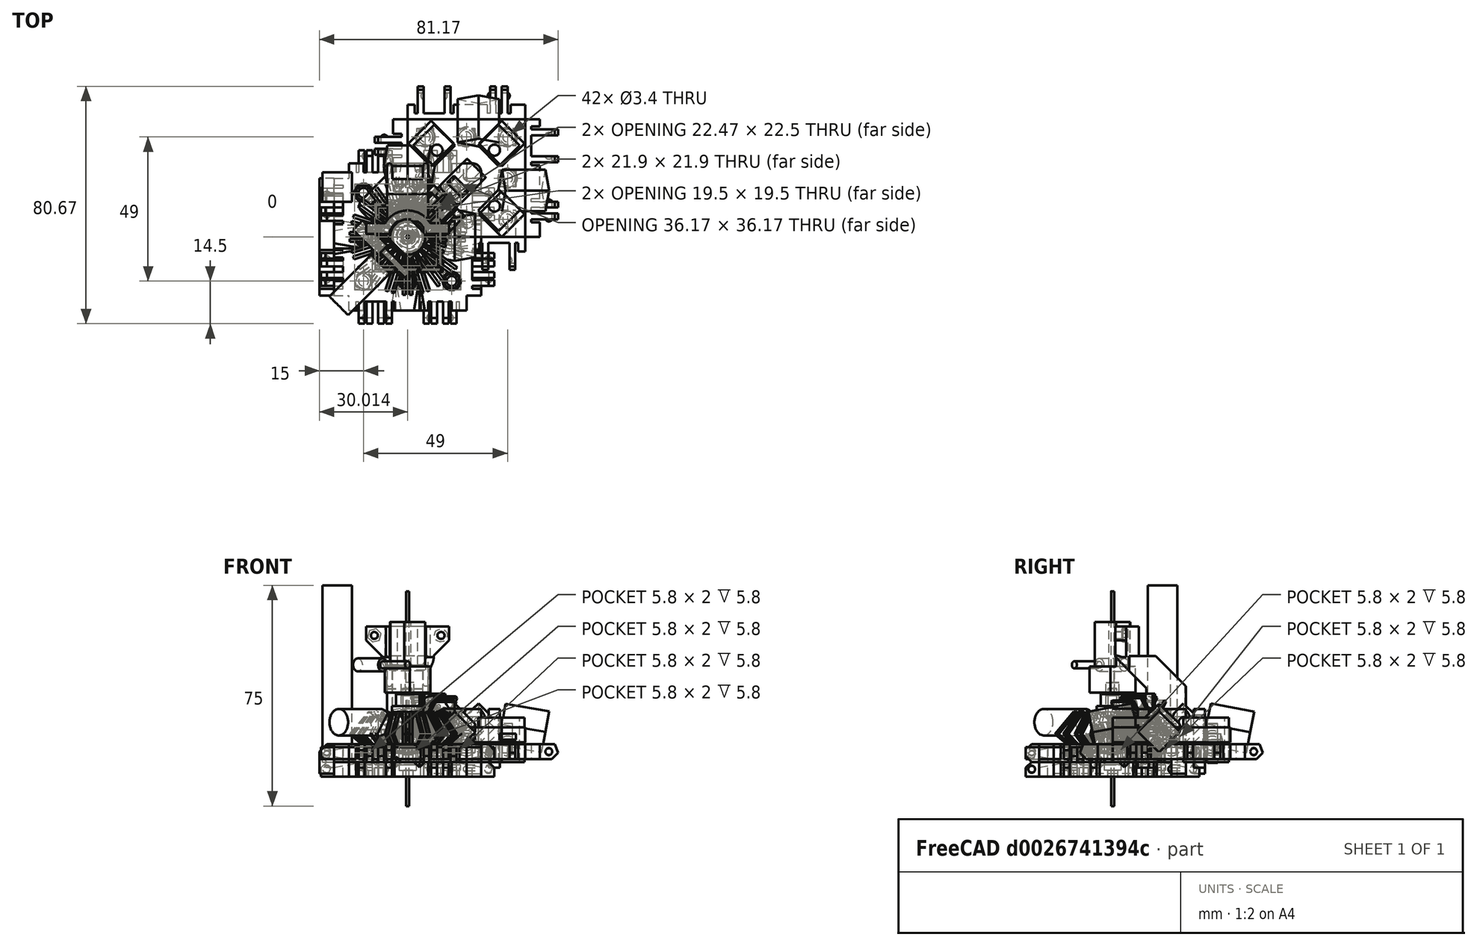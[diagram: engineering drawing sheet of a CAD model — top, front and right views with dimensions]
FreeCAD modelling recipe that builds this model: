
FCSTD DOCUMENT  (FreeCAD 0.18R16146 (Git))
Label: Robot 0.5
License: All rights reserved
LicenseURL: http://en.wikipedia.org/wiki/All_rights_reserved
objects: Part::Box×364, Part::Cut×149, Part::Sphere×107, Part::MultiFuse×99, Part::Cylinder×85, Part::Fuse×47, Part::Feature×40, Part::Chamfer×28, Drawing::FeatureViewAnnotation×17, App::DocumentObjectGroup×6, Part::Cone×5, Part::MultiCommon×5, Part::Fillet×5, Part::FeaturePython×3, Part::Mirroring×2, Drawing::FeaturePage×2
note: 939 computed .brp shape members not serialized (recipe doc carries the construction recipe); baked Part::Feature solids carry a one-line shape summary decoded from their .brp

FEATURE [Part::Box] Box  label="Cube"
  AttacherType = Attacher::AttachEngine3D
  Height = 5
  Length = 40
  Placement = pos=(-20,-20,-2) rot=(0,0,1;0rad)
  Width = 40
FEATURE [Part::Sphere] Sphere003  label="Mag Hole 3"
  Angle1 = -90
  Angle2 = 90
  Angle3 = 360
  AttacherType = Attacher::AttachEngine3D
  Placement = pos=(-15,15,1.7) rot=(0,0,1;0rad)
  Radius = 2.83
FEATURE [Part::Sphere] Sphere005  label="Mag Hole 2"
  Angle1 = -90
  Angle2 = 90
  Angle3 = 360
  AttacherType = Attacher::AttachEngine3D
  Placement = pos=(15,0,1.7) rot=(0,0,1;0rad)
  Radius = 2.825
FEATURE [Part::Sphere] Sphere  label="Mag Hole"
  Angle1 = -90
  Angle2 = 90
  Angle3 = 360
  AttacherType = Attacher::AttachEngine3D
  Placement = pos=(-15,-15,1.7) rot=(0,0,1;0rad)
  Radius = 2.83
FEATURE [Part::MultiFuse] Fusion004  label="Ball Holes"
  Shapes = -> [Sphere,Sphere005,Sphere003]
FEATURE [Part::Cut] Cut003
  Base = -> Box
  Tool = -> Fusion004
FEATURE [Part::Box] Box001  label="Cube001"
  AttacherType = Attacher::AttachEngine3D
  Height = 7
  Length = 5
  Placement = pos=(-5,0,-2) rot=(0,0,1;0rad)
  Width = 40
FEATURE [Part::Box] Box002  label="Cube002"
  AttacherType = Attacher::AttachEngine3D
  Height = 7
  Length = 10
  Placement = pos=(-15,6,-2) rot=(0,0,1;0rad)
  Width = 2
FEATURE [Part::Box] Box003  label="Cube003"
  AttacherType = Attacher::AttachEngine3D
  Height = 7
  Length = 10
  Placement = pos=(-15,10,-2) rot=(0,0,1;0rad)
  Width = 2
FEATURE [Part::Box] Box004  label="Cube004"
  AttacherType = Attacher::AttachEngine3D
  Height = 7
  Length = 10
  Placement = pos=(-15,25.4,-2) rot=(0,0,1;0rad)
  Width = 2
FEATURE [Part::Box] Box005  label="Cube005"
  AttacherType = Attacher::AttachEngine3D
  Height = 7
  Length = 10
  Placement = pos=(-15,34.6,-2) rot=(0,0,1;0rad)
  Width = 2
FEATURE [Part::Sphere] Sphere008
  Angle1 = -90
  Angle2 = 90
  Angle3 = 360
  AttacherType = Attacher::AttachEngine3D
  Placement = pos=(-7.5,6.5,0.5) rot=(0,0,1;0rad)
  Radius = 1.25
FEATURE [Part::Box] Box006  label="Chamfer Cube"
  AttacherType = Attacher::AttachEngine3D
  Height = 10
  Length = 13
  Placement = pos=(-11.69,0,-1.19) rot=(0,-1,0;0.785398rad)
  Width = 40
FEATURE [Part::Sphere] Sphere009
  Angle1 = -90
  Angle2 = 90
  Angle3 = 360
  AttacherType = Attacher::AttachEngine3D
  Placement = pos=(-7.5,11.5,0.5) rot=(0,0,1;0rad)
  Radius = 1.25
FEATURE [Part::Sphere] Sphere010
  Angle1 = -90
  Angle2 = 90
  Angle3 = 360
  AttacherType = Attacher::AttachEngine3D
  Placement = pos=(-7.5,28,0.5) rot=(0,0,1;0rad)
  Radius = 1.5
FEATURE [Part::Sphere] Sphere011
  Angle1 = -90
  Angle2 = 90
  Angle3 = 360
  AttacherType = Attacher::AttachEngine3D
  Placement = pos=(-7.5,34,0.5) rot=(0,0,1;0rad)
  Radius = 1.5
FEATURE [Part::Box] Box007  label="Cube007"
  AttacherType = Attacher::AttachEngine3D
  Height = 7
  Length = 4
  Placement = pos=(-6,5,-2) rot=(0,0,1;0rad)
  Width = 1
FEATURE [Part::Box] Box008  label="Cube008"
  AttacherType = Attacher::AttachEngine3D
  Height = 7
  Length = 4
  Placement = pos=(-6,8,-2) rot=(0,0,1;0rad)
  Width = 2
FEATURE [Part::Box] Box009  label="Cube009"
  AttacherType = Attacher::AttachEngine3D
  Height = 7
  Length = 4
  Placement = pos=(-6,12,-2) rot=(0,0,1;0rad)
  Width = 1
FEATURE [Part::Box] Box010  label="Cube010"
  AttacherType = Attacher::AttachEngine3D
  Height = 7
  Length = 4
  Placement = pos=(-6,24.4,-2) rot=(0,0,1;0rad)
  Width = 1
FEATURE [Part::Box] Box011  label="Cube011"
  AttacherType = Attacher::AttachEngine3D
  Height = 7
  Length = 4
  Placement = pos=(-6,36.6,-2) rot=(0,0,1;0rad)
  Width = 1
FEATURE [Part::Box] Box012  label="Cube012"
  AttacherType = Attacher::AttachEngine3D
  Height = 7
  Length = 4
  Placement = pos=(-6,27.4,-2) rot=(0,0,1;0rad)
  Width = 7.2
FEATURE [Part::MultiFuse] Fusion003  label="Extra Holes for Clips"
  Shapes = -> [Box012,Box009,Box011,Box008,Box010,Box007]
FEATURE [Part::Box] Box013  label="Re-level Edge Clip Block"
  AttacherType = Attacher::AttachEngine3D
  Height = 10
  Length = 20
  Placement = pos=(-19,-2,3) rot=(0,0,1;0rad)
  Width = 44
FEATURE [Part::Box] Box014  label="Cube014"
  AttacherType = Attacher::AttachEngine3D
  Height = 7
  Length = 10
  Placement = pos=(-10,34.6,0) rot=(0,0,1;0rad)
  Width = 2
FEATURE [Part::Box] Box015  label="Cube015"
  AttacherType = Attacher::AttachEngine3D
  Height = 7
  Length = 5
  Width = 40
FEATURE [Part::Box] Box016  label="Cube016"
  AttacherType = Attacher::AttachEngine3D
  Height = 7
  Length = 10
  Placement = pos=(-10,25.4,0) rot=(0,0,1;0rad)
  Width = 2
FEATURE [Part::Box] Box017  label="Cube017"
  AttacherType = Attacher::AttachEngine3D
  Height = 7
  Length = 10
  Placement = pos=(-10,10,0) rot=(0,0,1;0rad)
  Width = 2
FEATURE [Part::Box] Box018  label="Cube018"
  AttacherType = Attacher::AttachEngine3D
  Height = 7
  Length = 10
  Placement = pos=(-10,6,0) rot=(0,0,1;0rad)
  Width = 2
FEATURE [Part::Sphere] Sphere012
  Angle1 = -90
  Angle2 = 90
  Angle3 = 360
  AttacherType = Attacher::AttachEngine3D
  Placement = pos=(-3,6.5,2.5) rot=(0,0,1;0rad)
  Radius = 1.25
FEATURE [Part::Box] Box019  label="Cube019"
  AttacherType = Attacher::AttachEngine3D
  Height = 10
  Length = 13
  Placement = pos=(-10.19,0,-1.19) rot=(0,-1,0;0.785398rad)
  Width = 40
FEATURE [Part::Sphere] Sphere013
  Angle1 = -90
  Angle2 = 90
  Angle3 = 360
  AttacherType = Attacher::AttachEngine3D
  Placement = pos=(-3,11.5,2.5) rot=(0,0,1;0rad)
  Radius = 1.25
FEATURE [Part::Sphere] Sphere014
  Angle1 = -90
  Angle2 = 90
  Angle3 = 360
  AttacherType = Attacher::AttachEngine3D
  Placement = pos=(-3,28,2.5) rot=(0,0,1;0rad)
  Radius = 1.5
FEATURE [Part::Sphere] Sphere015
  Angle1 = -90
  Angle2 = 90
  Angle3 = 360
  AttacherType = Attacher::AttachEngine3D
  Placement = pos=(-3,34,2.5) rot=(0,0,1;0rad)
  Radius = 1.5
FEATURE [Part::MultiFuse] Fusion005
  Shapes = -> [Box015,Box018,Box017,Box016,Box014]
FEATURE [Part::Cut] Cut005
  Base = -> Fusion005
  Tool = -> Box019
FEATURE [Part::MultiFuse] Fusion006
  Shapes = -> [Sphere012,Sphere013,Cut005]
FEATURE [Part::MultiFuse] Fusion007
  Shapes = -> [Sphere015,Sphere014]
FEATURE [Part::Cut] Cut006
  Base = -> Fusion006
  Tool = -> Fusion007
FEATURE [Part::Chamfer] Chamfer002
  Base = -> Cut006
  Edges = 4 edges r=4: [Edge31,Edge37,Edge43,Edge46]
FEATURE [Part::Box] Box020  label="Cube020"
  AttacherType = Attacher::AttachEngine3D
  Height = 7
  Length = 4
  Placement = pos=(-1,5,0) rot=(0,0,1;0rad)
  Width = 1
FEATURE [Part::Box] Box021  label="Cube021"
  AttacherType = Attacher::AttachEngine3D
  Height = 7
  Length = 4
  Placement = pos=(-1,8,0) rot=(0,0,1;0rad)
  Width = 2
FEATURE [Part::Box] Box022  label="Cube022"
  AttacherType = Attacher::AttachEngine3D
  Height = 7
  Length = 4
  Placement = pos=(-1,12,0) rot=(0,0,1;0rad)
  Width = 1
FEATURE [Part::Box] Box023  label="Cube023"
  AttacherType = Attacher::AttachEngine3D
  Height = 7
  Length = 4
  Placement = pos=(-1,24.4,0) rot=(0,0,1;0rad)
  Width = 1
FEATURE [Part::Box] Box024  label="Cube024"
  AttacherType = Attacher::AttachEngine3D
  Height = 7
  Length = 4
  Placement = pos=(-1,36.6,0) rot=(0,0,1;0rad)
  Width = 1
FEATURE [Part::Box] Box025  label="Cube025"
  AttacherType = Attacher::AttachEngine3D
  Height = 7
  Length = 4
  Placement = pos=(-1,27.4,0) rot=(0,0,1;0rad)
  Width = 7.2
FEATURE [Part::MultiFuse] Fusion008
  Shapes = -> [Box025,Box022,Box024,Box021,Box023,Box020]
FEATURE [Part::Cut] Cut007
  Base = -> Chamfer002
  Placement = pos=(-5,40,3) rot=(1,0,0;3.14159rad)
  Tool = -> Fusion008
FEATURE [Part::Box] Box026  label="Cube026"
  AttacherType = Attacher::AttachEngine3D
  Height = 10
  Length = 12
  Placement = pos=(-11,-2,-12) rot=(0,0,1;0rad)
  Width = 44
FEATURE [Part::Cut] Cut008
  Base = -> Cut007
  Placement = pos=(40,0,0) rot=(0,0,1;1.5708rad)
  Tool = -> Box026
FEATURE [Part::Box] Box027  label="Cube027"
  AttacherType = Attacher::AttachEngine3D
  Height = 7
  Length = 4
  Placement = pos=(-1,12,0) rot=(0,0,1;0rad)
  Width = 1
FEATURE [Part::Box] Box028  label="Cube028"
  AttacherType = Attacher::AttachEngine3D
  Height = 10
  Length = 13
  Placement = pos=(-10.19,0,-1.19) rot=(0,-1,0;0.785398rad)
  Width = 40
FEATURE [Part::Box] Box029  label="Cube029"
  AttacherType = Attacher::AttachEngine3D
  Height = 7
  Length = 4
  Placement = pos=(-1,27.4,0) rot=(0,0,1;0rad)
  Width = 7.2
FEATURE [Part::Box] Box030  label="Cube030"
  AttacherType = Attacher::AttachEngine3D
  Height = 7
  Length = 4
  Placement = pos=(-1,5,0) rot=(0,0,1;0rad)
  Width = 1
FEATURE [Part::Box] Box031  label="Cube031"
  AttacherType = Attacher::AttachEngine3D
  Height = 7
  Length = 10
  Placement = pos=(-10,6,0) rot=(0,0,1;0rad)
  Width = 2
FEATURE [Part::Box] Box032  label="Cube032"
  AttacherType = Attacher::AttachEngine3D
  Height = 10
  Length = 12
  Placement = pos=(-11,-2,-12) rot=(0,0,1;0rad)
  Width = 44
FEATURE [Part::Sphere] Sphere016
  Angle1 = -90
  Angle2 = 90
  Angle3 = 360
  AttacherType = Attacher::AttachEngine3D
  Placement = pos=(-3,6.5,2.5) rot=(0,0,1;0rad)
  Radius = 1.25
FEATURE [Part::Box] Box033  label="Cube033"
  AttacherType = Attacher::AttachEngine3D
  Height = 7
  Length = 10
  Placement = pos=(-10,25.4,0) rot=(0,0,1;0rad)
  Width = 2
FEATURE [Part::Box] Box034  label="Cube034"
  AttacherType = Attacher::AttachEngine3D
  Height = 7
  Length = 10
  Placement = pos=(-10,10,0) rot=(0,0,1;0rad)
  Width = 2
FEATURE [Part::Sphere] Sphere017
  Angle1 = -90
  Angle2 = 90
  Angle3 = 360
  AttacherType = Attacher::AttachEngine3D
  Placement = pos=(-3,28,2.5) rot=(0,0,1;0rad)
  Radius = 1.5
FEATURE [Part::Sphere] Sphere018
  Angle1 = -90
  Angle2 = 90
  Angle3 = 360
  AttacherType = Attacher::AttachEngine3D
  Placement = pos=(-3,11.5,2.5) rot=(0,0,1;0rad)
  Radius = 1.25
FEATURE [Part::Box] Box035  label="Cube035"
  AttacherType = Attacher::AttachEngine3D
  Height = 7
  Length = 4
  Placement = pos=(-1,36.6,0) rot=(0,0,1;0rad)
  Width = 1
FEATURE [Part::Sphere] Sphere019
  Angle1 = -90
  Angle2 = 90
  Angle3 = 360
  AttacherType = Attacher::AttachEngine3D
  Placement = pos=(-3,34,2.5) rot=(0,0,1;0rad)
  Radius = 1.5
FEATURE [Part::MultiFuse] Fusion011
  Shapes = -> [Sphere019,Sphere017]
FEATURE [Part::Box] Box036  label="Cube036"
  AttacherType = Attacher::AttachEngine3D
  Height = 7
  Length = 4
  Placement = pos=(-1,8,0) rot=(0,0,1;0rad)
  Width = 2
FEATURE [Part::Box] Box037  label="Cube037"
  AttacherType = Attacher::AttachEngine3D
  Height = 7
  Length = 10
  Placement = pos=(-10,34.6,0) rot=(0,0,1;0rad)
  Width = 2
FEATURE [Part::Box] Box038  label="Cube038"
  AttacherType = Attacher::AttachEngine3D
  Height = 7
  Length = 4
  Placement = pos=(-1,24.4,0) rot=(0,0,1;0rad)
  Width = 1
FEATURE [Part::MultiFuse] Fusion009
  Shapes = -> [Box029,Box027,Box035,Box036,Box038,Box030]
FEATURE [Part::Box] Box039  label="Cube039"
  AttacherType = Attacher::AttachEngine3D
  Height = 7
  Length = 5
  Width = 40
FEATURE [Part::MultiFuse] Fusion012
  Shapes = -> [Box039,Box031,Box034,Box033,Box037]
FEATURE [Part::Cut] Cut011
  Base = -> Fusion012
  Tool = -> Box028
FEATURE [Part::MultiFuse] Fusion010
  Shapes = -> [Sphere016,Sphere018,Cut011]
FEATURE [Part::Cut] Cut012
  Base = -> Fusion010
  Tool = -> Fusion011
FEATURE [Part::Chamfer] Chamfer003
  Base = -> Cut012
  Edges = 4 edges r=4: [Edge31,Edge37,Edge43,Edge46]
FEATURE [Part::Cut] Cut010
  Base = -> Chamfer003
  Placement = pos=(-5,40,3) rot=(1,0,0;3.14159rad)
  Tool = -> Fusion009
FEATURE [Part::Cut] Cut009
  Base = -> Cut010
  Placement = pos=(40,40,0) rot=(0,0,1;3.14159rad)
  Tool = -> Box032
FEATURE [Part::Sphere] Sphere020
  Angle1 = -90
  Angle2 = 90
  Angle3 = 360
  AttacherType = Attacher::AttachEngine3D
  Placement = pos=(-3,11.5,2.5) rot=(0,0,1;0rad)
  Radius = 1.25
FEATURE [Part::Box] Box040  label="Cube040"
  AttacherType = Attacher::AttachEngine3D
  Height = 7
  Length = 10
  Placement = pos=(-10,6,0) rot=(0,0,1;0rad)
  Width = 2
FEATURE [Part::Box] Box041  label="Cube041"
  AttacherType = Attacher::AttachEngine3D
  Height = 7
  Length = 4
  Placement = pos=(-1,8,0) rot=(0,0,1;0rad)
  Width = 2
FEATURE [Part::Box] Box042  label="Cube042"
  AttacherType = Attacher::AttachEngine3D
  Height = 7
  Length = 10
  Placement = pos=(-10,10,0) rot=(0,0,1;0rad)
  Width = 2
FEATURE [Part::Box] Box043  label="Cube043"
  AttacherType = Attacher::AttachEngine3D
  Height = 10
  Length = 12
  Placement = pos=(-11,-2,-12) rot=(0,0,1;0rad)
  Width = 44
FEATURE [Part::Box] Box044  label="Cube044"
  AttacherType = Attacher::AttachEngine3D
  Height = 7
  Length = 4
  Placement = pos=(-1,5,0) rot=(0,0,1;0rad)
  Width = 1
FEATURE [Part::Sphere] Sphere021
  Angle1 = -90
  Angle2 = 90
  Angle3 = 360
  AttacherType = Attacher::AttachEngine3D
  Placement = pos=(-3,28,2.5) rot=(0,0,1;0rad)
  Radius = 1.5
FEATURE [Part::Sphere] Sphere022
  Angle1 = -90
  Angle2 = 90
  Angle3 = 360
  AttacherType = Attacher::AttachEngine3D
  Placement = pos=(-3,6.5,2.5) rot=(0,0,1;0rad)
  Radius = 1.25
FEATURE [Part::Sphere] Sphere023
  Angle1 = -90
  Angle2 = 90
  Angle3 = 360
  AttacherType = Attacher::AttachEngine3D
  Placement = pos=(-3,34,2.5) rot=(0,0,1;0rad)
  Radius = 1.5
FEATURE [Part::Box] Box045  label="Cube045"
  AttacherType = Attacher::AttachEngine3D
  Height = 7
  Length = 4
  Placement = pos=(-1,12,0) rot=(0,0,1;0rad)
  Width = 1
FEATURE [Part::Box] Box046  label="Cube046"
  AttacherType = Attacher::AttachEngine3D
  Height = 7
  Length = 5
  Width = 40
FEATURE [Part::Box] Box047  label="Cube047"
  AttacherType = Attacher::AttachEngine3D
  Height = 7
  Length = 4
  Placement = pos=(-1,36.6,0) rot=(0,0,1;0rad)
  Width = 1
FEATURE [Part::Box] Box048  label="Cube048"
  AttacherType = Attacher::AttachEngine3D
  Height = 7
  Length = 4
  Placement = pos=(-1,24.4,0) rot=(0,0,1;0rad)
  Width = 1
FEATURE [Part::Box] Box049  label="Cube049"
  AttacherType = Attacher::AttachEngine3D
  Height = 7
  Length = 10
  Placement = pos=(-10,25.4,0) rot=(0,0,1;0rad)
  Width = 2
FEATURE [Part::Box] Box050  label="Cube050"
  AttacherType = Attacher::AttachEngine3D
  Height = 10
  Length = 13
  Placement = pos=(-10.19,0,-1.19) rot=(0,-1,0;0.785398rad)
  Width = 40
FEATURE [Part::Box] Box051  label="Cube051"
  AttacherType = Attacher::AttachEngine3D
  Height = 7
  Length = 10
  Placement = pos=(-10,34.6,0) rot=(0,0,1;0rad)
  Width = 2
FEATURE [Part::MultiFuse] Fusion015
  Shapes = -> [Box046,Box040,Box042,Box049,Box051]
FEATURE [Part::Cut] Cut013
  Base = -> Fusion015
  Tool = -> Box050
FEATURE [Part::MultiFuse] Fusion013
  Shapes = -> [Sphere022,Sphere020,Cut013]
FEATURE [Part::MultiFuse] Fusion016
  Shapes = -> [Sphere023,Sphere021]
FEATURE [Part::Cut] Cut014
  Base = -> Fusion013
  Tool = -> Fusion016
FEATURE [Part::Chamfer] Chamfer004
  Base = -> Cut014
  Edges = 4 edges r=4: [Edge31,Edge37,Edge43,Edge46]
FEATURE [Part::Box] Box052  label="Cube052"
  AttacherType = Attacher::AttachEngine3D
  Height = 7
  Length = 4
  Placement = pos=(-1,27.4,0) rot=(0,0,1;0rad)
  Width = 7.2
FEATURE [Part::MultiFuse] Fusion014
  Shapes = -> [Box052,Box045,Box047,Box041,Box048,Box044]
FEATURE [Part::Cut] Cut016
  Base = -> Chamfer004
  Placement = pos=(-5,40,3) rot=(1,0,0;3.14159rad)
  Tool = -> Fusion014
FEATURE [Part::Cut] Cut015
  Base = -> Cut016
  Placement = pos=(0,40,0) rot=(0,0,-1;1.5708rad)
  Tool = -> Box043
FEATURE [Part::Box] Box054  label="Cube054"
  AttacherType = Attacher::AttachEngine3D
  Height = 15
  Length = 10
  Placement = pos=(9,2,-3) rot=(0,0,1;0.785398rad)
  Width = 10
FEATURE [Part::Box] Box055  label="Cube055"
  AttacherType = Attacher::AttachEngine3D
  Height = 15
  Length = 10
  Placement = pos=(31,24,-3) rot=(0,0,1;0.785398rad)
  Width = 10
FEATURE [Part::Box] Box056  label="Cube056"
  AttacherType = Attacher::AttachEngine3D
  Height = 15
  Length = 10
  Placement = pos=(31,2,-3) rot=(0,0,1;0.785398rad)
  Width = 10
FEATURE [Part::Box] Box057  label="Cube057"
  AttacherType = Attacher::AttachEngine3D
  Height = 15
  Length = 10
  Placement = pos=(9,24,-3) rot=(0,0,1;0.785398rad)
  Width = 10
FEATURE [Part::MultiFuse] Fusion017
  Shapes = -> [Box054,Box057,Box056,Box055]
FEATURE [Part::Box] Box058  label="Cube058"
  AttacherType = Attacher::AttachEngine3D
  Height = 5
  Length = 40
  Placement = pos=(0,0,3.7) rot=(0,0,1;0rad)
  Width = 40
FEATURE [Part::Box] Box059  label="Square Nut Hole 008"
  AttacherType = Attacher::AttachEngine3D
  Height = 2
  Length = 5.6
  Placement = pos=(17.2,31.2,4.6) rot=(0,0,1;0rad)
  Width = 5.6
FEATURE [Part::Box] Box060  label="Square Nut Hole 009"
  AttacherType = Attacher::AttachEngine3D
  Height = 2
  Length = 5.6
  Placement = pos=(17.2,-0.85,4.6) rot=(0,0,1;0rad)
  Width = 10
FEATURE [Part::Box] Box061  label="Square Nut Hole 010"
  AttacherType = Attacher::AttachEngine3D
  Height = 2
  Length = 5.6
  Placement = pos=(31.2,-0.85,4.6) rot=(0,0,1;0rad)
  Width = 10
FEATURE [Part::Box] Box062  label="Square Nut Hole 011"
  AttacherType = Attacher::AttachEngine3D
  Height = 2
  Length = 5.4
  Placement = pos=(31.3,17.3,4.6) rot=(0,0,1;0rad)
  Width = 5.4
FEATURE [Part::Box] Box063  label="Square Nut Hole 012"
  AttacherType = Attacher::AttachEngine3D
  Height = 2
  Length = 5.7
  Placement = pos=(3.15,31.15,4.6) rot=(0,0,1;0rad)
  Width = 5.7
FEATURE [Part::Box] Box064  label="Square Nut Hole 013"
  AttacherType = Attacher::AttachEngine3D
  Height = 2
  Length = 5.5
  Placement = pos=(31.25,31.25,4.6) rot=(0,0,1;0rad)
  Width = 5.5
FEATURE [Part::Box] Box065  label="Square Nut Hole 014"
  AttacherType = Attacher::AttachEngine3D
  Height = 2
  Length = 5.8
  Placement = pos=(3.1,17.1,4.6) rot=(0,0,1;0rad)
  Width = 5.8
FEATURE [Part::Box] Box066  label="Square Nut Hole 015"
  AttacherType = Attacher::AttachEngine3D
  Height = 2
  Length = 5.6
  Placement = pos=(3.2,-0.85,4.6) rot=(0,0,1;0rad)
  Width = 10
FEATURE [Part::Sphere] Sphere006  label="Nut Clearence1"
  Angle1 = -90
  Angle2 = 90
  Angle3 = 360
  AttacherType = Attacher::AttachEngine3D
  Placement = pos=(6,6,2.4) rot=(0,0,1;0rad)
  Radius = 3.35
FEATURE [Part::Sphere] Sphere024
  Angle1 = -90
  Angle2 = 90
  Angle3 = 360
  AttacherType = Attacher::AttachEngine3D
  Placement = pos=(6,34,2.4) rot=(0,0,1;0rad)
  Radius = 3.35
FEATURE [Part::Sphere] Sphere007
  Angle1 = -90
  Angle2 = 90
  Angle3 = 360
  AttacherType = Attacher::AttachEngine3D
  Placement = pos=(34,20,2.4) rot=(0,0,1;0rad)
  Radius = 3.35
FEATURE [Part::Sphere] Sphere001
  Angle1 = -90
  Angle2 = 90
  Angle3 = 360
  AttacherType = Attacher::AttachEngine3D
  Placement = pos=(34,6,2.4) rot=(0,0,1;0rad)
  Radius = 3.35
FEATURE [Part::Sphere] Sphere025
  Angle1 = -90
  Angle2 = 90
  Angle3 = 360
  AttacherType = Attacher::AttachEngine3D
  Placement = pos=(20,6,2.4) rot=(0,0,1;0rad)
  Radius = 3.35
FEATURE [Part::Sphere] Sphere026
  Angle1 = -90
  Angle2 = 90
  Angle3 = 360
  AttacherType = Attacher::AttachEngine3D
  Placement = pos=(20,34,2.4) rot=(0,0,1;0rad)
  Radius = 3.35
FEATURE [Part::Sphere] Sphere004
  Angle1 = -90
  Angle2 = 90
  Angle3 = 360
  AttacherType = Attacher::AttachEngine3D
  Placement = pos=(6,20,2.4) rot=(0,0,1;0rad)
  Radius = 3.35
FEATURE [Part::Sphere] Sphere002
  Angle1 = -90
  Angle2 = 90
  Angle3 = 360
  AttacherType = Attacher::AttachEngine3D
  Placement = pos=(34,34,2.4) rot=(0,0,1;0rad)
  Radius = 3.35
FEATURE [Part::Cylinder] Cylinder
  Angle = 360
  AttacherType = Attacher::AttachEngine3D
  Height = 10
  Placement = pos=(6,6,0) rot=(0,0,1;0rad)
  Radius = 1.7
FEATURE [Part::Cylinder] Cylinder002
  Angle = 360
  AttacherType = Attacher::AttachEngine3D
  Height = 10
  Placement = pos=(34,6,0) rot=(0,0,1;0rad)
  Radius = 1.7
FEATURE [Part::Cylinder] Cylinder001
  Angle = 360
  AttacherType = Attacher::AttachEngine3D
  Height = 10
  Placement = pos=(20,6,0) rot=(0,0,1;0rad)
  Radius = 1.7
FEATURE [Part::Cylinder] Cylinder003
  Angle = 360
  AttacherType = Attacher::AttachEngine3D
  Height = 10
  Placement = pos=(34,34,0) rot=(0,0,1;0rad)
  Radius = 1.7
FEATURE [Part::Cylinder] Cylinder004
  Angle = 360
  AttacherType = Attacher::AttachEngine3D
  Height = 10
  Placement = pos=(20,34,0) rot=(0,0,1;0rad)
  Radius = 1.7
FEATURE [Part::Cylinder] Cylinder005
  Angle = 360
  AttacherType = Attacher::AttachEngine3D
  Height = 10
  Placement = pos=(6,34,0) rot=(0,0,1;0rad)
  Radius = 1.7
FEATURE [Part::Cylinder] Cylinder006
  Angle = 360
  AttacherType = Attacher::AttachEngine3D
  Height = 10
  Placement = pos=(6,20,0) rot=(0,0,1;0rad)
  Radius = 1.7
FEATURE [Part::Cylinder] Cylinder007
  Angle = 360
  AttacherType = Attacher::AttachEngine3D
  Height = 10
  Placement = pos=(34,20,0) rot=(0,0,1;0rad)
  Radius = 1.7
FEATURE [Part::MultiFuse] Fusion018
  Shapes = -> [Cylinder,Cylinder004,Cylinder007,Cylinder005,Cylinder006,Cylinder001,Cylinder002,Cylinder003]
FEATURE [Part::MultiFuse] Fusion019
  Shapes = -> [Sphere007,Sphere024,Sphere006,Sphere025,Sphere001,Sphere026,Sphere004,Sphere002]
FEATURE [Part::MultiFuse] Fusion020
  Shapes = -> [Box061,Box065,Box062,Box063,Box064,Box066,Box059,Box060]
FEATURE [Part::Cut] Cut017
  Base = -> Box058
  Tool = -> Fusion020
FEATURE [Part::Cut] Cut019
  Base = -> Cut017
  Tool = -> Fusion019
FEATURE [Part::Cut] Cut018
  Base = -> Cut019
  Tool = -> Fusion018
FEATURE [Part::Cylinder] Cylinder008
  Angle = 360
  AttacherType = Attacher::AttachEngine3D
  Height = 20
  Placement = pos=(10,10.5,-5) rot=(0,0,1;0rad)
  Radius = 1.9
FEATURE [Part::Cylinder] Cylinder009
  Angle = 360
  AttacherType = Attacher::AttachEngine3D
  Height = 20
  Placement = pos=(29.5,10.5,-5) rot=(0,0,1;0rad)
  Radius = 1.9
FEATURE [Part::Cylinder] Cylinder010
  Angle = 360
  AttacherType = Attacher::AttachEngine3D
  Height = 20
  Placement = pos=(29.5,29.5,-5) rot=(0,0,1;0rad)
  Radius = 1.9
FEATURE [Part::Cylinder] Cylinder011
  Angle = 360
  AttacherType = Attacher::AttachEngine3D
  Height = 20
  Placement = pos=(10,29.5,-7) rot=(0,0,1;0rad)
  Radius = 1.9
FEATURE [Part::MultiFuse] Fusion021  label="M2 Screw holes"
  Shapes = -> [Cylinder008,Cylinder009,Cylinder011,Cylinder010]
FEATURE [Part::Box] Box067  label="Square Nut Hole 016"
  AttacherType = Attacher::AttachEngine3D
  Height = 2
  Length = 5.8
  Placement = pos=(31.1,17.1,4.6) rot=(0,0,1;0rad)
  Width = 5.8
FEATURE [Part::Box] Box068  label="Square Nut Hole 017"
  AttacherType = Attacher::AttachEngine3D
  Height = 2
  Length = 5.8
  Placement = pos=(17.1,36.9,2.1) rot=(1,0,0;3.14159rad)
  Width = 5.8
FEATURE [Part::Box] Box069  label="Square Nut Hole 018"
  AttacherType = Attacher::AttachEngine3D
  Height = 2
  Length = 5.8
  Placement = pos=(-2.9,2.9,2.1) rot=(1,0,0;3.14159rad)
  Width = 5.8
FEATURE [Part::Box] Box070  label="Square Nut Hole 019"
  AttacherType = Attacher::AttachEngine3D
  Height = 2
  Length = 5.8
  Placement = pos=(3.1,3.1,4.6) rot=(0,0,1;0rad)
  Width = 5.8
FEATURE [Part::Box] Box071  label="Square Nut Hole 020"
  AttacherType = Attacher::AttachEngine3D
  Height = 2
  Length = 5.8
  Placement = pos=(3.1,31.1,4.6) rot=(0,0,1;0rad)
  Width = 5.8
FEATURE [Part::Box] Box072  label="Square Nut Hole 021"
  AttacherType = Attacher::AttachEngine3D
  Height = 2
  Length = 5.8
  Placement = pos=(17.1,31.1,4.6) rot=(0,0,1;0rad)
  Width = 5.8
FEATURE [Part::Box] Box073  label="Square Nut Hole 022"
  AttacherType = Attacher::AttachEngine3D
  Height = 2
  Length = 5.8
  Placement = pos=(31.1,31.1,4.6) rot=(0,0,1;0rad)
  Width = 5.8
FEATURE [Part::Box] Box074  label="Square Nut Hole 023"
  AttacherType = Attacher::AttachEngine3D
  Height = 2
  Length = 5.8
  Placement = pos=(3.1,17.1,4.6) rot=(0,0,1;0rad)
  Width = 5.8
FEATURE [Part::Cylinder] Cylinder012
  Angle = 360
  AttacherType = Attacher::AttachEngine3D
  Height = 10
  Placement = pos=(6,6,0) rot=(0,0,1;0rad)
  Radius = 1.7
FEATURE [Part::Cylinder] Cylinder013
  Angle = 360
  AttacherType = Attacher::AttachEngine3D
  Height = 10
  Placement = pos=(34,34,0) rot=(0,0,1;0rad)
  Radius = 1.7
FEATURE [Part::Cylinder] Cylinder014
  Angle = 360
  AttacherType = Attacher::AttachEngine3D
  Height = 10
  Placement = pos=(20,34,0) rot=(0,0,1;0rad)
  Radius = 1.7
FEATURE [Part::Cylinder] Cylinder015
  Angle = 360
  AttacherType = Attacher::AttachEngine3D
  Height = 10
  Placement = pos=(6,34,0) rot=(0,0,1;0rad)
  Radius = 1.7
FEATURE [Part::Cylinder] Cylinder016
  Angle = 360
  AttacherType = Attacher::AttachEngine3D
  Height = 10
  Placement = pos=(6,20,0) rot=(0,0,1;0rad)
  Radius = 1.7
FEATURE [Part::Cylinder] Cylinder017
  Angle = 360
  AttacherType = Attacher::AttachEngine3D
  Height = 10
  Placement = pos=(34,20,0) rot=(0,0,1;0rad)
  Radius = 1.7
FEATURE [Part::Cylinder] Cylinder018
  Angle = 360
  AttacherType = Attacher::AttachEngine3D
  Height = 10
  Placement = pos=(0,0,6.7) rot=(1,0,0;3.14159rad)
  Radius = 1.7
FEATURE [Part::Cylinder] Cylinder019
  Angle = 360
  AttacherType = Attacher::AttachEngine3D
  Height = 10
  Placement = pos=(20,34,6.7) rot=(1,0,0;3.14159rad)
  Radius = 1.7
FEATURE [Part::Box] Box075  label="Cube059"
  AttacherType = Attacher::AttachEngine3D
  Height = 5
  Length = 40
  Placement = pos=(-20,-20,-2) rot=(0,0,1;0rad)
  Width = 40
FEATURE [Part::Sphere] Sphere027
  Angle1 = -90
  Angle2 = 90
  Angle3 = 360
  AttacherType = Attacher::AttachEngine3D
  Placement = pos=(34,20,2.4) rot=(0,0,1;0rad)
  Radius = 3.35
FEATURE [Part::Sphere] Sphere028  label="Nut Clearence002"
  Angle1 = -90
  Angle2 = 90
  Angle3 = 360
  AttacherType = Attacher::AttachEngine3D
  Placement = pos=(6,6,2.4) rot=(0,0,1;0rad)
  Radius = 3.35
FEATURE [Part::Sphere] Sphere029
  Angle1 = -90
  Angle2 = 90
  Angle3 = 360
  AttacherType = Attacher::AttachEngine3D
  Placement = pos=(34,34,2.4) rot=(0,0,1;0rad)
  Radius = 3.35
FEATURE [Part::Sphere] Sphere030
  Angle1 = -90
  Angle2 = 90
  Angle3 = 360
  AttacherType = Attacher::AttachEngine3D
  Placement = pos=(0,0,4.3) rot=(1,0,0;3.14159rad)
  Radius = 3.35
FEATURE [Part::Sphere] Sphere031
  Angle1 = -90
  Angle2 = 90
  Angle3 = 360
  AttacherType = Attacher::AttachEngine3D
  Placement = pos=(20,34,4.3) rot=(1,0,0;3.14159rad)
  Radius = 3.35
FEATURE [Part::Sphere] Sphere032
  Angle1 = -90
  Angle2 = 90
  Angle3 = 360
  AttacherType = Attacher::AttachEngine3D
  Placement = pos=(6,34,2.4) rot=(0,0,1;0rad)
  Radius = 3.35
FEATURE [Part::Sphere] Sphere033
  Angle1 = -90
  Angle2 = 90
  Angle3 = 360
  AttacherType = Attacher::AttachEngine3D
  Placement = pos=(6,20,2.4) rot=(0,0,1;0rad)
  Radius = 3.35
FEATURE [Part::Sphere] Sphere034
  Angle1 = -90
  Angle2 = 90
  Angle3 = 360
  AttacherType = Attacher::AttachEngine3D
  Placement = pos=(20,34,2.4) rot=(0,0,1;0rad)
  Radius = 3.35
FEATURE [Part::Box] Box076  label="Cube060"
  AttacherType = Attacher::AttachEngine3D
  Height = 15
  Length = 19.5
  Placement = pos=(-9.75,-9.75,-3) rot=(0,0,1;0rad)
  Width = 19.5
FEATURE [Part::Box] Box077  label="Cube061"
  AttacherType = Attacher::AttachEngine3D
  Height = 15
  Length = 11
  Placement = pos=(8,24,-3) rot=(0,0,1;0.785398rad)
  Width = 11
FEATURE [Part::Box] Box078  label="Cube062"
  AttacherType = Attacher::AttachEngine3D
  Height = 15
  Length = 11
  Placement = pos=(8,0,-3) rot=(0,0,1;0.785398rad)
  Width = 11
FEATURE [Part::Box] Box079  label="Cube063"
  AttacherType = Attacher::AttachEngine3D
  Height = 15
  Length = 11
  Placement = pos=(32,0,-3) rot=(0,0,1;0.785398rad)
  Width = 11
FEATURE [Part::Box] Box080  label="Cube064"
  AttacherType = Attacher::AttachEngine3D
  Height = 15
  Length = 11
  Placement = pos=(32,24,-3) rot=(0,0,1;0.785398rad)
  Width = 11
FEATURE [Part::MultiFuse] Fusion022
  Shapes = -> [Box078,Box077,Box079,Box080]
FEATURE [Part::Cylinder] Cylinder020
  Angle = 360
  AttacherType = Attacher::AttachEngine3D
  Height = 20
  Placement = pos=(29.5,10.5,-5) rot=(0,0,1;0rad)
  Radius = 1.9
FEATURE [Part::Cylinder] Cylinder021
  Angle = 360
  AttacherType = Attacher::AttachEngine3D
  Height = 20
  Placement = pos=(10,29.5,-7) rot=(0,0,1;0rad)
  Radius = 1.9
FEATURE [Part::Cylinder] Cylinder022
  Angle = 360
  AttacherType = Attacher::AttachEngine3D
  Height = 20
  Placement = pos=(10,10.5,-5) rot=(0,0,1;0rad)
  Radius = 1.9
FEATURE [Part::Cylinder] Cylinder023
  Angle = 360
  AttacherType = Attacher::AttachEngine3D
  Height = 20
  Placement = pos=(29.5,29.5,-5) rot=(0,0,1;0rad)
  Radius = 1.9
FEATURE [Part::MultiFuse] Fusion023  label="M2 Screw holes001"
  Shapes = -> [Cylinder022,Cylinder020,Cylinder021,Cylinder023]
FEATURE [App::DocumentObjectGroup] Group  label="Cubes"
  Group = -> [Fusion017,Fusion022]
FEATURE [Part::Box] Box083  label="Cube067"
  AttacherType = Attacher::AttachEngine3D
  Height = 10
  Length = 24
  Placement = pos=(-12,-12,2.1) rot=(0,0,1;0rad)
  Width = 24
FEATURE [Part::Box] Box084  label="Cube068"
  AttacherType = Attacher::AttachEngine3D
  Height = 14
  Length = 20
  Placement = pos=(-10,-10,0) rot=(0,0,1;0rad)
  Width = 20
FEATURE [Part::Cut] Cut020
  Base = -> Box083
  Tool = -> Box084
FEATURE [Part::Chamfer] Chamfer007  label="Glue Channel Ball"
  Base = -> Cut020
  Edges = 8 edges r=0.95: [Edge4,Edge5,Edge14,Edge16,Edge17,Edge18,Edge19,Edge20]
FEATURE [Part::Chamfer] Chamfer008  label="Octogon Ball"
  Base = -> Box076
  Edges = 4 edges r=4: [Edge1,Edge3,Edge5,Edge7]
FEATURE [Part::Box] Box085  label="Cube069"
  AttacherType = Attacher::AttachEngine3D
  Height = 15
  Length = 19.5
  Placement = pos=(-9.75,-9.75,-14) rot=(0,0,1;0rad)
  Width = 19.5
FEATURE [Part::Box] Box086  label="Cube070"
  AttacherType = Attacher::AttachEngine3D
  Height = 10
  Length = 10
  Placement = pos=(4,-26,1) rot=(0.205904,-0.974848,-0.085288;0.803573rad)
  Width = 15
FEATURE [Part::Box] Box089  label="Cube073"
  AttacherType = Attacher::AttachEngine3D
  Height = 10
  Length = 10
  Placement = pos=(17,32.0919,9.95) rot=(-0.225436,0.969773,-0.093378;0.807337rad)
  Width = 15
FEATURE [Part::Box] Box090  label="Cube074"
  AttacherType = Attacher::AttachEngine3D
  Height = 10
  Length = 15
  Placement = pos=(30.8481,15.8,2.86019) rot=(0.974848,0.205904,-0.085288;0.803573rad)
  Width = 10
FEATURE [Part::Box] Box091  label="Cube075"
  AttacherType = Attacher::AttachEngine3D
  Height = 10
  Length = 10
  Placement = pos=(7.9081,17,9.95) rot=(-0.450607,0.280623,0.847469;1.65638rad)
  Width = 15
FEATURE [Part::Box] Box092  label="Cube076"
  AttacherType = Attacher::AttachEngine3D
  Height = 10
  Length = 10
  Placement = pos=(23,7.9081,9.95) rot=(-0.381178,-0.08861,0.920245;3.06822rad)
  Width = 15
FEATURE [Part::Box] Box093  label="Cube077"
  AttacherType = Attacher::AttachEngine3D
  Height = 7
  Length = 5
  Width = 40
FEATURE [Part::Box] Box094  label="Cube078"
  AttacherType = Attacher::AttachEngine3D
  Height = 7
  Length = 10
  Placement = pos=(-10,6,0) rot=(0,0,1;0rad)
  Width = 2
FEATURE [Part::Box] Box095  label="Cube079"
  AttacherType = Attacher::AttachEngine3D
  Height = 7
  Length = 10
  Placement = pos=(-10,10,0) rot=(0,0,1;0rad)
  Width = 2
FEATURE [Part::Box] Box096  label="Cube080"
  AttacherType = Attacher::AttachEngine3D
  Height = 7
  Length = 10
  Placement = pos=(-10,25.4,0) rot=(0,0,1;0rad)
  Width = 2
FEATURE [Part::Box] Box097  label="Cube081"
  AttacherType = Attacher::AttachEngine3D
  Height = 7
  Length = 10
  Placement = pos=(-10,34.6,0) rot=(0,0,1;0rad)
  Width = 2
FEATURE [Part::Sphere] Sphere035
  Angle1 = -90
  Angle2 = 90
  Angle3 = 360
  AttacherType = Attacher::AttachEngine3D
  Placement = pos=(-3,6.5,2.5) rot=(0,0,1;0rad)
  Radius = 1.25
FEATURE [Part::Box] Box098  label="Cube082"
  AttacherType = Attacher::AttachEngine3D
  Height = 10
  Length = 13
  Placement = pos=(-10.19,0,-1.19) rot=(0,-1,0;0.785398rad)
  Width = 40
FEATURE [Part::Sphere] Sphere036
  Angle1 = -90
  Angle2 = 90
  Angle3 = 360
  AttacherType = Attacher::AttachEngine3D
  Placement = pos=(-3,11.5,2.5) rot=(0,0,1;0rad)
  Radius = 1.25
FEATURE [Part::Sphere] Sphere037
  Angle1 = -90
  Angle2 = 90
  Angle3 = 360
  AttacherType = Attacher::AttachEngine3D
  Placement = pos=(-3,28,2.5) rot=(0,0,1;0rad)
  Radius = 1.5
FEATURE [Part::Sphere] Sphere038
  Angle1 = -90
  Angle2 = 90
  Angle3 = 360
  AttacherType = Attacher::AttachEngine3D
  Placement = pos=(-3,34,2.5) rot=(0,0,1;0rad)
  Radius = 1.5
FEATURE [Part::MultiFuse] Fusion030
  Shapes = -> [Box093,Box094,Box095,Box096,Box097]
FEATURE [Part::Cut] Cut025
  Base = -> Fusion030
  Tool = -> Box098
FEATURE [Part::MultiFuse] Fusion031
  Shapes = -> [Sphere035,Sphere036,Cut025]
FEATURE [Part::MultiFuse] Fusion032
  Shapes = -> [Sphere038,Sphere037]
FEATURE [Part::Cut] Cut026
  Base = -> Fusion031
  Tool = -> Fusion032
FEATURE [Part::Chamfer] Chamfer009
  Base = -> Cut026
  Edges = 4 edges r=4: [Edge31,Edge37,Edge43,Edge46]
FEATURE [Part::Box] Box099  label="Cube083"
  AttacherType = Attacher::AttachEngine3D
  Height = 7
  Length = 4
  Placement = pos=(-1,5,0) rot=(0,0,1;0rad)
  Width = 1
FEATURE [Part::Box] Box100  label="Cube084"
  AttacherType = Attacher::AttachEngine3D
  Height = 7
  Length = 4
  Placement = pos=(-1,8,0) rot=(0,0,1;0rad)
  Width = 2
FEATURE [Part::Box] Box101  label="Cube085"
  AttacherType = Attacher::AttachEngine3D
  Height = 7
  Length = 4
  Placement = pos=(-1,12,0) rot=(0,0,1;0rad)
  Width = 1
FEATURE [Part::Box] Box102  label="Cube086"
  AttacherType = Attacher::AttachEngine3D
  Height = 7
  Length = 4
  Placement = pos=(-1,24.4,0) rot=(0,0,1;0rad)
  Width = 1
FEATURE [Part::Box] Box103  label="Cube087"
  AttacherType = Attacher::AttachEngine3D
  Height = 7
  Length = 4
  Placement = pos=(-1,36.6,0) rot=(0,0,1;0rad)
  Width = 1
FEATURE [Part::Box] Box104  label="Cube088"
  AttacherType = Attacher::AttachEngine3D
  Height = 7
  Length = 4
  Placement = pos=(-1,27.4,0) rot=(0,0,1;0rad)
  Width = 7.2
FEATURE [Part::MultiFuse] Fusion033
  Shapes = -> [Box104,Box101,Box103,Box100,Box102,Box099]
FEATURE [Part::Cut] Cut027
  Base = -> Chamfer009
  Placement = pos=(-5,40,3) rot=(1,0,0;3.14159rad)
  Tool = -> Fusion033
FEATURE [Part::Box] Box105  label="Cube089"
  AttacherType = Attacher::AttachEngine3D
  Height = 10
  Length = 12
  Placement = pos=(-11,-2,-12) rot=(0,0,1;0rad)
  Width = 44
FEATURE [Part::Cut] Cut028
  Base = -> Cut027
  Tool = -> Box105
FEATURE [Part::Box] Box106  label="Cube090"
  AttacherType = Attacher::AttachEngine3D
  Height = 7
  Length = 10
  Placement = pos=(-10,34.6,0) rot=(0,0,1;0rad)
  Width = 2
FEATURE [Part::Box] Box107  label="Cube091"
  AttacherType = Attacher::AttachEngine3D
  Height = 7
  Length = 5
  Width = 40
FEATURE [Part::Box] Box108  label="Cube092"
  AttacherType = Attacher::AttachEngine3D
  Height = 7
  Length = 10
  Placement = pos=(-10,25.4,0) rot=(0,0,1;0rad)
  Width = 2
FEATURE [Part::Box] Box109  label="Cube093"
  AttacherType = Attacher::AttachEngine3D
  Height = 7
  Length = 10
  Placement = pos=(-10,10,0) rot=(0,0,1;0rad)
  Width = 2
FEATURE [Part::Box] Box110  label="Cube094"
  AttacherType = Attacher::AttachEngine3D
  Height = 7
  Length = 10
  Placement = pos=(-10,6,0) rot=(0,0,1;0rad)
  Width = 2
FEATURE [Part::Sphere] Sphere039
  Angle1 = -90
  Angle2 = 90
  Angle3 = 360
  AttacherType = Attacher::AttachEngine3D
  Placement = pos=(-3,6.5,2.5) rot=(0,0,1;0rad)
  Radius = 1.25
FEATURE [Part::Box] Box111  label="Cube095"
  AttacherType = Attacher::AttachEngine3D
  Height = 10
  Length = 13
  Placement = pos=(-10.19,0,-1.19) rot=(0,-1,0;0.785398rad)
  Width = 40
FEATURE [Part::Sphere] Sphere040
  Angle1 = -90
  Angle2 = 90
  Angle3 = 360
  AttacherType = Attacher::AttachEngine3D
  Placement = pos=(-3,11.5,2.5) rot=(0,0,1;0rad)
  Radius = 1.25
FEATURE [Part::Sphere] Sphere041
  Angle1 = -90
  Angle2 = 90
  Angle3 = 360
  AttacherType = Attacher::AttachEngine3D
  Placement = pos=(-3,28,2.5) rot=(0,0,1;0rad)
  Radius = 1.5
FEATURE [Part::Sphere] Sphere042
  Angle1 = -90
  Angle2 = 90
  Angle3 = 360
  AttacherType = Attacher::AttachEngine3D
  Placement = pos=(-3,34,2.5) rot=(0,0,1;0rad)
  Radius = 1.5
FEATURE [Part::MultiFuse] Fusion034
  Shapes = -> [Box107,Box110,Box109,Box108,Box106]
FEATURE [Part::Cut] Cut029
  Base = -> Fusion034
  Tool = -> Box111
FEATURE [Part::MultiFuse] Fusion035
  Shapes = -> [Sphere039,Sphere040,Cut029]
FEATURE [Part::MultiFuse] Fusion036
  Shapes = -> [Sphere042,Sphere041]
FEATURE [Part::Cut] Cut030
  Base = -> Fusion035
  Tool = -> Fusion036
FEATURE [Part::Chamfer] Chamfer010
  Base = -> Cut030
  Edges = 4 edges r=4: [Edge31,Edge37,Edge43,Edge46]
FEATURE [Part::Box] Box112  label="Cube096"
  AttacherType = Attacher::AttachEngine3D
  Height = 7
  Length = 4
  Placement = pos=(-1,5,0) rot=(0,0,1;0rad)
  Width = 1
FEATURE [Part::Box] Box113  label="Cube097"
  AttacherType = Attacher::AttachEngine3D
  Height = 7
  Length = 4
  Placement = pos=(-1,8,0) rot=(0,0,1;0rad)
  Width = 2
FEATURE [Part::Box] Box114  label="Cube098"
  AttacherType = Attacher::AttachEngine3D
  Height = 7
  Length = 4
  Placement = pos=(-1,12,0) rot=(0,0,1;0rad)
  Width = 1
FEATURE [Part::Box] Box115  label="Cube099"
  AttacherType = Attacher::AttachEngine3D
  Height = 7
  Length = 4
  Placement = pos=(-1,24.4,0) rot=(0,0,1;0rad)
  Width = 1
FEATURE [Part::Box] Box116  label="Cube100"
  AttacherType = Attacher::AttachEngine3D
  Height = 7
  Length = 4
  Placement = pos=(-1,36.6,0) rot=(0,0,1;0rad)
  Width = 1
FEATURE [Part::Box] Box117  label="Cube101"
  AttacherType = Attacher::AttachEngine3D
  Height = 7
  Length = 4
  Placement = pos=(-1,27.4,0) rot=(0,0,1;0rad)
  Width = 7.2
FEATURE [Part::MultiFuse] Fusion037
  Shapes = -> [Box117,Box114,Box116,Box113,Box115,Box112]
FEATURE [Part::Cut] Cut031
  Base = -> Chamfer010
  Placement = pos=(-5,40,3) rot=(1,0,0;3.14159rad)
  Tool = -> Fusion037
FEATURE [Part::Box] Box118  label="Cube102"
  AttacherType = Attacher::AttachEngine3D
  Height = 10
  Length = 12
  Placement = pos=(-11,-2,-12) rot=(0,0,1;0rad)
  Width = 44
FEATURE [Part::Cut] Cut032
  Base = -> Cut031
  Placement = pos=(40,0,0) rot=(0,0,1;1.5708rad)
  Tool = -> Box118
FEATURE [Part::Box] Box119  label="Cube103"
  AttacherType = Attacher::AttachEngine3D
  Height = 7
  Length = 4
  Placement = pos=(-1,12,0) rot=(0,0,1;0rad)
  Width = 1
FEATURE [Part::Box] Box120  label="Cube104"
  AttacherType = Attacher::AttachEngine3D
  Height = 10
  Length = 13
  Placement = pos=(-10.19,0,-1.19) rot=(0,-1,0;0.785398rad)
  Width = 40
FEATURE [Part::Box] Box121  label="Cube105"
  AttacherType = Attacher::AttachEngine3D
  Height = 7
  Length = 4
  Placement = pos=(-1,27.4,0) rot=(0,0,1;0rad)
  Width = 7.2
FEATURE [Part::Box] Box122  label="Cube106"
  AttacherType = Attacher::AttachEngine3D
  Height = 7
  Length = 4
  Placement = pos=(-1,5,0) rot=(0,0,1;0rad)
  Width = 1
FEATURE [Part::Box] Box123  label="Cube107"
  AttacherType = Attacher::AttachEngine3D
  Height = 7
  Length = 10
  Placement = pos=(-10,6,0) rot=(0,0,1;0rad)
  Width = 2
FEATURE [Part::Box] Box124  label="Cube108"
  AttacherType = Attacher::AttachEngine3D
  Height = 10
  Length = 12
  Placement = pos=(-11,-2,-12) rot=(0,0,1;0rad)
  Width = 44
FEATURE [Part::Sphere] Sphere043
  Angle1 = -90
  Angle2 = 90
  Angle3 = 360
  AttacherType = Attacher::AttachEngine3D
  Placement = pos=(-3,6.5,2.5) rot=(0,0,1;0rad)
  Radius = 1.25
FEATURE [Part::Box] Box125  label="Cube109"
  AttacherType = Attacher::AttachEngine3D
  Height = 7
  Length = 10
  Placement = pos=(-10,25.4,0) rot=(0,0,1;0rad)
  Width = 2
FEATURE [Part::Box] Box126  label="Cube110"
  AttacherType = Attacher::AttachEngine3D
  Height = 7
  Length = 10
  Placement = pos=(-10,10,0) rot=(0,0,1;0rad)
  Width = 2
FEATURE [Part::Sphere] Sphere044
  Angle1 = -90
  Angle2 = 90
  Angle3 = 360
  AttacherType = Attacher::AttachEngine3D
  Placement = pos=(-3,28,2.5) rot=(0,0,1;0rad)
  Radius = 1.5
FEATURE [Part::Sphere] Sphere045
  Angle1 = -90
  Angle2 = 90
  Angle3 = 360
  AttacherType = Attacher::AttachEngine3D
  Placement = pos=(-3,11.5,2.5) rot=(0,0,1;0rad)
  Radius = 1.25
FEATURE [Part::Box] Box127  label="Cube111"
  AttacherType = Attacher::AttachEngine3D
  Height = 7
  Length = 4
  Placement = pos=(-1,36.6,0) rot=(0,0,1;0rad)
  Width = 1
FEATURE [Part::Sphere] Sphere046
  Angle1 = -90
  Angle2 = 90
  Angle3 = 360
  AttacherType = Attacher::AttachEngine3D
  Placement = pos=(-3,34,2.5) rot=(0,0,1;0rad)
  Radius = 1.5
FEATURE [Part::MultiFuse] Fusion040
  Shapes = -> [Sphere046,Sphere044]
FEATURE [Part::Box] Box128  label="Cube112"
  AttacherType = Attacher::AttachEngine3D
  Height = 7
  Length = 4
  Placement = pos=(-1,8,0) rot=(0,0,1;0rad)
  Width = 2
FEATURE [Part::Box] Box129  label="Cube113"
  AttacherType = Attacher::AttachEngine3D
  Height = 7
  Length = 10
  Placement = pos=(-10,34.6,0) rot=(0,0,1;0rad)
  Width = 2
FEATURE [Part::Box] Box130  label="Cube114"
  AttacherType = Attacher::AttachEngine3D
  Height = 7
  Length = 4
  Placement = pos=(-1,24.4,0) rot=(0,0,1;0rad)
  Width = 1
FEATURE [Part::MultiFuse] Fusion038
  Shapes = -> [Box121,Box119,Box127,Box128,Box130,Box122]
FEATURE [Part::Box] Box131  label="Cube115"
  AttacherType = Attacher::AttachEngine3D
  Height = 7
  Length = 5
  Width = 40
FEATURE [Part::MultiFuse] Fusion041
  Shapes = -> [Box131,Box123,Box126,Box125,Box129]
FEATURE [Part::Cut] Cut035
  Base = -> Fusion041
  Tool = -> Box120
FEATURE [Part::MultiFuse] Fusion039
  Shapes = -> [Sphere043,Sphere045,Cut035]
FEATURE [Part::Cut] Cut036
  Base = -> Fusion039
  Tool = -> Fusion040
FEATURE [Part::Chamfer] Chamfer011
  Base = -> Cut036
  Edges = 4 edges r=4: [Edge31,Edge37,Edge43,Edge46]
FEATURE [Part::Cut] Cut034
  Base = -> Chamfer011
  Placement = pos=(-5,40,3) rot=(1,0,0;3.14159rad)
  Tool = -> Fusion038
FEATURE [Part::Cut] Cut033
  Base = -> Cut034
  Placement = pos=(40,40,0) rot=(0,0,1;3.14159rad)
  Tool = -> Box124
FEATURE [Part::Sphere] Sphere047
  Angle1 = -90
  Angle2 = 90
  Angle3 = 360
  AttacherType = Attacher::AttachEngine3D
  Placement = pos=(-3,11.5,2.5) rot=(0,0,1;0rad)
  Radius = 1.25
FEATURE [Part::Box] Box132  label="Cube116"
  AttacherType = Attacher::AttachEngine3D
  Height = 7
  Length = 10
  Placement = pos=(-10,6,0) rot=(0,0,1;0rad)
  Width = 2
FEATURE [Part::Box] Box133  label="Cube117"
  AttacherType = Attacher::AttachEngine3D
  Height = 7
  Length = 4
  Placement = pos=(-1,8,0) rot=(0,0,1;0rad)
  Width = 2
FEATURE [Part::Box] Box134  label="Cube118"
  AttacherType = Attacher::AttachEngine3D
  Height = 7
  Length = 10
  Placement = pos=(-10,10,0) rot=(0,0,1;0rad)
  Width = 2
FEATURE [Part::Box] Box135  label="Cube119"
  AttacherType = Attacher::AttachEngine3D
  Height = 10
  Length = 12
  Placement = pos=(-11,-2,-12) rot=(0,0,1;0rad)
  Width = 44
FEATURE [Part::Box] Box136  label="Cube120"
  AttacherType = Attacher::AttachEngine3D
  Height = 7
  Length = 4
  Placement = pos=(-1,5,0) rot=(0,0,1;0rad)
  Width = 1
FEATURE [Part::Sphere] Sphere048
  Angle1 = -90
  Angle2 = 90
  Angle3 = 360
  AttacherType = Attacher::AttachEngine3D
  Placement = pos=(-3,28,2.5) rot=(0,0,1;0rad)
  Radius = 1.5
FEATURE [Part::Sphere] Sphere049
  Angle1 = -90
  Angle2 = 90
  Angle3 = 360
  AttacherType = Attacher::AttachEngine3D
  Placement = pos=(-3,6.5,2.5) rot=(0,0,1;0rad)
  Radius = 1.25
FEATURE [Part::Sphere] Sphere050
  Angle1 = -90
  Angle2 = 90
  Angle3 = 360
  AttacherType = Attacher::AttachEngine3D
  Placement = pos=(-3,34,2.5) rot=(0,0,1;0rad)
  Radius = 1.5
FEATURE [Part::Box] Box137  label="Cube121"
  AttacherType = Attacher::AttachEngine3D
  Height = 7
  Length = 4
  Placement = pos=(-1,12,0) rot=(0,0,1;0rad)
  Width = 1
FEATURE [Part::Box] Box138  label="Cube122"
  AttacherType = Attacher::AttachEngine3D
  Height = 7
  Length = 5
  Width = 40
FEATURE [Part::Box] Box139  label="Cube123"
  AttacherType = Attacher::AttachEngine3D
  Height = 7
  Length = 4
  Placement = pos=(-1,36.6,0) rot=(0,0,1;0rad)
  Width = 1
FEATURE [Part::Box] Box140  label="Cube124"
  AttacherType = Attacher::AttachEngine3D
  Height = 7
  Length = 4
  Placement = pos=(-1,24.4,0) rot=(0,0,1;0rad)
  Width = 1
FEATURE [Part::Box] Box141  label="Cube125"
  AttacherType = Attacher::AttachEngine3D
  Height = 7
  Length = 10
  Placement = pos=(-10,25.4,0) rot=(0,0,1;0rad)
  Width = 2
FEATURE [Part::Box] Box142  label="Cube126"
  AttacherType = Attacher::AttachEngine3D
  Height = 10
  Length = 13
  Placement = pos=(-10.19,0,-1.19) rot=(0,-1,0;0.785398rad)
  Width = 40
FEATURE [Part::Box] Box143  label="Cube127"
  AttacherType = Attacher::AttachEngine3D
  Height = 7
  Length = 10
  Placement = pos=(-10,34.6,0) rot=(0,0,1;0rad)
  Width = 2
FEATURE [Part::MultiFuse] Fusion044
  Shapes = -> [Box138,Box132,Box134,Box141,Box143]
FEATURE [Part::Cut] Cut037
  Base = -> Fusion044
  Tool = -> Box142
FEATURE [Part::MultiFuse] Fusion042
  Shapes = -> [Sphere049,Sphere047,Cut037]
FEATURE [Part::MultiFuse] Fusion045
  Shapes = -> [Sphere050,Sphere048]
FEATURE [Part::Cut] Cut038
  Base = -> Fusion042
  Tool = -> Fusion045
FEATURE [Part::Chamfer] Chamfer012
  Base = -> Cut038
  Edges = 4 edges r=4: [Edge31,Edge37,Edge43,Edge46]
FEATURE [Part::Box] Box144  label="Cube128"
  AttacherType = Attacher::AttachEngine3D
  Height = 7
  Length = 4
  Placement = pos=(-1,27.4,0) rot=(0,0,1;0rad)
  Width = 7.2
FEATURE [Part::MultiFuse] Fusion043
  Shapes = -> [Box144,Box137,Box139,Box133,Box140,Box136]
FEATURE [Part::Cut] Cut040
  Base = -> Chamfer012
  Placement = pos=(-5,40,3) rot=(1,0,0;3.14159rad)
  Tool = -> Fusion043
FEATURE [Part::Cut] Cut039
  Base = -> Cut040
  Placement = pos=(0,40,0) rot=(0,0,-1;1.5708rad)
  Tool = -> Box135
FEATURE [Part::MultiFuse] Fusion048
  Shapes = -> [Box089,Box091,Box090,Box092]
FEATURE [Part::Box] Box145  label="Cube129"
  AttacherType = Attacher::AttachEngine3D
  Height = 15
  Length = 19.5
  Placement = pos=(-9.75,-9.75,-14) rot=(0,0,1;0rad)
  Width = 19.5
FEATURE [Part::Box] Box146  label="Cube130"
  AttacherType = Attacher::AttachEngine3D
  Height = 15
  Length = 19.5
  Placement = pos=(-9.75,-9.75,-3) rot=(0,0,1;0rad)
  Width = 19.5
FEATURE [Part::Chamfer] Chamfer013  label="Octagon"
  Base = -> Box146
  Edges = 4 edges r=4: [Edge1,Edge3,Edge5,Edge7]
FEATURE [Part::Box] Box147  label="Cube131"
  AttacherType = Attacher::AttachEngine3D
  Height = 10
  Length = 24
  Placement = pos=(-12,-12,2.1) rot=(0,0,1;0rad)
  Width = 24
FEATURE [Part::Box] Box148  label="Cube132"
  AttacherType = Attacher::AttachEngine3D
  Height = 14
  Length = 20
  Placement = pos=(-10,-10,0) rot=(0,0,1;0rad)
  Width = 20
FEATURE [Part::Cut] Cut043
  Base = -> Box147
  Tool = -> Box148
FEATURE [Part::Chamfer] Chamfer014  label="Glue Channel"
  Base = -> Cut043
  Edges = 8 edges r=0.95: [Edge4,Edge5,Edge14,Edge16,Edge17,Edge18,Edge19,Edge20]
FEATURE [Part::Cut] Cut047
  Base = -> Cut003
  Tool = -> Chamfer007
FEATURE [Part::Cylinder] Cylinder024
  Angle = 360
  AttacherType = Attacher::AttachEngine3D
  Height = 10
  Placement = pos=(-15,-15,-5) rot=(0,0,1;0rad)
  Radius = 1.7
FEATURE [Part::Cylinder] Cylinder025
  Angle = 360
  AttacherType = Attacher::AttachEngine3D
  Height = 10
  Placement = pos=(15,0,-5) rot=(0,0,1;0rad)
  Radius = 1.7
FEATURE [Part::Cylinder] Cylinder026
  Angle = 360
  AttacherType = Attacher::AttachEngine3D
  Height = 10
  Placement = pos=(-15,15,-5) rot=(0,0,1;0rad)
  Radius = 1.7
FEATURE [Part::MultiFuse] Fusion052  label="Screw Holes to remove ball mags"
  Shapes = -> [Cylinder024,Cylinder025,Cylinder026]
FEATURE [Drawing::FeatureViewAnnotation] Annotation
  Font = Sans
  Rotation = 0
  Scale = 7
  Text = 0.4Added in Holes to Mag plate for removal of magnet
  ViewResult = <g transform="translate(14,23) rotate(0)">\n<text id="Annotation"\n font-family="Sans"\n font-size="7"\n fill="#000000">\n<tspan x="0" dy="1em">0.4Added in Holes to Mag plate for removal of magnet</tspan>\n</text>\n</g>
  Visible = false
  X = 14
  Y = 23
FEATURE [Part::Box] Box149  label="Re-level Edge Clip Block001"
  AttacherType = Attacher::AttachEngine3D
  Height = 10
  Length = 12
  Placement = pos=(-21.5,-2,-7) rot=(0,0,1;0rad)
  Width = 44
FEATURE [Part::Fuse] Fusion  label="Bumps"
  Base = -> Sphere008
  Tool = -> Sphere009
FEATURE [Part::Fuse] Fusion053  label="Holes"
  Base = -> Sphere010
  Tool = -> Sphere011
FEATURE [Part::MultiFuse] Fusion054
  Shapes = -> [Box001,Box002,Box003,Box004,Box005]
FEATURE [Part::Fuse] Fusion055
  Base = -> Fusion
  Tool = -> Fusion054
FEATURE [Part::Cut] Cut
  Base = -> Fusion055
  Tool = -> Fusion053
FEATURE [Part::Cut] Cut056
  Base = -> Cut
  Tool = -> Fusion003
FEATURE [Part::Cut] Cut057
  Base = -> Cut056
  Tool = -> Box013
FEATURE [Part::Cut] Cut058
  Base = -> Cut057
  Tool = -> Box149
FEATURE [Part::Cut] Cut059  label="Edge Clips Master"
  Base = -> Cut058
  Placement = pos=(-20,-20,0) rot=(0,0,1;0rad)
  Tool = -> Box006
FEATURE [Part::Box] Box150  label="Cube133"
  AttacherType = Attacher::AttachEngine3D
  Height = 7
  Length = 5
  Placement = pos=(-5,0,-2) rot=(0,0,1;0rad)
  Width = 40
FEATURE [Part::Box] Box151  label="Cube134"
  AttacherType = Attacher::AttachEngine3D
  Height = 7
  Length = 10
  Placement = pos=(-15,6,-2) rot=(0,0,1;0rad)
  Width = 2
FEATURE [Part::Box] Box152  label="Cube135"
  AttacherType = Attacher::AttachEngine3D
  Height = 7
  Length = 10
  Placement = pos=(-15,10,-2) rot=(0,0,1;0rad)
  Width = 2
FEATURE [Part::Box] Box153  label="Cube136"
  AttacherType = Attacher::AttachEngine3D
  Height = 7
  Length = 10
  Placement = pos=(-15,25.4,-2) rot=(0,0,1;0rad)
  Width = 2
FEATURE [Part::Box] Box154  label="Cube137"
  AttacherType = Attacher::AttachEngine3D
  Height = 7
  Length = 10
  Placement = pos=(-15,34.6,-2) rot=(0,0,1;0rad)
  Width = 2
FEATURE [Part::Sphere] Sphere051
  Angle1 = -90
  Angle2 = 90
  Angle3 = 360
  AttacherType = Attacher::AttachEngine3D
  Placement = pos=(-7.5,6.5,0.5) rot=(0,0,1;0rad)
  Radius = 1.25
FEATURE [Part::Box] Box155  label="Chamfer Cube001"
  AttacherType = Attacher::AttachEngine3D
  Height = 10
  Length = 13
  Placement = pos=(-11.69,0,-1.19) rot=(0,-1,0;0.785398rad)
  Width = 40
FEATURE [Part::Sphere] Sphere052
  Angle1 = -90
  Angle2 = 90
  Angle3 = 360
  AttacherType = Attacher::AttachEngine3D
  Placement = pos=(-7.5,11.5,0.5) rot=(0,0,1;0rad)
  Radius = 1.25
FEATURE [Part::Sphere] Sphere053
  Angle1 = -90
  Angle2 = 90
  Angle3 = 360
  AttacherType = Attacher::AttachEngine3D
  Placement = pos=(-7.5,28,0.5) rot=(0,0,1;0rad)
  Radius = 1.5
FEATURE [Part::Sphere] Sphere054
  Angle1 = -90
  Angle2 = 90
  Angle3 = 360
  AttacherType = Attacher::AttachEngine3D
  Placement = pos=(-7.5,34,0.5) rot=(0,0,1;0rad)
  Radius = 1.5
FEATURE [Part::Box] Box156  label="Cube138"
  AttacherType = Attacher::AttachEngine3D
  Height = 7
  Length = 4
  Placement = pos=(-6,5,-2) rot=(0,0,1;0rad)
  Width = 1
FEATURE [Part::Box] Box157  label="Cube139"
  AttacherType = Attacher::AttachEngine3D
  Height = 7
  Length = 4
  Placement = pos=(-6,8,-2) rot=(0,0,1;0rad)
  Width = 2
FEATURE [Part::Box] Box158  label="Cube140"
  AttacherType = Attacher::AttachEngine3D
  Height = 7
  Length = 4
  Placement = pos=(-6,12,-2) rot=(0,0,1;0rad)
  Width = 1
FEATURE [Part::Box] Box159  label="Cube141"
  AttacherType = Attacher::AttachEngine3D
  Height = 7
  Length = 4
  Placement = pos=(-6,24.4,-2) rot=(0,0,1;0rad)
  Width = 1
FEATURE [Part::Box] Box160  label="Cube142"
  AttacherType = Attacher::AttachEngine3D
  Height = 7
  Length = 4
  Placement = pos=(-6,36.6,-2) rot=(0,0,1;0rad)
  Width = 1
FEATURE [Part::Box] Box161  label="Cube143"
  AttacherType = Attacher::AttachEngine3D
  Height = 7
  Length = 4
  Placement = pos=(-6,27.4,-2) rot=(0,0,1;0rad)
  Width = 7.2
FEATURE [Part::MultiFuse] Fusion056  label="Extra Holes for Clips001"
  Shapes = -> [Box161,Box158,Box160,Box157,Box159,Box156]
FEATURE [Part::Box] Box162  label="Re-level Edge Clip Block002"
  AttacherType = Attacher::AttachEngine3D
  Height = 10
  Length = 20
  Placement = pos=(-19,-2,3) rot=(0,0,1;0rad)
  Width = 44
FEATURE [Part::Box] Box163  label="Re-level Edge Clip Block003"
  AttacherType = Attacher::AttachEngine3D
  Height = 10
  Length = 12
  Placement = pos=(-21.5,-2,-7) rot=(0,0,1;0rad)
  Width = 44
FEATURE [Part::Fuse] Fusion057  label="Bumps001"
  Base = -> Sphere051
  Tool = -> Sphere052
FEATURE [Part::Fuse] Fusion058  label="Holes001"
  Base = -> Sphere053
  Tool = -> Sphere054
FEATURE [Part::MultiFuse] Fusion059
  Shapes = -> [Box150,Box151,Box152,Box153,Box154]
FEATURE [Part::Fuse] Fusion060
  Base = -> Fusion057
  Tool = -> Fusion059
FEATURE [Part::Cut] Cut060
  Base = -> Fusion060
  Tool = -> Fusion058
FEATURE [Part::Cut] Cut061
  Base = -> Cut060
  Tool = -> Fusion056
FEATURE [Part::Cut] Cut062
  Base = -> Cut061
  Tool = -> Box162
FEATURE [Part::Cut] Cut063
  Base = -> Cut062
  Tool = -> Box163
FEATURE [Part::Cut] Cut064  label="Copy Edge Clip"
  Base = -> Cut063
  Placement = pos=(-27,20,-7) rot=(0.707107,0,-0.707107;3.14159rad)
  Tool = -> Box155
FEATURE [Part::Box] Box164  label="Cube144"
  AttacherType = Attacher::AttachEngine3D
  Height = 7
  Length = 5
  Placement = pos=(-5,0,-2) rot=(0,0,1;0rad)
  Width = 40
FEATURE [Part::Box] Box165  label="Cube145"
  AttacherType = Attacher::AttachEngine3D
  Height = 7
  Length = 10
  Placement = pos=(-15,6,-2) rot=(0,0,1;0rad)
  Width = 2
FEATURE [Part::Box] Box166  label="Cube146"
  AttacherType = Attacher::AttachEngine3D
  Height = 7
  Length = 10
  Placement = pos=(-15,10,-2) rot=(0,0,1;0rad)
  Width = 2
FEATURE [Part::Box] Box167  label="Cube147"
  AttacherType = Attacher::AttachEngine3D
  Height = 7
  Length = 10
  Placement = pos=(-15,25.4,-2) rot=(0,0,1;0rad)
  Width = 2
FEATURE [Part::Box] Box168  label="Cube148"
  AttacherType = Attacher::AttachEngine3D
  Height = 7
  Length = 10
  Placement = pos=(-15,34.6,-2) rot=(0,0,1;0rad)
  Width = 2
FEATURE [Part::Sphere] Sphere055
  Angle1 = -90
  Angle2 = 90
  Angle3 = 360
  AttacherType = Attacher::AttachEngine3D
  Placement = pos=(-7.5,6.5,0.5) rot=(0,0,1;0rad)
  Radius = 1.25
FEATURE [Part::Box] Box169  label="Chamfer Cube002"
  AttacherType = Attacher::AttachEngine3D
  Height = 10
  Length = 13
  Placement = pos=(-11.69,0,-1.19) rot=(0,-1,0;0.785398rad)
  Width = 40
FEATURE [Part::Sphere] Sphere056
  Angle1 = -90
  Angle2 = 90
  Angle3 = 360
  AttacherType = Attacher::AttachEngine3D
  Placement = pos=(-7.5,11.5,0.5) rot=(0,0,1;0rad)
  Radius = 1.25
FEATURE [Part::Sphere] Sphere057
  Angle1 = -90
  Angle2 = 90
  Angle3 = 360
  AttacherType = Attacher::AttachEngine3D
  Placement = pos=(-7.5,28,0.5) rot=(0,0,1;0rad)
  Radius = 1.5
FEATURE [Part::Sphere] Sphere058
  Angle1 = -90
  Angle2 = 90
  Angle3 = 360
  AttacherType = Attacher::AttachEngine3D
  Placement = pos=(-7.5,34,0.5) rot=(0,0,1;0rad)
  Radius = 1.5
FEATURE [Part::Box] Box170  label="Cube149"
  AttacherType = Attacher::AttachEngine3D
  Height = 7
  Length = 4
  Placement = pos=(-6,5,-2) rot=(0,0,1;0rad)
  Width = 1
FEATURE [Part::Box] Box171  label="Cube150"
  AttacherType = Attacher::AttachEngine3D
  Height = 7
  Length = 4
  Placement = pos=(-6,8,-2) rot=(0,0,1;0rad)
  Width = 2
FEATURE [Part::Box] Box172  label="Cube151"
  AttacherType = Attacher::AttachEngine3D
  Height = 7
  Length = 4
  Placement = pos=(-6,12,-2) rot=(0,0,1;0rad)
  Width = 1
FEATURE [Part::Box] Box173  label="Cube152"
  AttacherType = Attacher::AttachEngine3D
  Height = 7
  Length = 4
  Placement = pos=(-6,24.4,-2) rot=(0,0,1;0rad)
  Width = 1
FEATURE [Part::Box] Box174  label="Cube153"
  AttacherType = Attacher::AttachEngine3D
  Height = 7
  Length = 4
  Placement = pos=(-6,36.6,-2) rot=(0,0,1;0rad)
  Width = 1
FEATURE [Part::Box] Box175  label="Cube154"
  AttacherType = Attacher::AttachEngine3D
  Height = 7
  Length = 4
  Placement = pos=(-6,27.4,-2) rot=(0,0,1;0rad)
  Width = 7.2
FEATURE [Part::MultiFuse] Fusion061  label="Extra Holes for Clips002"
  Shapes = -> [Box175,Box172,Box174,Box171,Box173,Box170]
FEATURE [Part::Box] Box176  label="Re-level Edge Clip Block004"
  AttacherType = Attacher::AttachEngine3D
  Height = 10
  Length = 20
  Placement = pos=(-19,-2,3) rot=(0,0,1;0rad)
  Width = 44
FEATURE [Part::Box] Box177  label="Re-level Edge Clip Block005"
  AttacherType = Attacher::AttachEngine3D
  Height = 10
  Length = 12
  Placement = pos=(-21.5,-2,-7) rot=(0,0,1;0rad)
  Width = 44
FEATURE [Part::Fuse] Fusion062  label="Bumps002"
  Base = -> Sphere055
  Tool = -> Sphere056
FEATURE [Part::Fuse] Fusion063  label="Holes002"
  Base = -> Sphere057
  Tool = -> Sphere058
FEATURE [Part::MultiFuse] Fusion064
  Shapes = -> [Box164,Box165,Box166,Box167,Box168]
FEATURE [Part::Fuse] Fusion065
  Base = -> Fusion062
  Tool = -> Fusion064
FEATURE [Part::Cut] Cut065
  Base = -> Fusion065
  Tool = -> Fusion063
FEATURE [Part::Cut] Cut066
  Base = -> Cut065
  Tool = -> Fusion061
FEATURE [Part::Cut] Cut067
  Base = -> Cut066
  Tool = -> Box176
FEATURE [Part::Cut] Cut068
  Base = -> Cut067
  Tool = -> Box177
FEATURE [Part::Cut] Cut069  label="Edge Clips001"
  Base = -> Cut068
  Placement = pos=(20,-20,0) rot=(0,0,1;1.5708rad)
  Tool = -> Box169
FEATURE [Part::Box] Box178  label="Cube155"
  AttacherType = Attacher::AttachEngine3D
  Height = 7
  Length = 5
  Placement = pos=(-5,0,-2) rot=(0,0,1;0rad)
  Width = 40
FEATURE [Part::Box] Box179  label="Cube156"
  AttacherType = Attacher::AttachEngine3D
  Height = 7
  Length = 10
  Placement = pos=(-15,10,-2) rot=(0,0,1;0rad)
  Width = 2
FEATURE [Part::Box] Box180  label="Re-level Edge Clip Block006"
  AttacherType = Attacher::AttachEngine3D
  Height = 10
  Length = 20
  Placement = pos=(-19,-2,3) rot=(0,0,1;0rad)
  Width = 44
FEATURE [Part::Box] Box181  label="Cube157"
  AttacherType = Attacher::AttachEngine3D
  Height = 7
  Length = 4
  Placement = pos=(-6,27.4,-2) rot=(0,0,1;0rad)
  Width = 7.2
FEATURE [Part::Box] Box182  label="Cube158"
  AttacherType = Attacher::AttachEngine3D
  Height = 7
  Length = 4
  Placement = pos=(-6,12,-2) rot=(0,0,1;0rad)
  Width = 1
FEATURE [Part::Sphere] Sphere059
  Angle1 = -90
  Angle2 = 90
  Angle3 = 360
  AttacherType = Attacher::AttachEngine3D
  Placement = pos=(-7.5,6.5,0.5) rot=(0,0,1;0rad)
  Radius = 1.25
FEATURE [Part::Box] Box183  label="Cube159"
  AttacherType = Attacher::AttachEngine3D
  Height = 7
  Length = 10
  Placement = pos=(-15,25.4,-2) rot=(0,0,1;0rad)
  Width = 2
FEATURE [Part::Box] Box184  label="Cube160"
  AttacherType = Attacher::AttachEngine3D
  Height = 7
  Length = 4
  Placement = pos=(-6,36.6,-2) rot=(0,0,1;0rad)
  Width = 1
FEATURE [Part::Sphere] Sphere060
  Angle1 = -90
  Angle2 = 90
  Angle3 = 360
  AttacherType = Attacher::AttachEngine3D
  Placement = pos=(-7.5,34,0.5) rot=(0,0,1;0rad)
  Radius = 1.5
FEATURE [Part::Box] Box185  label="Cube161"
  AttacherType = Attacher::AttachEngine3D
  Height = 7
  Length = 4
  Placement = pos=(-6,24.4,-2) rot=(0,0,1;0rad)
  Width = 1
FEATURE [Part::Box] Box186  label="Cube162"
  AttacherType = Attacher::AttachEngine3D
  Height = 7
  Length = 4
  Placement = pos=(-6,8,-2) rot=(0,0,1;0rad)
  Width = 2
FEATURE [Part::Box] Box187  label="Re-level Edge Clip Block007"
  AttacherType = Attacher::AttachEngine3D
  Height = 10
  Length = 12
  Placement = pos=(-21.5,-2,-7) rot=(0,0,1;0rad)
  Width = 44
FEATURE [Part::Sphere] Sphere061
  Angle1 = -90
  Angle2 = 90
  Angle3 = 360
  AttacherType = Attacher::AttachEngine3D
  Placement = pos=(-7.5,11.5,0.5) rot=(0,0,1;0rad)
  Radius = 1.25
FEATURE [Part::Sphere] Sphere062
  Angle1 = -90
  Angle2 = 90
  Angle3 = 360
  AttacherType = Attacher::AttachEngine3D
  Placement = pos=(-7.5,28,0.5) rot=(0,0,1;0rad)
  Radius = 1.5
FEATURE [Part::Fuse] Fusion066  label="Holes003"
  Base = -> Sphere062
  Tool = -> Sphere060
FEATURE [Part::Box] Box188  label="Cube163"
  AttacherType = Attacher::AttachEngine3D
  Height = 7
  Length = 10
  Placement = pos=(-15,34.6,-2) rot=(0,0,1;0rad)
  Width = 2
FEATURE [Part::Box] Box189  label="Cube164"
  AttacherType = Attacher::AttachEngine3D
  Height = 7
  Length = 4
  Placement = pos=(-6,5,-2) rot=(0,0,1;0rad)
  Width = 1
FEATURE [Part::MultiFuse] Fusion067  label="Extra Holes for Clips003"
  Shapes = -> [Box181,Box182,Box184,Box186,Box185,Box189]
FEATURE [Part::Box] Box190  label="Cube165"
  AttacherType = Attacher::AttachEngine3D
  Height = 7
  Length = 10
  Placement = pos=(-15,6,-2) rot=(0,0,1;0rad)
  Width = 2
FEATURE [Part::MultiFuse] Fusion069
  Shapes = -> [Box178,Box190,Box179,Box183,Box188]
FEATURE [Part::Fuse] Fusion070  label="Bumps003"
  Base = -> Sphere059
  Tool = -> Sphere061
FEATURE [Part::Fuse] Fusion068
  Base = -> Fusion070
  Tool = -> Fusion069
FEATURE [Part::Cut] Cut073
  Base = -> Fusion068
  Tool = -> Fusion066
FEATURE [Part::Cut] Cut070
  Base = -> Cut073
  Tool = -> Fusion067
FEATURE [Part::Cut] Cut071
  Base = -> Cut070
  Tool = -> Box180
FEATURE [Part::Cut] Cut072
  Base = -> Cut071
  Tool = -> Box187
FEATURE [Part::Box] Box191  label="Chamfer Cube003"
  AttacherType = Attacher::AttachEngine3D
  Height = 10
  Length = 13
  Placement = pos=(-11.69,0,-1.19) rot=(0,-1,0;0.785398rad)
  Width = 40
FEATURE [Part::Cut] Cut074  label="Edge Clips002"
  Base = -> Cut072
  Placement = pos=(20,20,0) rot=(0,0,1;3.14159rad)
  Tool = -> Box191
FEATURE [Part::Box] Box192  label="Cube166"
  AttacherType = Attacher::AttachEngine3D
  Height = 7
  Length = 10
  Placement = pos=(-15,6,-2) rot=(0,0,1;0rad)
  Width = 2
FEATURE [Part::Box] Box193  label="Chamfer Cube004"
  AttacherType = Attacher::AttachEngine3D
  Height = 10
  Length = 13
  Placement = pos=(-11.69,0,-1.19) rot=(0,-1,0;0.785398rad)
  Width = 40
FEATURE [Part::Box] Box194  label="Re-level Edge Clip Block008"
  AttacherType = Attacher::AttachEngine3D
  Height = 10
  Length = 20
  Placement = pos=(-19,-2,3) rot=(0,0,1;0rad)
  Width = 44
FEATURE [Part::Box] Box195  label="Cube167"
  AttacherType = Attacher::AttachEngine3D
  Height = 7
  Length = 10
  Placement = pos=(-15,10,-2) rot=(0,0,1;0rad)
  Width = 2
FEATURE [Part::Box] Box196  label="Cube168"
  AttacherType = Attacher::AttachEngine3D
  Height = 7
  Length = 5
  Placement = pos=(-5,0,-2) rot=(0,0,1;0rad)
  Width = 40
FEATURE [Part::Box] Box197  label="Cube169"
  AttacherType = Attacher::AttachEngine3D
  Height = 7
  Length = 4
  Placement = pos=(-6,5,-2) rot=(0,0,1;0rad)
  Width = 1
FEATURE [Part::Box] Box198  label="Cube170"
  AttacherType = Attacher::AttachEngine3D
  Height = 7
  Length = 4
  Placement = pos=(-6,12,-2) rot=(0,0,1;0rad)
  Width = 1
FEATURE [Part::Box] Box199  label="Cube171"
  AttacherType = Attacher::AttachEngine3D
  Height = 7
  Length = 4
  Placement = pos=(-6,27.4,-2) rot=(0,0,1;0rad)
  Width = 7.2
FEATURE [Part::Box] Box200  label="Cube172"
  AttacherType = Attacher::AttachEngine3D
  Height = 7
  Length = 4
  Placement = pos=(-6,24.4,-2) rot=(0,0,1;0rad)
  Width = 1
FEATURE [Part::Sphere] Sphere063
  Angle1 = -90
  Angle2 = 90
  Angle3 = 360
  AttacherType = Attacher::AttachEngine3D
  Placement = pos=(-7.5,28,0.5) rot=(0,0,1;0rad)
  Radius = 1.5
FEATURE [Part::Sphere] Sphere064
  Angle1 = -90
  Angle2 = 90
  Angle3 = 360
  AttacherType = Attacher::AttachEngine3D
  Placement = pos=(-7.5,11.5,0.5) rot=(0,0,1;0rad)
  Radius = 1.25
FEATURE [Part::Box] Box201  label="Cube173"
  AttacherType = Attacher::AttachEngine3D
  Height = 7
  Length = 4
  Placement = pos=(-6,8,-2) rot=(0,0,1;0rad)
  Width = 2
FEATURE [Part::Box] Box202  label="Cube174"
  AttacherType = Attacher::AttachEngine3D
  Height = 7
  Length = 10
  Placement = pos=(-15,25.4,-2) rot=(0,0,1;0rad)
  Width = 2
FEATURE [Part::Sphere] Sphere065
  Angle1 = -90
  Angle2 = 90
  Angle3 = 360
  AttacherType = Attacher::AttachEngine3D
  Placement = pos=(-7.5,6.5,0.5) rot=(0,0,1;0rad)
  Radius = 1.25
FEATURE [Part::Fuse] Fusion073  label="Bumps004"
  Base = -> Sphere065
  Tool = -> Sphere064
FEATURE [Part::Sphere] Sphere066
  Angle1 = -90
  Angle2 = 90
  Angle3 = 360
  AttacherType = Attacher::AttachEngine3D
  Placement = pos=(-7.5,34,0.5) rot=(0,0,1;0rad)
  Radius = 1.5
FEATURE [Part::Fuse] Fusion071  label="Holes004"
  Base = -> Sphere063
  Tool = -> Sphere066
FEATURE [Part::Box] Box203  label="Re-level Edge Clip Block009"
  AttacherType = Attacher::AttachEngine3D
  Height = 10
  Length = 12
  Placement = pos=(-21.5,-2,-7) rot=(0,0,1;0rad)
  Width = 44
FEATURE [Part::Box] Box204  label="Cube175"
  AttacherType = Attacher::AttachEngine3D
  Height = 7
  Length = 4
  Placement = pos=(-6,36.6,-2) rot=(0,0,1;0rad)
  Width = 1
FEATURE [Part::MultiFuse] Fusion074  label="Extra Holes for Clips004"
  Shapes = -> [Box199,Box198,Box204,Box201,Box200,Box197]
FEATURE [Part::Box] Box205  label="Cube176"
  AttacherType = Attacher::AttachEngine3D
  Height = 7
  Length = 10
  Placement = pos=(-15,34.6,-2) rot=(0,0,1;0rad)
  Width = 2
FEATURE [Part::MultiFuse] Fusion072
  Shapes = -> [Box196,Box192,Box195,Box202,Box205]
FEATURE [Part::Fuse] Fusion075
  Base = -> Fusion073
  Tool = -> Fusion072
FEATURE [Part::Cut] Cut075
  Base = -> Fusion075
  Tool = -> Fusion071
FEATURE [Part::Cut] Cut076
  Base = -> Cut075
  Tool = -> Fusion074
FEATURE [Part::Cut] Cut078
  Base = -> Cut076
  Tool = -> Box194
FEATURE [Part::Cut] Cut077
  Base = -> Cut078
  Tool = -> Box203
FEATURE [Part::Cut] Cut079  label="Edge Clips003"
  Base = -> Cut077
  Placement = pos=(-20,20,0) rot=(0,0,-1;1.5708rad)
  Tool = -> Box193
FEATURE [Part::MultiFuse] Fusion076  label="Edge Clips Fusion"
  Shapes = -> [Cut059,Cut069,Cut074,Cut079]
FEATURE [Part::Box] Box206  label="Cube177"
  AttacherType = Attacher::AttachEngine3D
  Height = 10
  Length = 10
  Placement = pos=(26,4,1) rot=(0.442189,-0.287968,0.849437;1.66134rad)
  Width = 15
FEATURE [Part::Box] Box207  label="Cube178"
  AttacherType = Attacher::AttachEngine3D
  Height = 10
  Length = 10
  Placement = pos=(-4,26,1) rot=(0.381439,0.080566,0.920876;3.07487rad)
  Width = 15
FEATURE [Part::Box] Box208  label="Cube179"
  AttacherType = Attacher::AttachEngine3D
  Height = 10
  Length = 10
  Placement = pos=(-26,-4,1) rot=(-0.273007,-0.419215,-0.865867;1.78566rad)
  Width = 15
FEATURE [Part::MultiFuse] Fusion078  label="Glue Dents"
  Shapes = -> [Box086,Box208,Box207,Box206]
FEATURE [Part::Box] Box209  label="Cube180"
  AttacherType = Attacher::AttachEngine3D
  Height = 7
  Length = 5
  Placement = pos=(-5,0,-2) rot=(0,0,1;0rad)
  Width = 40
FEATURE [Part::Box] Box210  label="Cube181"
  AttacherType = Attacher::AttachEngine3D
  Height = 7
  Length = 10
  Placement = pos=(-15,6,-2) rot=(0,0,1;0rad)
  Width = 2
FEATURE [Part::Box] Box211  label="Cube182"
  AttacherType = Attacher::AttachEngine3D
  Height = 7
  Length = 10
  Placement = pos=(-15,10,-2) rot=(0,0,1;0rad)
  Width = 2
FEATURE [Part::Box] Box212  label="Cube183"
  AttacherType = Attacher::AttachEngine3D
  Height = 7
  Length = 10
  Placement = pos=(-15,25.4,-2) rot=(0,0,1;0rad)
  Width = 2
FEATURE [Part::Box] Box213  label="Cube184"
  AttacherType = Attacher::AttachEngine3D
  Height = 7
  Length = 10
  Placement = pos=(-15,34.6,-2) rot=(0,0,1;0rad)
  Width = 2
FEATURE [Part::Sphere] Sphere067
  Angle1 = -90
  Angle2 = 90
  Angle3 = 360
  AttacherType = Attacher::AttachEngine3D
  Placement = pos=(-7.5,6.5,0.5) rot=(0,0,1;0rad)
  Radius = 1.25
FEATURE [Part::Box] Box214  label="Chamfer Cube005"
  AttacherType = Attacher::AttachEngine3D
  Height = 10
  Length = 13
  Placement = pos=(-11.69,0,-1.19) rot=(0,-1,0;0.785398rad)
  Width = 40
FEATURE [Part::Sphere] Sphere068
  Angle1 = -90
  Angle2 = 90
  Angle3 = 360
  AttacherType = Attacher::AttachEngine3D
  Placement = pos=(-7.5,11.5,0.5) rot=(0,0,1;0rad)
  Radius = 1.25
FEATURE [Part::Sphere] Sphere069
  Angle1 = -90
  Angle2 = 90
  Angle3 = 360
  AttacherType = Attacher::AttachEngine3D
  Placement = pos=(-7.5,28,0.5) rot=(0,0,1;0rad)
  Radius = 1.5
FEATURE [Part::Sphere] Sphere070
  Angle1 = -90
  Angle2 = 90
  Angle3 = 360
  AttacherType = Attacher::AttachEngine3D
  Placement = pos=(-7.5,34,0.5) rot=(0,0,1;0rad)
  Radius = 1.5
FEATURE [Part::Box] Box215  label="Cube185"
  AttacherType = Attacher::AttachEngine3D
  Height = 7
  Length = 4
  Placement = pos=(-6,5,-2) rot=(0,0,1;0rad)
  Width = 1
FEATURE [Part::Box] Box216  label="Cube186"
  AttacherType = Attacher::AttachEngine3D
  Height = 7
  Length = 4
  Placement = pos=(-6,8,-2) rot=(0,0,1;0rad)
  Width = 2
FEATURE [Part::Box] Box217  label="Cube187"
  AttacherType = Attacher::AttachEngine3D
  Height = 7
  Length = 4
  Placement = pos=(-6,12,-2) rot=(0,0,1;0rad)
  Width = 1
FEATURE [Part::Box] Box218  label="Cube188"
  AttacherType = Attacher::AttachEngine3D
  Height = 7
  Length = 4
  Placement = pos=(-6,24.4,-2) rot=(0,0,1;0rad)
  Width = 1
FEATURE [Part::Box] Box219  label="Cube189"
  AttacherType = Attacher::AttachEngine3D
  Height = 7
  Length = 4
  Placement = pos=(-6,36.6,-2) rot=(0,0,1;0rad)
  Width = 1
FEATURE [Part::Box] Box220  label="Cube190"
  AttacherType = Attacher::AttachEngine3D
  Height = 7
  Length = 4
  Placement = pos=(-6,27.4,-2) rot=(0,0,1;0rad)
  Width = 7.2
FEATURE [Part::MultiFuse] Fusion079  label="Extra Holes for Clips005"
  Shapes = -> [Box220,Box217,Box219,Box216,Box218,Box215]
FEATURE [Part::Box] Box221  label="Re-level Edge Clip Block010"
  AttacherType = Attacher::AttachEngine3D
  Height = 10
  Length = 20
  Placement = pos=(-19,-2,3) rot=(0,0,1;0rad)
  Width = 44
FEATURE [Part::Box] Box222  label="Re-level Edge Clip Block011"
  AttacherType = Attacher::AttachEngine3D
  Height = 10
  Length = 12
  Placement = pos=(-21.5,-2,-7) rot=(0,0,1;0rad)
  Width = 44
FEATURE [Part::Fuse] Fusion080  label="Bumps005"
  Base = -> Sphere067
  Tool = -> Sphere068
FEATURE [Part::Fuse] Fusion081  label="Holes005"
  Base = -> Sphere069
  Tool = -> Sphere070
FEATURE [Part::MultiFuse] Fusion082
  Shapes = -> [Box209,Box210,Box211,Box212,Box213]
FEATURE [Part::Fuse] Fusion083
  Base = -> Fusion080
  Tool = -> Fusion082
FEATURE [Part::Cut] Cut082
  Base = -> Fusion083
  Tool = -> Fusion081
FEATURE [Part::Cut] Cut083
  Base = -> Cut082
  Tool = -> Fusion079
FEATURE [Part::Cut] Cut084
  Base = -> Cut083
  Tool = -> Box221
FEATURE [Part::Cut] Cut085
  Base = -> Cut084
  Tool = -> Box222
FEATURE [Part::Cut] Cut086  label="Edge Clips Master001"
  Base = -> Cut085
  Placement = pos=(-20,-20,0) rot=(0,0,1;0rad)
  Tool = -> Box214
FEATURE [Part::Box] Box223  label="Cube191"
  AttacherType = Attacher::AttachEngine3D
  Height = 7
  Length = 5
  Placement = pos=(-5,0,-2) rot=(0,0,1;0rad)
  Width = 40
FEATURE [Part::Box] Box224  label="Cube192"
  AttacherType = Attacher::AttachEngine3D
  Height = 7
  Length = 4
  Placement = pos=(-6,8,-2) rot=(0,0,1;0rad)
  Width = 2
FEATURE [Part::Box] Box225  label="Chamfer Cube006"
  AttacherType = Attacher::AttachEngine3D
  Height = 10
  Length = 13
  Placement = pos=(-11.69,0,-1.19) rot=(0,-1,0;0.785398rad)
  Width = 40
FEATURE [Part::Box] Box226  label="Cube193"
  AttacherType = Attacher::AttachEngine3D
  Height = 7
  Length = 10
  Placement = pos=(-15,6,-2) rot=(0,0,1;0rad)
  Width = 2
FEATURE [Part::Sphere] Sphere071
  Angle1 = -90
  Angle2 = 90
  Angle3 = 360
  AttacherType = Attacher::AttachEngine3D
  Placement = pos=(-7.5,11.5,0.5) rot=(0,0,1;0rad)
  Radius = 1.25
FEATURE [Part::Box] Box227  label="Cube194"
  AttacherType = Attacher::AttachEngine3D
  Height = 7
  Length = 4
  Placement = pos=(-6,27.4,-2) rot=(0,0,1;0rad)
  Width = 7.2
FEATURE [Part::Box] Box228  label="Cube195"
  AttacherType = Attacher::AttachEngine3D
  Height = 7
  Length = 4
  Placement = pos=(-6,12,-2) rot=(0,0,1;0rad)
  Width = 1
FEATURE [Part::Box] Box229  label="Cube196"
  AttacherType = Attacher::AttachEngine3D
  Height = 7
  Length = 4
  Placement = pos=(-6,24.4,-2) rot=(0,0,1;0rad)
  Width = 1
FEATURE [Part::Sphere] Sphere072
  Angle1 = -90
  Angle2 = 90
  Angle3 = 360
  AttacherType = Attacher::AttachEngine3D
  Placement = pos=(-7.5,6.5,0.5) rot=(0,0,1;0rad)
  Radius = 1.25
FEATURE [Part::Box] Box230  label="Cube197"
  AttacherType = Attacher::AttachEngine3D
  Height = 7
  Length = 4
  Placement = pos=(-6,36.6,-2) rot=(0,0,1;0rad)
  Width = 1
FEATURE [Part::Box] Box231  label="Cube198"
  AttacherType = Attacher::AttachEngine3D
  Height = 7
  Length = 10
  Placement = pos=(-15,10,-2) rot=(0,0,1;0rad)
  Width = 2
FEATURE [Part::Sphere] Sphere073
  Angle1 = -90
  Angle2 = 90
  Angle3 = 360
  AttacherType = Attacher::AttachEngine3D
  Placement = pos=(-7.5,34,0.5) rot=(0,0,1;0rad)
  Radius = 1.5
FEATURE [Part::Box] Box232  label="Cube199"
  AttacherType = Attacher::AttachEngine3D
  Height = 7
  Length = 4
  Placement = pos=(-6,5,-2) rot=(0,0,1;0rad)
  Width = 1
FEATURE [Part::MultiFuse] Fusion085  label="Extra Holes for Clips006"
  Shapes = -> [Box227,Box228,Box230,Box224,Box229,Box232]
FEATURE [Part::Box] Box233  label="Re-level Edge Clip Block012"
  AttacherType = Attacher::AttachEngine3D
  Height = 10
  Length = 20
  Placement = pos=(-19,-2,3) rot=(0,0,1;0rad)
  Width = 44
FEATURE [Part::Box] Box234  label="Cube200"
  AttacherType = Attacher::AttachEngine3D
  Height = 7
  Length = 10
  Placement = pos=(-15,34.6,-2) rot=(0,0,1;0rad)
  Width = 2
FEATURE [Part::Box] Box235  label="Cube201"
  AttacherType = Attacher::AttachEngine3D
  Height = 7
  Length = 10
  Placement = pos=(-15,25.4,-2) rot=(0,0,1;0rad)
  Width = 2
FEATURE [Part::MultiFuse] Fusion086
  Shapes = -> [Box223,Box226,Box231,Box235,Box234]
FEATURE [Part::Fuse] Fusion087  label="Bumps006"
  Base = -> Sphere072
  Tool = -> Sphere071
FEATURE [Part::Fuse] Fusion084
  Base = -> Fusion087
  Tool = -> Fusion086
FEATURE [Part::Sphere] Sphere074
  Angle1 = -90
  Angle2 = 90
  Angle3 = 360
  AttacherType = Attacher::AttachEngine3D
  Placement = pos=(-7.5,28,0.5) rot=(0,0,1;0rad)
  Radius = 1.5
FEATURE [Part::Fuse] Fusion088  label="Holes006"
  Base = -> Sphere074
  Tool = -> Sphere073
FEATURE [Part::Box] Box236  label="Re-level Edge Clip Block013"
  AttacherType = Attacher::AttachEngine3D
  Height = 10
  Length = 12
  Placement = pos=(-21.5,-2,-7) rot=(0,0,1;0rad)
  Width = 44
FEATURE [Part::Cut] Cut087
  Base = -> Fusion084
  Tool = -> Fusion088
FEATURE [Part::Cut] Cut088
  Base = -> Cut087
  Tool = -> Fusion085
FEATURE [Part::Cut] Cut089
  Base = -> Cut088
  Tool = -> Box233
FEATURE [Part::Cut] Cut090
  Base = -> Cut089
  Tool = -> Box236
FEATURE [Part::Cut] Cut091  label="Edge Clips004"
  Base = -> Cut090
  Placement = pos=(20,-20,0) rot=(0,0,1;1.5708rad)
  Tool = -> Box225
FEATURE [Part::Box] Box237  label="Re-level Edge Clip Block014"
  AttacherType = Attacher::AttachEngine3D
  Height = 10
  Length = 12
  Placement = pos=(-21.5,-2,-7) rot=(0,0,1;0rad)
  Width = 44
FEATURE [Part::Box] Box238  label="Cube202"
  AttacherType = Attacher::AttachEngine3D
  Height = 7
  Length = 4
  Placement = pos=(-6,36.6,-2) rot=(0,0,1;0rad)
  Width = 1
FEATURE [Part::Box] Box239  label="Cube203"
  AttacherType = Attacher::AttachEngine3D
  Height = 7
  Length = 10
  Placement = pos=(-15,10,-2) rot=(0,0,1;0rad)
  Width = 2
FEATURE [Part::Box] Box240  label="Cube204"
  AttacherType = Attacher::AttachEngine3D
  Height = 7
  Length = 10
  Placement = pos=(-15,25.4,-2) rot=(0,0,1;0rad)
  Width = 2
FEATURE [Part::Box] Box241  label="Re-level Edge Clip Block015"
  AttacherType = Attacher::AttachEngine3D
  Height = 10
  Length = 20
  Placement = pos=(-19,-2,3) rot=(0,0,1;0rad)
  Width = 44
FEATURE [Part::Box] Box242  label="Cube205"
  AttacherType = Attacher::AttachEngine3D
  Height = 7
  Length = 10
  Placement = pos=(-15,34.6,-2) rot=(0,0,1;0rad)
  Width = 2
FEATURE [Part::Sphere] Sphere075
  Angle1 = -90
  Angle2 = 90
  Angle3 = 360
  AttacherType = Attacher::AttachEngine3D
  Placement = pos=(-7.5,34,0.5) rot=(0,0,1;0rad)
  Radius = 1.5
FEATURE [Part::Sphere] Sphere076
  Angle1 = -90
  Angle2 = 90
  Angle3 = 360
  AttacherType = Attacher::AttachEngine3D
  Placement = pos=(-7.5,28,0.5) rot=(0,0,1;0rad)
  Radius = 1.5
FEATURE [Part::Fuse] Fusion089  label="Holes007"
  Base = -> Sphere076
  Tool = -> Sphere075
FEATURE [Part::Box] Box243  label="Cube206"
  AttacherType = Attacher::AttachEngine3D
  Height = 7
  Length = 4
  Placement = pos=(-6,5,-2) rot=(0,0,1;0rad)
  Width = 1
FEATURE [Part::Box] Box244  label="Cube207"
  AttacherType = Attacher::AttachEngine3D
  Height = 7
  Length = 4
  Placement = pos=(-6,24.4,-2) rot=(0,0,1;0rad)
  Width = 1
FEATURE [Part::Sphere] Sphere077
  Angle1 = -90
  Angle2 = 90
  Angle3 = 360
  AttacherType = Attacher::AttachEngine3D
  Placement = pos=(-7.5,11.5,0.5) rot=(0,0,1;0rad)
  Radius = 1.25
FEATURE [Part::Box] Box245  label="Cube208"
  AttacherType = Attacher::AttachEngine3D
  Height = 7
  Length = 4
  Placement = pos=(-6,12,-2) rot=(0,0,1;0rad)
  Width = 1
FEATURE [Part::Box] Box246  label="Chamfer Cube007"
  AttacherType = Attacher::AttachEngine3D
  Height = 10
  Length = 13
  Placement = pos=(-11.69,0,-1.19) rot=(0,-1,0;0.785398rad)
  Width = 40
FEATURE [Part::Sphere] Sphere078
  Angle1 = -90
  Angle2 = 90
  Angle3 = 360
  AttacherType = Attacher::AttachEngine3D
  Placement = pos=(-7.5,6.5,0.5) rot=(0,0,1;0rad)
  Radius = 1.25
FEATURE [Part::Fuse] Fusion090  label="Bumps007"
  Base = -> Sphere078
  Tool = -> Sphere077
FEATURE [Part::Box] Box247  label="Cube209"
  AttacherType = Attacher::AttachEngine3D
  Height = 7
  Length = 5
  Placement = pos=(-5,0,-2) rot=(0,0,1;0rad)
  Width = 40
FEATURE [Part::Box] Box248  label="Cube210"
  AttacherType = Attacher::AttachEngine3D
  Height = 7
  Length = 4
  Placement = pos=(-6,27.4,-2) rot=(0,0,1;0rad)
  Width = 7.2
FEATURE [Part::Box] Box249  label="Cube211"
  AttacherType = Attacher::AttachEngine3D
  Height = 7
  Length = 4
  Placement = pos=(-6,8,-2) rot=(0,0,1;0rad)
  Width = 2
FEATURE [Part::MultiFuse] Fusion091  label="Extra Holes for Clips007"
  Shapes = -> [Box248,Box245,Box238,Box249,Box244,Box243]
FEATURE [Part::Box] Box250  label="Cube212"
  AttacherType = Attacher::AttachEngine3D
  Height = 7
  Length = 10
  Placement = pos=(-15,6,-2) rot=(0,0,1;0rad)
  Width = 2
FEATURE [Part::MultiFuse] Fusion092
  Shapes = -> [Box247,Box250,Box239,Box240,Box242]
FEATURE [Part::Fuse] Fusion093
  Base = -> Fusion090
  Tool = -> Fusion092
FEATURE [Part::Cut] Cut093
  Base = -> Fusion093
  Tool = -> Fusion089
FEATURE [Part::Cut] Cut094
  Base = -> Cut093
  Tool = -> Fusion091
FEATURE [Part::Cut] Cut095
  Base = -> Cut094
  Tool = -> Box241
FEATURE [Part::Cut] Cut096
  Base = -> Cut095
  Tool = -> Box237
FEATURE [Part::Cut] Cut092  label="Edge Clips005"
  Base = -> Cut096
  Placement = pos=(20,20,0) rot=(0,0,1;3.14159rad)
  Tool = -> Box246
FEATURE [Part::Box] Box251  label="Re-level Edge Clip Block016"
  AttacherType = Attacher::AttachEngine3D
  Height = 10
  Length = 12
  Placement = pos=(-21.5,-2,-7) rot=(0,0,1;0rad)
  Width = 44
FEATURE [Part::Box] Box252  label="Cube213"
  AttacherType = Attacher::AttachEngine3D
  Height = 7
  Length = 10
  Placement = pos=(-15,10,-2) rot=(0,0,1;0rad)
  Width = 2
FEATURE [Part::Box] Box253  label="Cube214"
  AttacherType = Attacher::AttachEngine3D
  Height = 7
  Length = 4
  Placement = pos=(-6,12,-2) rot=(0,0,1;0rad)
  Width = 1
FEATURE [Part::Box] Box254  label="Chamfer Cube008"
  AttacherType = Attacher::AttachEngine3D
  Height = 10
  Length = 13
  Placement = pos=(-11.69,0,-1.19) rot=(0,-1,0;0.785398rad)
  Width = 40
FEATURE [Part::Sphere] Sphere079
  Angle1 = -90
  Angle2 = 90
  Angle3 = 360
  AttacherType = Attacher::AttachEngine3D
  Placement = pos=(-7.5,6.5,0.5) rot=(0,0,1;0rad)
  Radius = 1.25
FEATURE [Part::Box] Box255  label="Cube215"
  AttacherType = Attacher::AttachEngine3D
  Height = 7
  Length = 5
  Placement = pos=(-5,0,-2) rot=(0,0,1;0rad)
  Width = 40
FEATURE [Part::Box] Box256  label="Cube216"
  AttacherType = Attacher::AttachEngine3D
  Height = 7
  Length = 4
  Placement = pos=(-6,27.4,-2) rot=(0,0,1;0rad)
  Width = 7.2
FEATURE [Part::Box] Box257  label="Cube217"
  AttacherType = Attacher::AttachEngine3D
  Height = 7
  Length = 4
  Placement = pos=(-6,8,-2) rot=(0,0,1;0rad)
  Width = 2
FEATURE [Part::Box] Box258  label="Cube218"
  AttacherType = Attacher::AttachEngine3D
  Height = 7
  Length = 10
  Placement = pos=(-15,6,-2) rot=(0,0,1;0rad)
  Width = 2
FEATURE [Part::Sphere] Sphere080
  Angle1 = -90
  Angle2 = 90
  Angle3 = 360
  AttacherType = Attacher::AttachEngine3D
  Placement = pos=(-7.5,28,0.5) rot=(0,0,1;0rad)
  Radius = 1.5
FEATURE [Part::Box] Box259  label="Cube219"
  AttacherType = Attacher::AttachEngine3D
  Height = 7
  Length = 4
  Placement = pos=(-6,5,-2) rot=(0,0,1;0rad)
  Width = 1
FEATURE [Part::Box] Box260  label="Cube220"
  AttacherType = Attacher::AttachEngine3D
  Height = 7
  Length = 4
  Placement = pos=(-6,24.4,-2) rot=(0,0,1;0rad)
  Width = 1
FEATURE [Part::Sphere] Sphere081
  Angle1 = -90
  Angle2 = 90
  Angle3 = 360
  AttacherType = Attacher::AttachEngine3D
  Placement = pos=(-7.5,11.5,0.5) rot=(0,0,1;0rad)
  Radius = 1.25
FEATURE [Part::Box] Box261  label="Re-level Edge Clip Block017"
  AttacherType = Attacher::AttachEngine3D
  Height = 10
  Length = 20
  Placement = pos=(-19,-2,3) rot=(0,0,1;0rad)
  Width = 44
FEATURE [Part::Box] Box262  label="Cube221"
  AttacherType = Attacher::AttachEngine3D
  Height = 7
  Length = 10
  Placement = pos=(-15,34.6,-2) rot=(0,0,1;0rad)
  Width = 2
FEATURE [Part::Box] Box263  label="Cube222"
  AttacherType = Attacher::AttachEngine3D
  Height = 7
  Length = 10
  Placement = pos=(-15,25.4,-2) rot=(0,0,1;0rad)
  Width = 2
FEATURE [Part::MultiFuse] Fusion096
  Shapes = -> [Box255,Box258,Box252,Box263,Box262]
FEATURE [Part::Box] Box264  label="Cube223"
  AttacherType = Attacher::AttachEngine3D
  Height = 7
  Length = 4
  Placement = pos=(-6,36.6,-2) rot=(0,0,1;0rad)
  Width = 1
FEATURE [Part::MultiFuse] Fusion095  label="Extra Holes for Clips008"
  Shapes = -> [Box256,Box253,Box264,Box257,Box260,Box259]
FEATURE [Part::Fuse] Fusion098  label="Bumps008"
  Base = -> Sphere079
  Tool = -> Sphere081
FEATURE [Part::Fuse] Fusion094
  Base = -> Fusion098
  Tool = -> Fusion096
FEATURE [Part::Sphere] Sphere082
  Angle1 = -90
  Angle2 = 90
  Angle3 = 360
  AttacherType = Attacher::AttachEngine3D
  Placement = pos=(-7.5,34,0.5) rot=(0,0,1;0rad)
  Radius = 1.5
FEATURE [Part::Fuse] Fusion097  label="Holes008"
  Base = -> Sphere080
  Tool = -> Sphere082
FEATURE [Part::Cut] Cut101
  Base = -> Fusion094
  Tool = -> Fusion097
FEATURE [Part::Cut] Cut097
  Base = -> Cut101
  Tool = -> Fusion095
FEATURE [Part::Cut] Cut098
  Base = -> Cut097
  Tool = -> Box261
FEATURE [Part::Cut] Cut099
  Base = -> Cut098
  Tool = -> Box251
FEATURE [Part::Cut] Cut100  label="Edge Clips006"
  Base = -> Cut099
  Placement = pos=(-20,20,0) rot=(0,0,-1;1.5708rad)
  Tool = -> Box254
FEATURE [Part::Box] Box265  label="Cube224"
  AttacherType = Attacher::AttachEngine3D
  Height = 10
  Length = 10
  Placement = pos=(4,-26,1) rot=(0.205904,-0.974848,-0.085288;0.803573rad)
  Width = 15
FEATURE [Part::Box] Box266  label="Cube225"
  AttacherType = Attacher::AttachEngine3D
  Height = 10
  Length = 10
  Placement = pos=(-26,-4,1) rot=(-0.273007,-0.419215,-0.865867;1.78566rad)
  Width = 15
FEATURE [Part::Box] Box267  label="Cube226"
  AttacherType = Attacher::AttachEngine3D
  Height = 10
  Length = 10
  Placement = pos=(-4,26,1) rot=(0.381439,0.080566,0.920876;3.07487rad)
  Width = 15
FEATURE [Part::Box] Box268  label="Cube227"
  AttacherType = Attacher::AttachEngine3D
  Height = 10
  Length = 10
  Placement = pos=(26,4,1) rot=(0.442189,-0.287968,0.849437;1.66134rad)
  Width = 15
FEATURE [Part::MultiFuse] Fusion099  label="Glue Dents001"
  Shapes = -> [Box265,Box266,Box267,Box268]
FEATURE [Part::MultiFuse] Fusion100  label="Edge Clips Fusion001"
  Shapes = -> [Cut100,Cut086,Cut091,Cut092]
FEATURE [Drawing::FeatureViewAnnotation] Annotation001
  Font = Sans
  Rotation = 0
  Scale = 7
  Text = 0.5 rejigged whole thing, stopped clips overhang and moved bump and holes back 0.5
  ViewResult = <g transform="translate(14,30) rotate(0)">\n<text id="Annotation001"\n font-family="Sans"\n font-size="7"\n fill="#000000">\n<tspan x="0" dy="1em">0.5 rejigged whole thing, stopped clips overhang and moved bump and holes back 0.5</tspan>\n</text>\n</g>
  Visible = false
  X = 14
  Y = 30
FEATURE [Part::Cylinder] Cylinder027  label="z-axis"
  Angle = 360
  AttacherType = Attacher::AttachEngine3D
  Height = 73
  Placement = pos=(0,0,-18) rot=(0,0,1;0rad)
  Radius = 0.5
FEATURE [Part::MultiFuse] Fusion101
  Placement = pos=(-15,-15,0) rot=(0,0,1;0rad)
  Shapes = -> [Box069,Cylinder018,Sphere030]
FEATURE [Part::Box] Box269  label="Square Nut Hole 024"
  AttacherType = Attacher::AttachEngine3D
  Height = 2
  Length = 5.8
  Placement = pos=(-2.9,2.9,2.1) rot=(1,0,0;3.14159rad)
  Width = 5.8
FEATURE [Part::Cylinder] Cylinder028
  Angle = 360
  AttacherType = Attacher::AttachEngine3D
  Height = 10
  Placement = pos=(0,0,6.7) rot=(1,0,0;3.14159rad)
  Radius = 1.7
FEATURE [Part::Sphere] Sphere083
  Angle1 = -90
  Angle2 = 90
  Angle3 = 360
  AttacherType = Attacher::AttachEngine3D
  Placement = pos=(0,0,4.3) rot=(1,0,0;3.14159rad)
  Radius = 3.35
FEATURE [Part::MultiFuse] Fusion102
  Placement = pos=(-15,0,0) rot=(0,0,1;0rad)
  Shapes = -> [Box269,Cylinder028,Sphere083]
FEATURE [Part::Fuse] Fusion103
  Base = -> Fusion101
  Tool = -> Fusion102
FEATURE [Part::Feature] Fusion103001
  Placement = pos=(0,0,0) rot=(0,0,1;1.5708rad)
  shape: bbox 21.7 x 6.7 x 10.95 mm, 18 faces, 2 solids (baked)
FEATURE [Part::Feature] Fusion103002
  Placement = pos=(0,0,0) rot=(0,0,1;3.14159rad)
  shape: bbox 6.7 x 21.7 x 10.95 mm, 18 faces, 2 solids (baked)
FEATURE [Part::Feature] Fusion103003
  Placement = pos=(0,0,0) rot=(0,0,-1;1.5708rad)
  shape: bbox 21.7 x 6.7 x 10.95 mm, 18 faces, 2 solids (baked)
FEATURE [Part::MultiFuse] Fusion103004  label="Nut Holes"
  Shapes = -> [Fusion103,Fusion103001,Fusion103002,Fusion103003]
FEATURE [Part::Fuse] Fusion103005  label="Cube with Edge Clips"
  Base = -> Box075
  Tool = -> Fusion100
FEATURE [Part::Cut] Cut102
  Base = -> Fusion103005
  Tool = -> Fusion099
FEATURE [Part::Cut] Cut103
  Base = -> Cut102
  Tool = -> Fusion103004
FEATURE [Part::Cut] Cut104
  Base = -> Cut103
  Tool = -> Chamfer014
FEATURE [Part::Cut] Cut105
  Base = -> Cut104
  Tool = -> Chamfer013
FEATURE [Part::Cut] Cut106  label="Nut Plate 1.1"
  Base = -> Cut105
  Tool = -> Box145
FEATURE [Part::Fuse] Fusion103006
  Base = -> Cut047
  Tool = -> Fusion076
FEATURE [Part::Cut] Cut107
  Base = -> Fusion103006
  Tool = -> Fusion052
FEATURE [Part::Cut] Cut108
  Base = -> Cut107
  Tool = -> Chamfer008
FEATURE [Part::Cut] Cut109
  Base = -> Cut108
  Tool = -> Box085
FEATURE [Part::Cut] Cut110  label="Ball Plate 1.1"
  Base = -> Cut109
  Tool = -> Fusion078
FEATURE [Drawing::FeatureViewAnnotation] Annotation002
  Font = Sans
  Rotation = 0
  Scale = 7
  ViewResult = <g transform="translate(10,10) rotate(0)">\n<text id="Annotation002"\n font-family="Sans"\n font-size="7"\n fill="#000000">\n<tspan x="0" dy="1em"></tspan>\n</text>\n</g>
  Visible = true
  X = 10
  Y = 10
FEATURE [Drawing::FeatureViewAnnotation] Annotation003
  Font = Sans
  Rotation = 0
  Scale = 7
  Text = Robot 0.X
  ViewResult = <g transform="translate(14,18) rotate(0)">\n<text id="Annotation003"\n font-family="Sans"\n font-size="7"\n fill="#000000">\n<tspan x="0" dy="1em">Robot 0.X</tspan>\n</text>\n</g>
  Visible = true
  X = 14
  Y = 18
FEATURE [Drawing::FeatureViewAnnotation] Annotation004
  Font = Sans
  Rotation = 0
  Scale = 7
  ViewResult = <g transform="translate(10,10) rotate(0)">\n<text id="Annotation004"\n font-family="Sans"\n font-size="7"\n fill="#000000">\n<tspan x="0" dy="1em"></tspan>\n</text>\n</g>
  Visible = true
  X = 10
  Y = 10
FEATURE [Drawing::FeatureViewAnnotation] Annotation005
  Font = Sans
  Rotation = 0
  Scale = 5
  Text = Robot 0.1 - AB added Gripper Mecanism to SB\'s Plates
  ViewResult = <g transform="translate(10,30) rotate(0)">\n<text id="Annotation005"\n font-family="Sans"\n font-size="5"\n fill="#000000">\n<tspan x="0" dy="1em">Robot 0.1 - AB added Gripper Mecanism to SB\'s Plates</tspan>\n</text>\n</g>
  Visible = true
  X = 10
  Y = 30
FEATURE [Drawing::FeatureViewAnnotation] Annotation006
  Font = Sans
  Rotation = 0
  Scale = 5
  Text = Robot 0.2 - Reduced tooth size on small gear
  ViewResult = <g transform="translate(10,40) rotate(0)">\n<text id="Annotation006"\n font-family="Sans"\n font-size="5"\n fill="#000000">\n<tspan x="0" dy="1em">Robot 0.2 - Reduced tooth size on small gear</tspan>\n<tspan x="0" dy="1em"></tspan>\n</text>\n</g>
  Visible = true
  X = 10
  Y = 40
FEATURE [Part::Cylinder] Cylinder029
  Angle = 360
  AttacherType = Attacher::AttachEngine3D
  Height = 10
  Placement = pos=(15,-15,-5) rot=(0,0,1;1.5708rad)
  Radius = 1.7
FEATURE [Part::Sphere] Sphere084  label="Mag Hole001"
  Angle1 = -90
  Angle2 = 90
  Angle3 = 360
  AttacherType = Attacher::AttachEngine3D
  Placement = pos=(15,-15,1.7) rot=(0,0,1;1.5708rad)
  Radius = 2.83
FEATURE [Part::Sphere] Sphere085  label="Mag Hole002"
  Angle1 = -90
  Angle2 = 90
  Angle3 = 360
  AttacherType = Attacher::AttachEngine3D
  Placement = pos=(15,15,1.7) rot=(0,0,1;3.14159rad)
  Radius = 2.83
FEATURE [Part::Sphere] Sphere086  label="Mag Hole 004"
  Angle1 = -90
  Angle2 = 90
  Angle3 = 360
  AttacherType = Attacher::AttachEngine3D
  Placement = pos=(3e-15,15,1.7) rot=(0,0,1;1.5708rad)
  Radius = 2.825
FEATURE [Part::Sphere] Sphere087  label="Mag Hole 005"
  Angle1 = -90
  Angle2 = 90
  Angle3 = 360
  AttacherType = Attacher::AttachEngine3D
  Placement = pos=(-15,2e-15,1.7) rot=(0,0,1;3.14159rad)
  Radius = 2.825
FEATURE [Part::Sphere] Sphere088  label="Mag Hole 006"
  Angle1 = -90
  Angle2 = 90
  Angle3 = 360
  AttacherType = Attacher::AttachEngine3D
  Placement = pos=(-3e-15,-15,1.7) rot=(0,0,-1;1.5708rad)
  Radius = 2.825
FEATURE [Part::Cylinder] Cylinder030
  Angle = 360
  AttacherType = Attacher::AttachEngine3D
  Height = 10
  Placement = pos=(15,15,-5) rot=(0,0,1;3.14159rad)
  Radius = 1.7
FEATURE [Part::Cylinder] Cylinder031
  Angle = 360
  AttacherType = Attacher::AttachEngine3D
  Height = 10
  Placement = pos=(3e-15,15,-5) rot=(0,0,1;1.5708rad)
  Radius = 1.7
FEATURE [Part::Cylinder] Cylinder032
  Angle = 360
  AttacherType = Attacher::AttachEngine3D
  Height = 10
  Placement = pos=(-15,6e-15,-5) rot=(0,0,1;3.14159rad)
  Radius = 1.7
FEATURE [Part::Cylinder] Cylinder033
  Angle = 360
  AttacherType = Attacher::AttachEngine3D
  Height = 10
  Placement = pos=(-9e-15,-15,-5) rot=(0,0,-1;1.5708rad)
  Radius = 1.7
FEATURE [Part::MultiFuse] Fusion103007
  Shapes = -> [Cylinder029,Sphere087,Sphere084,Sphere086,Sphere088,Cylinder032,Cylinder033,Sphere085,Cylinder031,Cylinder030]
FEATURE [Part::Cut] Cut111  label="Ball Plate with Extra Holes"
  Base = -> Cut110
  Tool = -> Fusion103007
FEATURE [Part::Cylinder] Cylinder034
  Angle = 360
  AttacherType = Attacher::AttachEngine3D
  Height = 4
  Placement = pos=(-9.75,-9.75,-3) rot=(0,0,1;0rad)
  Radius = 1.5
FEATURE [Part::Cylinder] Cylinder035
  Angle = 360
  AttacherType = Attacher::AttachEngine3D
  Height = 4
  Placement = pos=(9.75,9.75,-3) rot=(0,0,1;0rad)
  Radius = 1.5
FEATURE [Part::Cylinder] Cylinder036
  Angle = 360
  AttacherType = Attacher::AttachEngine3D
  Height = 4
  Placement = pos=(-9.75,9.75,-3) rot=(0,0,1;0rad)
  Radius = 1.5
FEATURE [Part::Cylinder] Cylinder037
  Angle = 360
  AttacherType = Attacher::AttachEngine3D
  Height = 4
  Placement = pos=(9.75,-9.75,-3) rot=(0,0,1;0rad)
  Radius = 1.5
FEATURE [Part::MultiFuse] Fusion103008
  Shapes = -> [Cylinder034,Cylinder037,Cylinder036,Cylinder035]
FEATURE [Part::Cut] Cut112  label="Ball Plate 1.2"
  Base = -> Cut111
  Tool = -> Fusion103008
FEATURE [Part::Cylinder] Cylinder038
  Angle = 360
  AttacherType = Attacher::AttachEngine3D
  Height = 4
  Placement = pos=(-9.75,-9.75,-3) rot=(0,0,1;0rad)
  Radius = 1.5
FEATURE [Part::Cylinder] Cylinder039
  Angle = 360
  AttacherType = Attacher::AttachEngine3D
  Height = 4
  Placement = pos=(9.75,-9.75,-3) rot=(0,0,1;0rad)
  Radius = 1.5
FEATURE [Part::Cylinder] Cylinder040
  Angle = 360
  AttacherType = Attacher::AttachEngine3D
  Height = 4
  Placement = pos=(-9.75,9.75,-3) rot=(0,0,1;0rad)
  Radius = 1.5
FEATURE [Part::Cylinder] Cylinder041
  Angle = 360
  AttacherType = Attacher::AttachEngine3D
  Height = 4
  Placement = pos=(9.75,9.75,-3) rot=(0,0,1;0rad)
  Radius = 1.5
FEATURE [Part::MultiFuse] Fusion103009
  Shapes = -> [Cylinder038,Cylinder041,Cylinder039,Cylinder040]
FEATURE [Part::Cut] Cut113  label="Nut Plate 1.2"
  Base = -> Cut106
  Tool = -> Fusion103009
FEATURE [Drawing::FeatureViewAnnotation] Annotation007
  Font = Sans
  Rotation = 0
  Scale = 7
  ViewResult = <g transform="translate(10,10) rotate(0)">\n<text id="Annotation007"\n font-family="Sans"\n font-size="7"\n fill="#000000">\n<tspan x="0" dy="1em"></tspan>\n</text>\n</g>
  Visible = true
  X = 10
  Y = 10
FEATURE [Drawing::FeatureViewAnnotation] Annotation008
  Font = Sans
  Rotation = 0
  Scale = 7
  ViewResult = <g transform="translate(10,10) rotate(0)">\n<text id="Annotation008"\n font-family="Sans"\n font-size="7"\n fill="#000000">\n<tspan x="0" dy="1em"></tspan>\n</text>\n</g>
  Visible = true
  X = 10
  Y = 10
FEATURE [Drawing::FeatureViewAnnotation] Annotation009
  Font = Sans
  Rotation = 0
  Scale = 5
  Text = Robot 0.3 Reduced size of tooth on big gear and added boss. Rotated 180
  ViewResult = <g transform="translate(10,50) rotate(0)">\n<text id="Annotation009"\n font-family="Sans"\n font-size="5"\n fill="#000000">\n<tspan x="0" dy="1em">Robot 0.3 Reduced size of tooth on big gear and added boss. Rotated 180</tspan>\n<tspan x="0" dy="1em"></tspan>\n<tspan x="0" dy="1em"></tspan>\n</text>\n</g>
  Visible = true
  X = 10
  Y = 50
FEATURE [Part::Feature] Fusion103010
  Placement = pos=(0,0,0) rot=(0,0,-1;1.5708rad)
  shape: bbox 21.7 x 6.7 x 10.95 mm, 18 faces, 2 solids (baked)
FEATURE [Part::Feature] Fusion103011
  Placement = pos=(0,0,0) rot=(0,0,1;3.14159rad)
  shape: bbox 6.7 x 21.7 x 10.95 mm, 18 faces, 2 solids (baked)
FEATURE [Part::Feature] Fusion103012
  Placement = pos=(0,0,0) rot=(0,0,1;1.5708rad)
  shape: bbox 21.7 x 6.7 x 10.95 mm, 18 faces, 2 solids (baked)
FEATURE [Part::Box] Box270  label="Square Nut Hole 025"
  AttacherType = Attacher::AttachEngine3D
  Height = 2
  Length = 5.8
  Placement = pos=(-2.9,2.9,2.1) rot=(1,0,0;3.14159rad)
  Width = 5.8
FEATURE [Part::Cylinder] Cylinder042
  Angle = 360
  AttacherType = Attacher::AttachEngine3D
  Height = 10
  Placement = pos=(0,0,6.7) rot=(1,0,0;3.14159rad)
  Radius = 1.7
FEATURE [Part::Box] Box271  label="Cube228"
  AttacherType = Attacher::AttachEngine3D
  Height = 5
  Length = 40
  Placement = pos=(-20,-20,-2) rot=(0,0,1;0rad)
  Width = 40
FEATURE [Part::Sphere] Sphere089
  Angle1 = -90
  Angle2 = 90
  Angle3 = 360
  AttacherType = Attacher::AttachEngine3D
  Placement = pos=(0,0,4.3) rot=(1,0,0;3.14159rad)
  Radius = 3.35
FEATURE [Part::Box] Box272  label="Cube229"
  AttacherType = Attacher::AttachEngine3D
  Height = 15
  Length = 19.5
  Placement = pos=(-9.75,-9.75,-14) rot=(0,0,1;0rad)
  Width = 19.5
FEATURE [Part::Box] Box273  label="Cube230"
  AttacherType = Attacher::AttachEngine3D
  Height = 15
  Length = 19.5
  Placement = pos=(-9.75,-9.75,-3) rot=(0,0,1;0rad)
  Width = 19.5
FEATURE [Part::Chamfer] Chamfer015  label="Octagon001"
  Base = -> Box273
  Edges = 4 edges r=4: [Edge1,Edge3,Edge5,Edge7]
FEATURE [Part::Box] Box274  label="Cube231"
  AttacherType = Attacher::AttachEngine3D
  Height = 10
  Length = 24
  Placement = pos=(-12,-12,2.1) rot=(0,0,1;0rad)
  Width = 24
FEATURE [Part::Box] Box275  label="Cube232"
  AttacherType = Attacher::AttachEngine3D
  Height = 14
  Length = 20
  Placement = pos=(-10,-10,0) rot=(0,0,1;0rad)
  Width = 20
FEATURE [Part::Cut] Cut116
  Base = -> Box274
  Tool = -> Box275
FEATURE [Part::Chamfer] Chamfer016  label="Glue Channel001"
  Base = -> Cut116
  Edges = 8 edges r=0.95: [Edge4,Edge5,Edge14,Edge16,Edge17,Edge18,Edge19,Edge20]
FEATURE [Part::Box] Box276  label="Cube233"
  AttacherType = Attacher::AttachEngine3D
  Height = 7
  Length = 5
  Placement = pos=(-5,0,-2) rot=(0,0,1;0rad)
  Width = 40
FEATURE [Part::Box] Box277  label="Cube234"
  AttacherType = Attacher::AttachEngine3D
  Height = 7
  Length = 10
  Placement = pos=(-15,6,-2) rot=(0,0,1;0rad)
  Width = 2
FEATURE [Part::Box] Box278  label="Cube235"
  AttacherType = Attacher::AttachEngine3D
  Height = 7
  Length = 10
  Placement = pos=(-15,10,-2) rot=(0,0,1;0rad)
  Width = 2
FEATURE [Part::Box] Box279  label="Cube236"
  AttacherType = Attacher::AttachEngine3D
  Height = 7
  Length = 10
  Placement = pos=(-15,25.4,-2) rot=(0,0,1;0rad)
  Width = 2
FEATURE [Part::Box] Box280  label="Cube237"
  AttacherType = Attacher::AttachEngine3D
  Height = 7
  Length = 10
  Placement = pos=(-15,34.6,-2) rot=(0,0,1;0rad)
  Width = 2
FEATURE [Part::Sphere] Sphere090
  Angle1 = -90
  Angle2 = 90
  Angle3 = 360
  AttacherType = Attacher::AttachEngine3D
  Placement = pos=(-7.5,6.5,0.5) rot=(0,0,1;0rad)
  Radius = 1.25
FEATURE [Part::Box] Box281  label="Chamfer Cube009"
  AttacherType = Attacher::AttachEngine3D
  Height = 10
  Length = 13
  Placement = pos=(-11.69,0,-1.19) rot=(0,-1,0;0.785398rad)
  Width = 40
FEATURE [Part::Sphere] Sphere091
  Angle1 = -90
  Angle2 = 90
  Angle3 = 360
  AttacherType = Attacher::AttachEngine3D
  Placement = pos=(-7.5,11.5,0.5) rot=(0,0,1;0rad)
  Radius = 1.25
FEATURE [Part::Sphere] Sphere092
  Angle1 = -90
  Angle2 = 90
  Angle3 = 360
  AttacherType = Attacher::AttachEngine3D
  Placement = pos=(-7.5,28,0.5) rot=(0,0,1;0rad)
  Radius = 1.5
FEATURE [Part::Sphere] Sphere093
  Angle1 = -90
  Angle2 = 90
  Angle3 = 360
  AttacherType = Attacher::AttachEngine3D
  Placement = pos=(-7.5,34,0.5) rot=(0,0,1;0rad)
  Radius = 1.5
FEATURE [Part::Box] Box282  label="Cube238"
  AttacherType = Attacher::AttachEngine3D
  Height = 7
  Length = 4
  Placement = pos=(-6,5,-2) rot=(0,0,1;0rad)
  Width = 1
FEATURE [Part::Box] Box283  label="Cube239"
  AttacherType = Attacher::AttachEngine3D
  Height = 7
  Length = 4
  Placement = pos=(-6,8,-2) rot=(0,0,1;0rad)
  Width = 2
FEATURE [Part::Box] Box284  label="Cube240"
  AttacherType = Attacher::AttachEngine3D
  Height = 7
  Length = 4
  Placement = pos=(-6,12,-2) rot=(0,0,1;0rad)
  Width = 1
FEATURE [Part::Box] Box285  label="Cube241"
  AttacherType = Attacher::AttachEngine3D
  Height = 7
  Length = 4
  Placement = pos=(-6,24.4,-2) rot=(0,0,1;0rad)
  Width = 1
FEATURE [Part::Box] Box286  label="Cube242"
  AttacherType = Attacher::AttachEngine3D
  Height = 7
  Length = 4
  Placement = pos=(-6,36.6,-2) rot=(0,0,1;0rad)
  Width = 1
FEATURE [Part::Box] Box287  label="Cube243"
  AttacherType = Attacher::AttachEngine3D
  Height = 7
  Length = 4
  Placement = pos=(-6,27.4,-2) rot=(0,0,1;0rad)
  Width = 7.2
FEATURE [Part::MultiFuse] Fusion103013  label="Extra Holes for Clips009"
  Shapes = -> [Box287,Box284,Box286,Box283,Box285,Box282]
FEATURE [Part::Box] Box288  label="Re-level Edge Clip Block018"
  AttacherType = Attacher::AttachEngine3D
  Height = 10
  Length = 20
  Placement = pos=(-19,-2,3) rot=(0,0,1;0rad)
  Width = 44
FEATURE [Part::Box] Box289  label="Re-level Edge Clip Block019"
  AttacherType = Attacher::AttachEngine3D
  Height = 10
  Length = 12
  Placement = pos=(-21.5,-2,-7) rot=(0,0,1;0rad)
  Width = 44
FEATURE [Part::Fuse] Fusion103014  label="Bumps009"
  Base = -> Sphere090
  Tool = -> Sphere091
FEATURE [Part::Fuse] Fusion103015  label="Holes009"
  Base = -> Sphere092
  Tool = -> Sphere093
FEATURE [Part::MultiFuse] Fusion103016
  Shapes = -> [Box276,Box277,Box278,Box279,Box280]
FEATURE [Part::Fuse] Fusion103017
  Base = -> Fusion103014
  Tool = -> Fusion103016
FEATURE [Part::Cut] Cut117
  Base = -> Fusion103017
  Tool = -> Fusion103015
FEATURE [Part::Cut] Cut118
  Base = -> Cut117
  Tool = -> Fusion103013
FEATURE [Part::Cut] Cut119
  Base = -> Cut118
  Tool = -> Box288
FEATURE [Part::Cut] Cut120
  Base = -> Cut119
  Tool = -> Box289
FEATURE [Part::Cut] Cut121  label="Edge Clips Master002"
  Base = -> Cut120
  Placement = pos=(-20,-20,0) rot=(0,0,1;0rad)
  Tool = -> Box281
FEATURE [Part::Box] Box290  label="Cube244"
  AttacherType = Attacher::AttachEngine3D
  Height = 7
  Length = 5
  Placement = pos=(-5,0,-2) rot=(0,0,1;0rad)
  Width = 40
FEATURE [Part::Box] Box291  label="Cube245"
  AttacherType = Attacher::AttachEngine3D
  Height = 7
  Length = 4
  Placement = pos=(-6,8,-2) rot=(0,0,1;0rad)
  Width = 2
FEATURE [Part::Box] Box292  label="Chamfer Cube010"
  AttacherType = Attacher::AttachEngine3D
  Height = 10
  Length = 13
  Placement = pos=(-11.69,0,-1.19) rot=(0,-1,0;0.785398rad)
  Width = 40
FEATURE [Part::Box] Box293  label="Cube246"
  AttacherType = Attacher::AttachEngine3D
  Height = 7
  Length = 10
  Placement = pos=(-15,6,-2) rot=(0,0,1;0rad)
  Width = 2
FEATURE [Part::Sphere] Sphere094
  Angle1 = -90
  Angle2 = 90
  Angle3 = 360
  AttacherType = Attacher::AttachEngine3D
  Placement = pos=(-7.5,11.5,0.5) rot=(0,0,1;0rad)
  Radius = 1.25
FEATURE [Part::Box] Box294  label="Cube247"
  AttacherType = Attacher::AttachEngine3D
  Height = 7
  Length = 4
  Placement = pos=(-6,27.4,-2) rot=(0,0,1;0rad)
  Width = 7.2
FEATURE [Part::Box] Box295  label="Cube248"
  AttacherType = Attacher::AttachEngine3D
  Height = 7
  Length = 4
  Placement = pos=(-6,12,-2) rot=(0,0,1;0rad)
  Width = 1
FEATURE [Part::Box] Box296  label="Cube249"
  AttacherType = Attacher::AttachEngine3D
  Height = 7
  Length = 4
  Placement = pos=(-6,24.4,-2) rot=(0,0,1;0rad)
  Width = 1
FEATURE [Part::Sphere] Sphere095
  Angle1 = -90
  Angle2 = 90
  Angle3 = 360
  AttacherType = Attacher::AttachEngine3D
  Placement = pos=(-7.5,6.5,0.5) rot=(0,0,1;0rad)
  Radius = 1.25
FEATURE [Part::Box] Box297  label="Cube250"
  AttacherType = Attacher::AttachEngine3D
  Height = 7
  Length = 4
  Placement = pos=(-6,36.6,-2) rot=(0,0,1;0rad)
  Width = 1
FEATURE [Part::Box] Box298  label="Cube251"
  AttacherType = Attacher::AttachEngine3D
  Height = 7
  Length = 10
  Placement = pos=(-15,10,-2) rot=(0,0,1;0rad)
  Width = 2
FEATURE [Part::Sphere] Sphere096
  Angle1 = -90
  Angle2 = 90
  Angle3 = 360
  AttacherType = Attacher::AttachEngine3D
  Placement = pos=(-7.5,34,0.5) rot=(0,0,1;0rad)
  Radius = 1.5
FEATURE [Part::Box] Box299  label="Cube252"
  AttacherType = Attacher::AttachEngine3D
  Height = 7
  Length = 4
  Placement = pos=(-6,5,-2) rot=(0,0,1;0rad)
  Width = 1
FEATURE [Part::MultiFuse] Fusion103019  label="Extra Holes for Clips010"
  Shapes = -> [Box294,Box295,Box297,Box291,Box296,Box299]
FEATURE [Part::Box] Box300  label="Re-level Edge Clip Block020"
  AttacherType = Attacher::AttachEngine3D
  Height = 10
  Length = 20
  Placement = pos=(-19,-2,3) rot=(0,0,1;0rad)
  Width = 44
FEATURE [Part::Box] Box301  label="Cube253"
  AttacherType = Attacher::AttachEngine3D
  Height = 7
  Length = 10
  Placement = pos=(-15,34.6,-2) rot=(0,0,1;0rad)
  Width = 2
FEATURE [Part::Box] Box302  label="Cube254"
  AttacherType = Attacher::AttachEngine3D
  Height = 7
  Length = 10
  Placement = pos=(-15,25.4,-2) rot=(0,0,1;0rad)
  Width = 2
FEATURE [Part::MultiFuse] Fusion103020
  Shapes = -> [Box290,Box293,Box298,Box302,Box301]
FEATURE [Part::Fuse] Fusion103021  label="Bumps010"
  Base = -> Sphere095
  Tool = -> Sphere094
FEATURE [Part::Fuse] Fusion103018
  Base = -> Fusion103021
  Tool = -> Fusion103020
FEATURE [Part::Sphere] Sphere097
  Angle1 = -90
  Angle2 = 90
  Angle3 = 360
  AttacherType = Attacher::AttachEngine3D
  Placement = pos=(-7.5,28,0.5) rot=(0,0,1;0rad)
  Radius = 1.5
FEATURE [Part::Fuse] Fusion103022  label="Holes010"
  Base = -> Sphere097
  Tool = -> Sphere096
FEATURE [Part::Box] Box303  label="Re-level Edge Clip Block021"
  AttacherType = Attacher::AttachEngine3D
  Height = 10
  Length = 12
  Placement = pos=(-21.5,-2,-7) rot=(0,0,1;0rad)
  Width = 44
FEATURE [Part::Cut] Cut122
  Base = -> Fusion103018
  Tool = -> Fusion103022
FEATURE [Part::Cut] Cut123
  Base = -> Cut122
  Tool = -> Fusion103019
FEATURE [Part::Cut] Cut124
  Base = -> Cut123
  Tool = -> Box300
FEATURE [Part::Cut] Cut125
  Base = -> Cut124
  Tool = -> Box303
FEATURE [Part::Cut] Cut126  label="Edge Clips007"
  Base = -> Cut125
  Placement = pos=(20,-20,0) rot=(0,0,1;1.5708rad)
  Tool = -> Box292
FEATURE [Part::Box] Box304  label="Re-level Edge Clip Block022"
  AttacherType = Attacher::AttachEngine3D
  Height = 10
  Length = 12
  Placement = pos=(-21.5,-2,-7) rot=(0,0,1;0rad)
  Width = 44
FEATURE [Part::Box] Box305  label="Cube255"
  AttacherType = Attacher::AttachEngine3D
  Height = 7
  Length = 4
  Placement = pos=(-6,36.6,-2) rot=(0,0,1;0rad)
  Width = 1
FEATURE [Part::Box] Box306  label="Cube256"
  AttacherType = Attacher::AttachEngine3D
  Height = 7
  Length = 10
  Placement = pos=(-15,10,-2) rot=(0,0,1;0rad)
  Width = 2
FEATURE [Part::Box] Box307  label="Cube257"
  AttacherType = Attacher::AttachEngine3D
  Height = 7
  Length = 10
  Placement = pos=(-15,25.4,-2) rot=(0,0,1;0rad)
  Width = 2
FEATURE [Part::Box] Box308  label="Re-level Edge Clip Block023"
  AttacherType = Attacher::AttachEngine3D
  Height = 10
  Length = 20
  Placement = pos=(-19,-2,3) rot=(0,0,1;0rad)
  Width = 44
FEATURE [Part::Box] Box309  label="Cube258"
  AttacherType = Attacher::AttachEngine3D
  Height = 7
  Length = 10
  Placement = pos=(-15,34.6,-2) rot=(0,0,1;0rad)
  Width = 2
FEATURE [Part::Sphere] Sphere098
  Angle1 = -90
  Angle2 = 90
  Angle3 = 360
  AttacherType = Attacher::AttachEngine3D
  Placement = pos=(-7.5,34,0.5) rot=(0,0,1;0rad)
  Radius = 1.5
FEATURE [Part::Sphere] Sphere099
  Angle1 = -90
  Angle2 = 90
  Angle3 = 360
  AttacherType = Attacher::AttachEngine3D
  Placement = pos=(-7.5,28,0.5) rot=(0,0,1;0rad)
  Radius = 1.5
FEATURE [Part::Fuse] Fusion103023  label="Holes011"
  Base = -> Sphere099
  Tool = -> Sphere098
FEATURE [Part::Box] Box310  label="Cube259"
  AttacherType = Attacher::AttachEngine3D
  Height = 7
  Length = 4
  Placement = pos=(-6,5,-2) rot=(0,0,1;0rad)
  Width = 1
FEATURE [Part::Box] Box311  label="Cube260"
  AttacherType = Attacher::AttachEngine3D
  Height = 7
  Length = 4
  Placement = pos=(-6,24.4,-2) rot=(0,0,1;0rad)
  Width = 1
FEATURE [Part::Sphere] Sphere100
  Angle1 = -90
  Angle2 = 90
  Angle3 = 360
  AttacherType = Attacher::AttachEngine3D
  Placement = pos=(-7.5,11.5,0.5) rot=(0,0,1;0rad)
  Radius = 1.25
FEATURE [Part::Box] Box312  label="Cube261"
  AttacherType = Attacher::AttachEngine3D
  Height = 7
  Length = 4
  Placement = pos=(-6,12,-2) rot=(0,0,1;0rad)
  Width = 1
FEATURE [Part::Box] Box313  label="Chamfer Cube011"
  AttacherType = Attacher::AttachEngine3D
  Height = 10
  Length = 13
  Placement = pos=(-11.69,0,-1.19) rot=(0,-1,0;0.785398rad)
  Width = 40
FEATURE [Part::Sphere] Sphere101
  Angle1 = -90
  Angle2 = 90
  Angle3 = 360
  AttacherType = Attacher::AttachEngine3D
  Placement = pos=(-7.5,6.5,0.5) rot=(0,0,1;0rad)
  Radius = 1.25
FEATURE [Part::Fuse] Fusion103024  label="Bumps011"
  Base = -> Sphere101
  Tool = -> Sphere100
FEATURE [Part::Box] Box314  label="Cube262"
  AttacherType = Attacher::AttachEngine3D
  Height = 7
  Length = 5
  Placement = pos=(-5,0,-2) rot=(0,0,1;0rad)
  Width = 40
FEATURE [Part::Box] Box315  label="Cube263"
  AttacherType = Attacher::AttachEngine3D
  Height = 7
  Length = 4
  Placement = pos=(-6,27.4,-2) rot=(0,0,1;0rad)
  Width = 7.2
FEATURE [Part::Box] Box316  label="Cube264"
  AttacherType = Attacher::AttachEngine3D
  Height = 7
  Length = 4
  Placement = pos=(-6,8,-2) rot=(0,0,1;0rad)
  Width = 2
FEATURE [Part::MultiFuse] Fusion103025  label="Extra Holes for Clips011"
  Shapes = -> [Box315,Box312,Box305,Box316,Box311,Box310]
FEATURE [Part::Box] Box317  label="Cube265"
  AttacherType = Attacher::AttachEngine3D
  Height = 7
  Length = 10
  Placement = pos=(-15,6,-2) rot=(0,0,1;0rad)
  Width = 2
FEATURE [Part::MultiFuse] Fusion103026
  Shapes = -> [Box314,Box317,Box306,Box307,Box309]
FEATURE [Part::Fuse] Fusion103027
  Base = -> Fusion103024
  Tool = -> Fusion103026
FEATURE [Part::Cut] Cut128
  Base = -> Fusion103027
  Tool = -> Fusion103023
FEATURE [Part::Cut] Cut114
  Base = -> Cut128
  Tool = -> Fusion103025
FEATURE [Part::Cut] Cut129
  Base = -> Cut114
  Tool = -> Box308
FEATURE [Part::Cut] Cut115
  Base = -> Cut129
  Tool = -> Box304
FEATURE [Part::Cut] Cut127  label="Edge Clips008"
  Base = -> Cut115
  Placement = pos=(20,20,0) rot=(0,0,1;3.14159rad)
  Tool = -> Box313
FEATURE [Part::Box] Box318  label="Re-level Edge Clip Block024"
  AttacherType = Attacher::AttachEngine3D
  Height = 10
  Length = 12
  Placement = pos=(-21.5,-2,-7) rot=(0,0,1;0rad)
  Width = 44
FEATURE [Part::Box] Box319  label="Cube266"
  AttacherType = Attacher::AttachEngine3D
  Height = 7
  Length = 10
  Placement = pos=(-15,10,-2) rot=(0,0,1;0rad)
  Width = 2
FEATURE [Part::Box] Box320  label="Cube267"
  AttacherType = Attacher::AttachEngine3D
  Height = 7
  Length = 4
  Placement = pos=(-6,12,-2) rot=(0,0,1;0rad)
  Width = 1
FEATURE [Part::Box] Box321  label="Chamfer Cube012"
  AttacherType = Attacher::AttachEngine3D
  Height = 10
  Length = 13
  Placement = pos=(-11.69,0,-1.19) rot=(0,-1,0;0.785398rad)
  Width = 40
FEATURE [Part::Sphere] Sphere102
  Angle1 = -90
  Angle2 = 90
  Angle3 = 360
  AttacherType = Attacher::AttachEngine3D
  Placement = pos=(-7.5,6.5,0.5) rot=(0,0,1;0rad)
  Radius = 1.25
FEATURE [Part::Box] Box322  label="Cube268"
  AttacherType = Attacher::AttachEngine3D
  Height = 7
  Length = 5
  Placement = pos=(-5,0,-2) rot=(0,0,1;0rad)
  Width = 40
FEATURE [Part::Box] Box323  label="Cube269"
  AttacherType = Attacher::AttachEngine3D
  Height = 7
  Length = 4
  Placement = pos=(-6,27.4,-2) rot=(0,0,1;0rad)
  Width = 7.2
FEATURE [Part::Box] Box324  label="Cube270"
  AttacherType = Attacher::AttachEngine3D
  Height = 7
  Length = 4
  Placement = pos=(-6,8,-2) rot=(0,0,1;0rad)
  Width = 2
FEATURE [Part::Box] Box325  label="Cube271"
  AttacherType = Attacher::AttachEngine3D
  Height = 7
  Length = 10
  Placement = pos=(-15,6,-2) rot=(0,0,1;0rad)
  Width = 2
FEATURE [Part::Sphere] Sphere103
  Angle1 = -90
  Angle2 = 90
  Angle3 = 360
  AttacherType = Attacher::AttachEngine3D
  Placement = pos=(-7.5,28,0.5) rot=(0,0,1;0rad)
  Radius = 1.5
FEATURE [Part::Box] Box326  label="Cube272"
  AttacherType = Attacher::AttachEngine3D
  Height = 7
  Length = 4
  Placement = pos=(-6,5,-2) rot=(0,0,1;0rad)
  Width = 1
FEATURE [Part::Box] Box327  label="Cube273"
  AttacherType = Attacher::AttachEngine3D
  Height = 7
  Length = 4
  Placement = pos=(-6,24.4,-2) rot=(0,0,1;0rad)
  Width = 1
FEATURE [Part::Sphere] Sphere104
  Angle1 = -90
  Angle2 = 90
  Angle3 = 360
  AttacherType = Attacher::AttachEngine3D
  Placement = pos=(-7.5,11.5,0.5) rot=(0,0,1;0rad)
  Radius = 1.25
FEATURE [Part::Box] Box328  label="Re-level Edge Clip Block025"
  AttacherType = Attacher::AttachEngine3D
  Height = 10
  Length = 20
  Placement = pos=(-19,-2,3) rot=(0,0,1;0rad)
  Width = 44
FEATURE [Part::Box] Box329  label="Cube274"
  AttacherType = Attacher::AttachEngine3D
  Height = 7
  Length = 10
  Placement = pos=(-15,34.6,-2) rot=(0,0,1;0rad)
  Width = 2
FEATURE [Part::Box] Box330  label="Cube275"
  AttacherType = Attacher::AttachEngine3D
  Height = 7
  Length = 10
  Placement = pos=(-15,25.4,-2) rot=(0,0,1;0rad)
  Width = 2
FEATURE [Part::MultiFuse] Fusion103030
  Shapes = -> [Box322,Box325,Box319,Box330,Box329]
FEATURE [Part::Box] Box331  label="Cube276"
  AttacherType = Attacher::AttachEngine3D
  Height = 7
  Length = 4
  Placement = pos=(-6,36.6,-2) rot=(0,0,1;0rad)
  Width = 1
FEATURE [Part::MultiFuse] Fusion103029  label="Extra Holes for Clips012"
  Shapes = -> [Box323,Box320,Box331,Box324,Box327,Box326]
FEATURE [Part::Fuse] Fusion103032  label="Bumps012"
  Base = -> Sphere102
  Tool = -> Sphere104
FEATURE [Part::Fuse] Fusion103028
  Base = -> Fusion103032
  Tool = -> Fusion103030
FEATURE [Part::Sphere] Sphere105
  Angle1 = -90
  Angle2 = 90
  Angle3 = 360
  AttacherType = Attacher::AttachEngine3D
  Placement = pos=(-7.5,34,0.5) rot=(0,0,1;0rad)
  Radius = 1.5
FEATURE [Part::Fuse] Fusion103031  label="Holes012"
  Base = -> Sphere103
  Tool = -> Sphere105
FEATURE [Part::Cut] Cut134
  Base = -> Fusion103028
  Tool = -> Fusion103031
FEATURE [Part::Cut] Cut130
  Base = -> Cut134
  Tool = -> Fusion103029
FEATURE [Part::Cut] Cut131
  Base = -> Cut130
  Tool = -> Box328
FEATURE [Part::Cut] Cut132
  Base = -> Cut131
  Tool = -> Box318
FEATURE [Part::Cut] Cut133  label="Edge Clips009"
  Base = -> Cut132
  Placement = pos=(-20,20,0) rot=(0,0,-1;1.5708rad)
  Tool = -> Box321
FEATURE [Part::Box] Box332  label="Cube277"
  AttacherType = Attacher::AttachEngine3D
  Height = 10
  Length = 10
  Placement = pos=(4,-26,1) rot=(0.205904,-0.974848,-0.085288;0.803573rad)
  Width = 15
FEATURE [Part::Box] Box333  label="Cube278"
  AttacherType = Attacher::AttachEngine3D
  Height = 10
  Length = 10
  Placement = pos=(-26,-4,1) rot=(-0.273007,-0.419215,-0.865867;1.78566rad)
  Width = 15
FEATURE [Part::Box] Box334  label="Cube279"
  AttacherType = Attacher::AttachEngine3D
  Height = 10
  Length = 10
  Placement = pos=(-4,26,1) rot=(0.381439,0.080566,0.920876;3.07487rad)
  Width = 15
FEATURE [Part::Box] Box335  label="Cube280"
  AttacherType = Attacher::AttachEngine3D
  Height = 10
  Length = 10
  Placement = pos=(26,4,1) rot=(0.442189,-0.287968,0.849437;1.66134rad)
  Width = 15
FEATURE [Part::MultiFuse] Fusion103033  label="Glue Dents002"
  Shapes = -> [Box332,Box333,Box334,Box335]
FEATURE [Part::MultiFuse] Fusion103034  label="Edge Clips Fusion002"
  Shapes = -> [Cut133,Cut121,Cut126,Cut127]
FEATURE [Part::MultiFuse] Fusion103035
  Placement = pos=(-15,-15,0) rot=(0,0,1;0rad)
  Shapes = -> [Box270,Cylinder042,Sphere089]
FEATURE [Part::Box] Box336  label="Square Nut Hole 026"
  AttacherType = Attacher::AttachEngine3D
  Height = 2
  Length = 5.8
  Placement = pos=(-2.9,2.9,2.1) rot=(1,0,0;3.14159rad)
  Width = 5.8
FEATURE [Part::Cylinder] Cylinder043
  Angle = 360
  AttacherType = Attacher::AttachEngine3D
  Height = 10
  Placement = pos=(0,0,6.7) rot=(1,0,0;3.14159rad)
  Radius = 1.7
FEATURE [Part::Sphere] Sphere106
  Angle1 = -90
  Angle2 = 90
  Angle3 = 360
  AttacherType = Attacher::AttachEngine3D
  Placement = pos=(0,0,4.3) rot=(1,0,0;3.14159rad)
  Radius = 3.35
FEATURE [Part::MultiFuse] Fusion103036
  Placement = pos=(-15,0,0) rot=(0,0,1;0rad)
  Shapes = -> [Box336,Cylinder043,Sphere106]
FEATURE [Part::Fuse] Fusion103037
  Base = -> Fusion103035
  Tool = -> Fusion103036
FEATURE [Part::MultiFuse] Fusion103038  label="Nut Holes001"
  Shapes = -> [Fusion103037,Fusion103012,Fusion103011,Fusion103010]
FEATURE [Part::Fuse] Fusion103039  label="Cube with Edge Clips001"
  Base = -> Box271
  Tool = -> Fusion103034
FEATURE [Part::Cut] Cut135
  Base = -> Fusion103039
  Tool = -> Fusion103033
FEATURE [Part::Cut] Cut136
  Base = -> Cut135
  Tool = -> Fusion103038
FEATURE [Part::Cut] Cut137
  Base = -> Cut136
  Tool = -> Chamfer016
FEATURE [Part::Cut] Cut138
  Base = -> Cut137
  Tool = -> Chamfer015
FEATURE [Part::Cut] Cut139  label="Nut Plate 1.003"
  Base = -> Cut138
  Tool = -> Box272
FEATURE [Part::Cylinder] Cylinder044
  Angle = 360
  AttacherType = Attacher::AttachEngine3D
  Height = 4
  Placement = pos=(-9.75,-9.75,-3) rot=(0,0,1;0rad)
  Radius = 1.5
FEATURE [Part::Cylinder] Cylinder045
  Angle = 360
  AttacherType = Attacher::AttachEngine3D
  Height = 4
  Placement = pos=(9.75,-9.75,-3) rot=(0,0,1;0rad)
  Radius = 1.5
FEATURE [Part::Cylinder] Cylinder046
  Angle = 360
  AttacherType = Attacher::AttachEngine3D
  Height = 4
  Placement = pos=(-9.75,9.75,-3) rot=(0,0,1;0rad)
  Radius = 1.5
FEATURE [Part::Cylinder] Cylinder047
  Angle = 360
  AttacherType = Attacher::AttachEngine3D
  Height = 4
  Placement = pos=(9.75,9.75,-3) rot=(0,0,1;0rad)
  Radius = 1.5
FEATURE [Part::MultiFuse] Fusion103040
  Shapes = -> [Cylinder044,Cylinder047,Cylinder045,Cylinder046]
FEATURE [Part::Cut] Cut140  label="Nut Plate 1.004"
  Base = -> Cut139
  Placement = pos=(0,0,-6) rot=(0,0,1;0rad)
  Tool = -> Fusion103040
FEATURE [App::DocumentObjectGroup] Group003  label="Cube-components"
  Group = -> [Cut112,Cut113]
FEATURE [Part::Box] Box404  label="Cube334"
  AttacherType = Attacher::AttachEngine3D
  Height = 14
  Length = 5
  Placement = pos=(20,20,-7) rot=(0,0,1;0rad)
  Width = 5
FEATURE [Part::Box] Box405  label="Cube335"
  AttacherType = Attacher::AttachEngine3D
  Height = 13
  Length = 15
  Placement = pos=(10,10,2) rot=(0,0,1;0rad)
  Width = 15
FEATURE [Part::FeaturePython] BevelGear001  # WARN: FeaturePython — macro-defined, semantics opaque (R4)
  Placement = pos=(7.81,7.81,10.5) rot=(0.862856,-0.357407,-0.357407;1.71775rad)
  backlash = 0
  beta = 0
  clearance = 0.1
  height = 3
  m = 1
  numpoints = 6
  pitch_angle = 30
  pressure_angle = 20
  reset_origin = true
  teeth = 10
FEATURE [Part::Cylinder] Cylinder054
  Angle = 360
  AttacherType = Attacher::AttachEngine3D
  Height = 22
  Radius = 11
FEATURE [Part::Cone] Cone
  Angle = 360
  AttacherType = Attacher::AttachEngine3D
  Height = 9
  Placement = pos=(8.52,8.52,10.5) rot=(0.862856,-0.357407,-0.357407;1.71777rad)
  Radius1 = 8
  Radius2 = 1.5
FEATURE [Part::Box] Box406004  label="Square Nut Hole 029"
  AttacherType = Attacher::AttachEngine3D
  Height = 2
  Length = 5.8
  Placement = pos=(15.7,19.8,7.6) rot=(0.862856,-0.357407,-0.357407;1.71777rad)
  Width = 14.8
FEATURE [Part::Box] Box406005  label="60mm-high"
  AttacherType = Attacher::AttachEngine3D
  Height = 60
  Length = 10
  Placement = pos=(-29,12,-3) rot=(0,0,1;0rad)
  Width = 10
FEATURE [Part::Cylinder] Cylinder057  label="small-gear-hub"
  Angle = 360
  AttacherType = Attacher::AttachEngine3D
  Height = 3
  Placement = pos=(7.5,7.5,10.5) rot=(0.862856,-0.357407,-0.357407;1.71777rad)
  Radius = 3.9
FEATURE [Part::Feature] Shape001  label="M3-hex-cavity"
  Placement = pos=(-0.5,-0.5,10.5) rot=(0.281085,0.678598,0.678598;2.59356rad)
  shape: bbox 11.56 x 11.56 x 5.5 mm, 8 faces (baked)
FEATURE [Part::Cylinder] Cylinder058  label="M3-screw-drive001"
  Angle = 360
  AttacherType = Attacher::AttachEngine3D
  Height = 33
  Placement = pos=(23.37,23.37,10.5) rot=(0.862856,-0.357407,-0.357407;1.71777rad)
  Radius = 1.75
FEATURE [Part::Box] Box406007  label="Cube338"
  AttacherType = Attacher::AttachEngine3D
  Height = 14
  Length = 14
  Placement = pos=(1.78,11.68,2) rot=(0,0,-1;0.785398rad)
  Width = 10
FEATURE [Part::Box] Box406008  label="slot-1"
  AttacherType = Attacher::AttachEngine3D
  Height = 36
  Length = 10.5
  Placement = pos=(10.22,17.65,0) rot=(0,0,-1;0.785398rad)
  Width = 28
FEATURE [Part::Cylinder] Cylinder059  label="M3-screw-drive002"
  Angle = 360
  AttacherType = Attacher::AttachEngine3D
  Height = 80
  Placement = pos=(26.8701,26.8701,8) rot=(0.862856,-0.357407,-0.357407;1.71777rad)
  Radius = 2.15
FEATURE [Part::Cylinder] Cylinder066  label="M3-screw-drive003"
  Angle = 360
  AttacherType = Attacher::AttachEngine3D
  Height = 33
  Placement = pos=(26.8701,26.8701,10.5) rot=(0.862856,-0.357407,-0.357407;1.71777rad)
  Radius = 1.75
FEATURE [Part::MultiFuse] Fusion103077010  label="finger-cavity"
  Shapes = -> [Cylinder066,Box406004]
FEATURE [Part::Box] Box406015  label="motor-clamp-0"
  AttacherType = Attacher::AttachEngine3D
  Height = 31
  Length = 53.28
  Placement = pos=(-13.8876,-23.7871,2) rot=(0,0,1;0.785398rad)
  Width = 14
FEATURE [Part::Box] Box406016  label="clamp-slot"
  AttacherType = Attacher::AttachEngine3D
  Height = 32
  Length = 49
  Placement = pos=(17.31,-15.9,17) rot=(0,0,1;2.35619rad)
  Width = 2
FEATURE [Part::Cylinder] Cylinder067
  Angle = 360
  AttacherType = Attacher::AttachEngine3D
  Height = 26
  Placement = pos=(0,0,20) rot=(0,0,1;0rad)
  Radius = 6.25
FEATURE [Part::Box] Box406017  label="gearbox001"
  AttacherType = Attacher::AttachEngine3D
  Height = 28
  Length = 16
  Placement = pos=(-8,-5.25,18) rot=(0,0,1;0rad)
  Width = 10.5
FEATURE [Part::MultiCommon] Common004  label="motor-hole"
  Placement = pos=(0,0,0) rot=(0,0,-1;0.785398rad)
  Shapes = -> [Cylinder067,Box406017]
FEATURE [Part::Cylinder] Cylinder068
  Angle = 360
  AttacherType = Attacher::AttachEngine3D
  Height = 12
  Placement = pos=(0,0,40) rot=(0.281085,0.678598,0.678598;2.59356rad)
  Radius = 1.2
FEATURE [Part::Cylinder] Cylinder069
  Angle = 360
  AttacherType = Attacher::AttachEngine3D
  Height = 12
  Placement = pos=(8.48528,8.48528,40) rot=(0.281085,0.678598,0.678598;2.59356rad)
  Radius = 2.2
FEATURE [Part::MultiFuse] Fusion103077013  label="M2-screw001"
  Placement = pos=(2,-14,0) rot=(0,0,1;0rad)
  Shapes = -> [Cylinder068,Cylinder069]
FEATURE [Part::Feature] Fusion103077013001
  Placement = pos=(-2e-15,-13,30) rot=(-0.281085,0.678598,0.678598;3.68962rad)
  shape: bbox 19.37 x 19.37 x 4.4 mm, 5 faces (baked)
FEATURE [Part::Cylinder] Cylinder070
  Angle = 360
  AttacherType = Attacher::AttachEngine3D
  Height = 12
  Placement = pos=(0,0,12) rot=(0,0,1;0rad)
  Radius = 2.2
FEATURE [Part::Cylinder] Cylinder071
  Angle = 360
  AttacherType = Attacher::AttachEngine3D
  Height = 12
  Radius = 1.2
FEATURE [Part::Cylinder] Cylinder072  label="M3-cap-screw-head"
  Angle = 360
  AttacherType = Attacher::AttachEngine3D
  Height = 10
  Placement = pos=(0,15,4) rot=(0,0,1;0rad)
  Radius = 3
FEATURE [Part::FeaturePython] BevelGear002  # WARN: FeaturePython — macro-defined, semantics opaque (R4)
  Placement = pos=(0,0,2.5) rot=(0,0,1;0rad)
  backlash = 0
  beta = 0
  clearance = 0.1
  height = 3
  m = 1
  numpoints = 6
  pitch_angle = 45
  pressure_angle = 20
  reset_origin = true
  teeth = 20
FEATURE [Part::MultiCommon] Common  label="big-gear-a"
  Shapes = -> [BevelGear002,Cylinder054]
FEATURE [Part::MultiCommon] Common005  label="small-gear-1"
  Shapes = -> [Cone,BevelGear001]
FEATURE [Part::MultiFuse] Fusion103077013004005  label="small-gear-2"
  Shapes = -> [Common005,Cylinder057]
FEATURE [Part::MultiFuse] Fusion103077013004006  label="small-gear-cavity"
  Shapes = -> [Cylinder058,Shape001]
FEATURE [Part::Cut] Cut173011005  label="small-gear 0.4"
  Base = -> Fusion103077013004005
  Tool = -> Fusion103077013004006
FEATURE [Part::Cylinder] Cylinder073  label="motor-bulge"
  Angle = 360
  AttacherType = Attacher::AttachEngine3D
  Height = 20
  Placement = pos=(0,0,23) rot=(0,0,1;0rad)
  Radius = 9
FEATURE [Part::Cylinder] Cylinder074  label="big-gear-clearance"
  Angle = 360
  AttacherType = Attacher::AttachEngine3D
  Height = 22
  Radius = 12
FEATURE [Part::Cylinder] Cylinder075  label="M3-cap-screw-head001"
  Angle = 360
  AttacherType = Attacher::AttachEngine3D
  Height = 10
  Placement = pos=(0,15,-6) rot=(0,0,1;0rad)
  Radius = 1.7
FEATURE [Part::MultiFuse] Fusion103077013004011  label="M3-cap-screw"
  Placement = pos=(0,0,5) rot=(0,0,1;0rad)
  Shapes = -> [Cylinder075,Cylinder072]
FEATURE [Part::Box] Box406019  label="motor-clamp-print-45"
  AttacherType = Attacher::AttachEngine3D
  Height = 30
  Length = 16.46
  Placement = pos=(-19.23,2.77,22) rot=(0.707107,0.707107,0;1.5708rad)
  Width = 16.46
FEATURE [Part::Feature] Box406008001  label="slot-2"
  Placement = pos=(-10.22,-17.65,0) rot=(0,0,1;2.35619rad)
  shape: bbox 27.22 x 27.22 x 36 mm, 6 faces (baked)
FEATURE [Part::Box] Box406008002  label="Cube339"
  AttacherType = Attacher::AttachEngine3D
  Height = 24
  Length = 23
  Placement = pos=(-1.06066,-15.2,-2) rot=(0,0,1;0.785398rad)
  Width = 20
FEATURE [Part::MultiFuse] Fusion103077013004013  label="finger-slots"
  Shapes = -> [Box406008,Box406008001]
FEATURE [Part::Chamfer] Chamfer024  label="motor-clamp-1"
  Base = -> Box406015
  Edges = 2 edges r=12: [Edge2,Edge6]
FEATURE [Part::Chamfer] Chamfer025  label="motor-clamp-2"
  Base = -> Chamfer024
  Edges = 4 edges r=2: [Edge1,Edge4,Edge5,Edge14]
FEATURE [Part::MultiFuse] Fusion103077013004016  label="motor-clamp-3"
  Shapes = -> [Chamfer025,Cylinder073]
FEATURE [Part::Box] Box406008003  label="Cube340"
  AttacherType = Attacher::AttachEngine3D
  Height = 6
  Length = 15
  Placement = pos=(-5,10,2) rot=(0,0,1;0rad)
  Width = 10
FEATURE [Part::Cut] Cut173011007  label="screw-land-1"
  Base = -> Box406008003
  Tool = -> Cylinder074
FEATURE [Part::Cone] Cone001
  Angle = 360
  AttacherType = Attacher::AttachEngine3D
  Height = 9
  Placement = pos=(8.52,8.52,10.5) rot=(0.862856,-0.357407,-0.357407;1.71777rad)
  Radius1 = 9
  Radius2 = 2.5
FEATURE [Part::Box] Box406008004  label="gearbox004"
  AttacherType = Attacher::AttachEngine3D
  Height = 9
  Length = 12
  Placement = pos=(-6,-5,0) rot=(0,0,1;0rad)
  Width = 10
FEATURE [Part::Cylinder] Cylinder076  label="boss002"
  Angle = 360
  AttacherType = Attacher::AttachEngine3D
  Height = 1
  Placement = pos=(0,0,-1) rot=(0,0,1;0rad)
  Radius = 2
FEATURE [Part::Cylinder] Cylinder077
  Angle = 360
  AttacherType = Attacher::AttachEngine3D
  Height = 15
  Placement = pos=(0,0,9) rot=(0,0,1;0rad)
  Radius = 6
FEATURE [Part::Box] Box406008005  label="gearbox005"
  AttacherType = Attacher::AttachEngine3D
  Height = 27
  Length = 16
  Placement = pos=(-8,-5,0) rot=(0,0,1;0rad)
  Width = 10
FEATURE [Part::MultiCommon] Common001  label="motor002"
  Shapes = -> [Cylinder077,Box406008005]
FEATURE [Part::Cylinder] Cylinder078  label="shaft-002"
  Angle = 360
  AttacherType = Attacher::AttachEngine3D
  Height = 10
  Placement = pos=(0,0,-10) rot=(0,0,1;0rad)
  Radius = 1.5
FEATURE [Part::Box] Box406008006  label="Cube341"
  AttacherType = Attacher::AttachEngine3D
  Height = 12
  Length = 10
  Placement = pos=(-5,1,-11) rot=(0,0,1;0rad)
  Width = 10
FEATURE [Part::Cut] Cut001  label="shaft002"
  Base = -> Cylinder078
  Tool = -> Box406008006
FEATURE [Part::MultiFuse] Fusion103077013004017004  label="motor-assembled"
  Placement = pos=(0,0,20.5) rot=(0,0,-1;0.785398rad)
  Shapes = -> [Box406008004,Cylinder076,Common001,Cut001]
FEATURE [Part::Cylinder] Cylinder079  label="shaft-003"
  Angle = 360
  AttacherType = Attacher::AttachEngine3D
  Height = 10
  Placement = pos=(0,0,-2) rot=(0,0,1;0rad)
  Radius = 1.75
FEATURE [Part::Box] Box406008007  label="Cube342"
  AttacherType = Attacher::AttachEngine3D
  Height = 12
  Length = 10
  Placement = pos=(-5,1.125,-2) rot=(0,0,1;0rad)
  Width = 10
FEATURE [Part::Cut] Cut173011011  label="motor-shaft"
  Base = -> Cylinder079
  Tool = -> Box406008007
FEATURE [Part::Cut] Cut173011012  label="big-gear-2"
  Base = -> Common
  Tool = -> Cut173011011
FEATURE [Part::Box] Box406008008  label="Cube343"
  AttacherType = Attacher::AttachEngine3D
  Height = 2
  Length = 19
  Placement = pos=(-9.5,-9.5,0) rot=(0,0,1;0rad)
  Width = 19
FEATURE [Part::Cylinder] Cylinder080  label="Cylinder078"
  Angle = 360
  AttacherType = Attacher::AttachEngine3D
  Height = 10
  Placement = pos=(0,0,-4) rot=(0,0,1;0rad)
  Radius = 1.8
FEATURE [Part::Cut] Cut173011013  label="filler-plate-1"
  Base = -> Box406008008
  Tool = -> Cylinder080
FEATURE [Part::Chamfer] Chamfer026  label="filler-plate-2"
  Base = -> Cut173011013
  Edges = 1 edges r=0.5: [Edge10]
FEATURE [Part::Chamfer] Chamfer027  label="filler-plate"
  Base = -> Chamfer026
  Edges = 4 edges r=0.5: [Edge10,Edge11,Edge13,Edge15]
FEATURE [Part::Box] Box406008009  label="Cube344"
  AttacherType = Attacher::AttachEngine3D
  Height = 3
  Length = 6
  Placement = pos=(19,19,-7) rot=(0,0,1;0rad)
  Width = 6
FEATURE [Part::Chamfer] Chamfer029  label="grip-1"
  Base = -> Box406008009
  Edges = 2 edges r=1: [Edge2,Edge10]
FEATURE [Part::Chamfer] Chamfer030  label="grip-2"
  Base = -> Chamfer029
  Edges = 1 edges r=1: [Edge1]
FEATURE [Part::Cut] Cut173011016  label="mounting-plate"
  Base = -> Cut139
  Placement = pos=(0,0,0) rot=(1,0,0;3.14159rad)
  Tool = -> Fusion103040
FEATURE [Part::Chamfer] Chamfer032  label="Old big-gear 0.1"
  Base = -> Cut173011012
  Edges = 3 edges r=0.5: [Edge124,Edge125,Edge126]
FEATURE [Part::Feature] Shape002  label="M3-head-cover"
  Placement = pos=(5,5,10.5) rot=(0.862856,-0.357407,-0.357407;1.71777rad)
  shape: bbox 5.347 x 5.347 x 5.25 mm, 8 faces (baked)
FEATURE [Part::Cylinder] Cylinder081  label="M3-screw-drive004"
  Angle = 360
  AttacherType = Attacher::AttachEngine3D
  Height = 20
  Placement = pos=(23.4,23.4,10.5) rot=(0.862856,-0.357407,-0.357407;1.71777rad)
  Radius = 4.5
FEATURE [Part::Feature] Cylinder081001
  Placement = pos=(-23.4,-23.4,10.5) rot=(0.281085,0.678598,0.678598;2.59356rad)
  shape: bbox 20.51 x 20.51 x 9 mm, 3 faces (baked)
FEATURE [Part::MultiFuse] Fusion103077013004017006  label="nut-cavities"
  Shapes = -> [Cylinder081001,Cylinder081]
FEATURE [App::DocumentObjectGroup] Group001  label="Old"
  Group = -> [Cut008,Cut009,Cut015,Cut018,Fusion021,Fusion023,Group,Cut039,Cut028,Cut032,Cut033,Fusion048,Cylinder068,Cylinder069,Cylinder071,Cylinder070,Fusion103077013004017006]
FEATURE [Part::Chamfer] Chamfer  label="finger-1"
  Base = -> Box405
  Edges = 2 edges r=8.5: [Edge3,Edge5]
FEATURE [Part::Cut] Cut173011017  label="finger-2"
  Base = -> Chamfer
  Tool = -> Box406007
FEATURE [Part::Fillet] Fillet  label="finger-3"
  Base = -> Cut173011017
  Edges = 2 edges r=1.5: [Edge8,Edge14]
FEATURE [Part::Chamfer] Chamfer033  label="grip-3"
  Base = -> Chamfer030
  Edges = 3 edges r=1: [Edge4,Edge10,Edge15]
FEATURE [Part::MultiFuse] Fusion103077013004017007  label="finger-4"
  Shapes = -> [Chamfer033,Box404,Fillet]
FEATURE [Part::Fillet] Fillet006  label="finger-5"
  Base = -> Fusion103077013004017007
  Edges = 4 edges r=3: [Edge33,Edge41,Edge51,Edge59]
FEATURE [Part::Cut] Cut173011018  label="finger-6"
  Base = -> Fillet006
  Tool = -> Fusion103077010
FEATURE [Part::Chamfer] Chamfer034  label="finger"
  Base = -> Cut173011018
  Edges = 4 edges r=0.7: [Edge81,Edge82,Edge83,Edge84]
FEATURE [Part::Box] Box406008010  label="Cube345"
  AttacherType = Attacher::AttachEngine3D
  Height = 5
  Length = 10
  Placement = pos=(4,5,0.8) rot=(0,0,1;0.785398rad)
  Width = 1
FEATURE [Part::Box] Box406008011  label="Cube346"
  AttacherType = Attacher::AttachEngine3D
  Height = 5
  Length = 10
  Placement = pos=(7.3,5,0.8) rot=(0,0,1;0.785398rad)
  Width = 1
FEATURE [Part::Fuse] Fusion103077013004017008
  Base = -> Box406008010
  Tool = -> Box406008011
FEATURE [Part::Feature] Fusion103077013004017008001
  Placement = pos=(-4.36408,4.36408,2.00532) rot=(0.707107,0.707107,0;0.628319rad)
  shape: bbox 12.71 x 10.04 x 6.004 mm, 12 faces, 2 solids (baked)
FEATURE [Part::Feature] Fusion103077013004017008002
  Placement = pos=(-7.06123,7.06123,7.25532) rot=(0.707107,0.707107,0;1.25664rad)
  shape: bbox 12.81 x 11.79 x 4.715 mm, 12 faces, 2 solids (baked)
FEATURE [Part::Feature] Fusion103077013004017008003
  Placement = pos=(-7.06123,7.06123,13.7447) rot=(0.707107,0.707107,0;1.88496rad)
  shape: bbox 11.79 x 12.81 x 4.715 mm, 12 faces, 2 solids (baked)
FEATURE [Part::Feature] Fusion103077013004017008004
  Placement = pos=(-4.36408,4.36408,18.9947) rot=(0.707107,0.707107,0;2.51327rad)
  shape: bbox 10.04 x 12.71 x 6.004 mm, 12 faces, 2 solids (baked)
FEATURE [Part::Feature] Fusion103077013004017008005
  Placement = pos=(-1e-15,1e-15,21) rot=(0.707107,0.707107,0;3.14159rad)
  shape: bbox 7.778 x 11.08 x 5 mm, 12 faces, 2 solids (baked)
FEATURE [Part::Feature] Fusion103077013004017008006
  Placement = pos=(4.36408,-4.36408,18.9947) rot=(0.707107,0.707107,0;3.76991rad)
  shape: bbox 10.04 x 12.71 x 6.004 mm, 12 faces, 2 solids (baked)
FEATURE [Part::Feature] Fusion103077013004017008007
  Placement = pos=(7.06123,-7.06123,13.7447) rot=(-0.707107,-0.707107,0;1.88496rad)
  shape: bbox 11.79 x 12.81 x 4.715 mm, 12 faces, 2 solids (baked)
FEATURE [Part::Feature] Fusion103077013004017008008
  Placement = pos=(7.06123,-7.06123,7.25532) rot=(-0.707107,-0.707107,0;1.25664rad)
  shape: bbox 12.81 x 11.79 x 4.715 mm, 12 faces, 2 solids (baked)
FEATURE [Part::Feature] Fusion103077013004017008009
  Placement = pos=(4.36408,-4.36408,2.00532) rot=(-0.707107,-0.707107,0;0.628319rad)
  shape: bbox 12.71 x 10.04 x 6.004 mm, 12 faces, 2 solids (baked)
FEATURE [Part::MultiFuse] Fusion103077013004017008010  label="Cut away for small gear"
  Shapes = -> [Fusion103077013004017008001,Fusion103077013004017008003,Fusion103077013004017008007,Fusion103077013004017008005,Fusion103077013004017008009,Fusion103077013004017008008,Fusion103077013004017008004,Fusion103077013004017008002,Fusion103077013004017008,Fusion103077013004017008006]
FEATURE [Part::Box] Box406008012  label="Cube347"
  AttacherType = Attacher::AttachEngine3D
  Height = 10
  Length = 10
  Placement = pos=(12,0.6,0) rot=(0,-1,0;0.698132rad)
  Width = 1
FEATURE [Part::Box] Box406008013  label="Cube348"
  AttacherType = Attacher::AttachEngine3D
  Height = 10
  Length = 10
  Placement = pos=(12,-1.6,0) rot=(0,-1,0;0.698132rad)
  Width = 1
FEATURE [Part::MultiFuse] Fusion103077013004017008011  label="tooth-thin"
  Shapes = -> [Box406008012,Box406008013]
FEATURE [Part::Feature] Fusion103077013004017008011001
  Placement = pos=(0,0,0) rot=(0,0,1;0.314159rad)
  shape: bbox 14.39 x 7.397 x 14.09 mm, 12 faces, 2 solids (baked)
FEATURE [Part::Feature] Fusion103077013004017008011002
  Placement = pos=(0,0,0) rot=(0,0,1;0.628319rad)
  shape: bbox 13.28 x 10.87 x 14.09 mm, 12 faces, 2 solids (baked)
FEATURE [Part::Feature] Fusion103077013004017008011003
  Placement = pos=(0,0,0) rot=(0,0,1;0.942478rad)
  shape: bbox 10.87 x 13.28 x 14.09 mm, 12 faces, 2 solids (baked)
FEATURE [Part::Feature] Fusion103077013004017008011004
  Placement = pos=(0,0,0) rot=(0,0,1;1.25664rad)
  shape: bbox 7.397 x 14.39 x 14.09 mm, 12 faces, 2 solids (baked)
FEATURE [Part::Feature] Fusion103077013004017008011005
  Placement = pos=(0,0,0) rot=(0,0,1;1.5708rad)
  shape: bbox 3.2 x 14.09 x 14.09 mm, 12 faces, 2 solids (baked)
FEATURE [Part::Feature] Fusion103077013004017008011006
  Placement = pos=(0,0,0) rot=(0,0,1;1.88496rad)
  shape: bbox 7.397 x 14.39 x 14.09 mm, 12 faces, 2 solids (baked)
FEATURE [Part::Feature] Fusion103077013004017008011007
  Placement = pos=(0,0,0) rot=(0,0,1;2.19911rad)
  shape: bbox 10.87 x 13.28 x 14.09 mm, 12 faces, 2 solids (baked)
FEATURE [Part::Feature] Fusion103077013004017008011008
  Placement = pos=(0,0,0) rot=(0,0,1;2.51327rad)
  shape: bbox 13.28 x 10.87 x 14.09 mm, 12 faces, 2 solids (baked)
FEATURE [Part::Feature] Fusion103077013004017008011009
  Placement = pos=(0,0,0) rot=(0,0,1;2.82743rad)
  shape: bbox 14.39 x 7.397 x 14.09 mm, 12 faces, 2 solids (baked)
FEATURE [Part::Feature] Fusion103077013004017008011010
  Placement = pos=(0,0,0) rot=(0,0,1;3.14159rad)
  shape: bbox 14.09 x 3.2 x 14.09 mm, 12 faces, 2 solids (baked)
FEATURE [Part::Feature] Fusion103077013004017008011011
  Placement = pos=(0,0,0) rot=(0,0,1;3.45575rad)
  shape: bbox 14.39 x 7.397 x 14.09 mm, 12 faces, 2 solids (baked)
FEATURE [Part::Feature] Fusion103077013004017008011012
  Placement = pos=(0,0,0) rot=(0,0,1;3.76991rad)
  shape: bbox 13.28 x 10.87 x 14.09 mm, 12 faces, 2 solids (baked)
FEATURE [Part::Feature] Fusion103077013004017008011013
  Placement = pos=(0,0,0) rot=(0,0,1;4.08407rad)
  shape: bbox 10.87 x 13.28 x 14.09 mm, 12 faces, 2 solids (baked)
FEATURE [Part::Feature] Fusion103077013004017008011014
  Placement = pos=(0,0,0) rot=(0,0,-1;1.88496rad)
  shape: bbox 7.397 x 14.39 x 14.09 mm, 12 faces, 2 solids (baked)
FEATURE [Part::Feature] Fusion103077013004017008011015
  Placement = pos=(0,0,0) rot=(0,0,-1;1.5708rad)
  shape: bbox 3.2 x 14.09 x 14.09 mm, 12 faces, 2 solids (baked)
FEATURE [Part::Feature] Fusion103077013004017008011016
  Placement = pos=(0,0,0) rot=(0,0,-1;1.25664rad)
  shape: bbox 7.397 x 14.39 x 14.09 mm, 12 faces, 2 solids (baked)
FEATURE [Part::Feature] Fusion103077013004017008011017
  Placement = pos=(0,0,0) rot=(0,0,-1;0.942478rad)
  shape: bbox 10.87 x 13.28 x 14.09 mm, 12 faces, 2 solids (baked)
FEATURE [Part::Feature] Fusion103077013004017008011018
  Placement = pos=(0,0,0) rot=(0,0,-1;0.628319rad)
  shape: bbox 13.28 x 10.87 x 14.09 mm, 12 faces, 2 solids (baked)
FEATURE [Part::Feature] Fusion103077013004017008011019
  Placement = pos=(0,0,0) rot=(0,0,-1;0.314159rad)
  shape: bbox 14.39 x 7.397 x 14.09 mm, 12 faces, 2 solids (baked)
FEATURE [Part::MultiFuse] Fusion103077013004017008011020  label="Big Gear teeth-thin"
  Shapes = -> [Fusion103077013004017008011,Fusion103077013004017008011015,Fusion103077013004017008011014,Fusion103077013004017008011016,Fusion103077013004017008011017,Fusion103077013004017008011001,Fusion103077013004017008011003,Fusion103077013004017008011005,Fusion103077013004017008011011,Fusion103077013004017008011012,Fusion103077013004017008011013,Fusion103077013004017008011008,Fusion103077013004017008011006,+7 more]
FEATURE [Part::FeaturePython] BevelGear003  # WARN: FeaturePython — macro-defined, semantics opaque (R4)
  Placement = pos=(0,0,2.5) rot=(0,0,1;0rad)
  backlash = 0
  beta = 0
  clearance = 0.1
  height = 3.9
  m = 1
  numpoints = 6
  pitch_angle = 45
  pressure_angle = 20
  reset_origin = true
  teeth = 20
FEATURE [Part::Cylinder] Cylinder081002
  Angle = 360
  AttacherType = Attacher::AttachEngine3D
  Height = 22
  Radius = 11
FEATURE [Part::MultiCommon] Common006  label="big-gear-a001"
  Shapes = -> [BevelGear003,Cylinder081002]
FEATURE [Part::Cylinder] Cylinder081003  label="shaft-004"
  Angle = 360
  AttacherType = Attacher::AttachEngine3D
  Height = 10
  Placement = pos=(0,0,-2) rot=(0,0,1;0rad)
  Radius = 1.75
FEATURE [Part::Box] Box406008014  label="Cube349"
  AttacherType = Attacher::AttachEngine3D
  Height = 12
  Length = 10
  Placement = pos=(-5,1.125,-2) rot=(0,0,1;0rad)
  Width = 10
FEATURE [Part::Cut] Cut173011020  label="motor-shaft001"
  Base = -> Cylinder081003
  Tool = -> Box406008014
FEATURE [Part::Cut] Cut173011021  label="big-gear-003"
  Base = -> Common006
  Tool = -> Cut173011020
FEATURE [Part::Chamfer] Chamfer035  label="big-gear001"
  Base = -> Cut173011021
  Edges = 3 edges r=0.5: [Edge124,Edge125,Edge126]
FEATURE [Part::Cylinder] Cylinder081004  label="Cylinder081003"
  Angle = 360
  AttacherType = Attacher::AttachEngine3D
  Height = 6.5
  Placement = pos=(0,0,4) rot=(0,0,1;0rad)
  Radius = 5
FEATURE [Part::Box] Box406008015  label="Cube350"
  AttacherType = Attacher::AttachEngine3D
  Height = 12
  Length = 10
  Placement = pos=(-5,1.125,0) rot=(0,0,1;0rad)
  Width = 10
FEATURE [Part::Cylinder] Cylinder081005  label="shaft-005"
  Angle = 360
  AttacherType = Attacher::AttachEngine3D
  Height = 10
  Placement = pos=(0,0,1) rot=(0,0,1;0rad)
  Radius = 1.75
FEATURE [Part::Cut] Cut173011023
  Base = -> Cylinder081005
  Tool = -> Box406008015
FEATURE [Part::Fuse] Fusion103077013004017008011022
  Base = -> Box406019
  Tool = -> Box406008002
FEATURE [Part::Box] Box406008016  label="Cube351"
  AttacherType = Attacher::AttachEngine3D
  Height = 10
  Length = 17
  Placement = pos=(1.9,-9.6,-1) rot=(0,0,1;0.785398rad)
  Width = 16
FEATURE [Part::Box] Box406008017  label="gearbox006"
  AttacherType = Attacher::AttachEngine3D
  Height = 9
  Length = 12.5
  Placement = pos=(8.125,-0.625,21) rot=(0,0,1;2.35619rad)
  Width = 10.5
FEATURE [Part::Cut] Cut173011025
  Base = -> Fusion103077013004016
  Tool = -> Fusion103077013004013
FEATURE [Part::Cut] Cut173011026
  Base = -> Cut173011025
  Tool = -> Fusion103077013004017008011022
FEATURE [Part::Cut] Cut173011027
  Base = -> Cut173011026
  Tool = -> Common004
FEATURE [Part::Cut] Cut173011028
  Base = -> Cut173011027
  Tool = -> Box406008017
FEATURE [Part::Cut] Cut173011029
  Base = -> Cut173011028
  Tool = -> Box406016
FEATURE [Part::Cylinder] Cylinder081006
  Angle = 360
  AttacherType = Attacher::AttachEngine3D
  Height = 12
  Placement = pos=(0,0,40) rot=(0.281085,0.678598,0.678598;2.59356rad)
  Radius = 1.2
FEATURE [Part::Cylinder] Cylinder081007
  Angle = 360
  AttacherType = Attacher::AttachEngine3D
  Height = 12
  Placement = pos=(8.48528,8.48528,40) rot=(0.281085,0.678598,0.678598;2.59356rad)
  Radius = 2.2
FEATURE [Part::MultiFuse] Fusion103077013004017008011023  label="M2-screw002"
  Placement = pos=(-2,14,0) rot=(0,0,1;3.14159rad)
  Shapes = -> [Cylinder081006,Cylinder081007]
FEATURE [Part::Box] Box406008018  label="Cube352"
  AttacherType = Attacher::AttachEngine3D
  Height = 10.35
  Length = 3.68
  Placement = pos=(13.02,-11.61,32.65) rot=(0,0,1;0.785398rad)
  Width = 10
FEATURE [Part::Chamfer] Chamfer038
  Base = -> Box406008018
  Edges = 1 edges r=9: [Edge9]
FEATURE [Part::Cut] Cut173011030
  Base = -> Chamfer038
  Tool = -> Fusion103077013
FEATURE [Part::Box] Box406008019  label="Cube353"
  AttacherType = Attacher::AttachEngine3D
  Height = 10
  Length = 10
  Placement = pos=(17,-17,35) rot=(0,0,1;0.785398rad)
  Width = 10
FEATURE [Part::Cut] Cut173011031
  Base = -> Cut173011030
  Tool = -> Box406008019
FEATURE [Part::Box] Box406008020  label="Cube354"
  AttacherType = Attacher::AttachEngine3D
  Height = 10
  Length = 10
  Placement = pos=(-13.7,20.31,35) rot=(0,0,1;3.92699rad)
  Width = 10
FEATURE [Part::Box] Box406008021  label="Cube355"
  AttacherType = Attacher::AttachEngine3D
  Height = 10.35
  Length = 3.68
  Placement = pos=(-9.01,15.62,32.65) rot=(0,0,1;3.92699rad)
  Width = 10
FEATURE [Part::Chamfer] Chamfer039
  Base = -> Box406008021
  Edges = 1 edges r=9: [Edge9]
FEATURE [Part::Cut] Cut173011032
  Base = -> Chamfer039
  Tool = -> Box406008020
FEATURE [Part::Cut] Cut173011033
  Base = -> Cut173011032
  Tool = -> Fusion103077013004017008011023
FEATURE [Part::MultiFuse] Fusion103077013004017008011024
  Shapes = -> [Cut173011029,Cut173011031,Cut173011033]
FEATURE [Part::Fillet] Fillet007
  Base = -> Fusion103077013004017008011024
  Edges = 2 edges r=1: [Edge110,Edge115]
FEATURE [Part::Box] Box406008022  label="Cube356"
  AttacherType = Attacher::AttachEngine3D
  Height = 50
  Length = 50
  Placement = pos=(-21,-50,0) rot=(0,0,1;0.785398rad)
  Width = 50
FEATURE [Part::Cylinder] Cylinder081008  label="big-gear-clearance001"
  Angle = 360
  AttacherType = Attacher::AttachEngine3D
  Height = 22
  Radius = 12
FEATURE [Part::Box] Box406008023  label="Cube357"
  AttacherType = Attacher::AttachEngine3D
  Height = 6
  Length = 15
  Placement = pos=(-5,10,2) rot=(0,0,1;0rad)
  Width = 10
FEATURE [Part::Cut] Cut173011034  label="screw-land-002"
  Base = -> Box406008023
  Placement = pos=(0,0,0) rot=(0,0,1;0.785398rad)
  Tool = -> Cylinder081008
FEATURE [Part::Mirroring] Part__Mirroring  label="screw-land-002 (Mirror #1)"
  Base = (0,0,0)
  Normal = (1,0,0)
  Placement = pos=(0,0,0) rot=(0,0,-1;0.785398rad)
  Source = -> Cut173011034
FEATURE [Part::Cylinder] Cylinder081009  label="M3-cap-screw-head002"
  Angle = 360
  AttacherType = Attacher::AttachEngine3D
  Height = 10
  Placement = pos=(0,15,4) rot=(0,0,1;0rad)
  Radius = 3
FEATURE [Part::Cylinder] Cylinder081010  label="M3-cap-screw-head003"
  Angle = 360
  AttacherType = Attacher::AttachEngine3D
  Height = 10
  Placement = pos=(0,15,-6) rot=(0,0,1;0rad)
  Radius = 1.7
FEATURE [Part::MultiFuse] Fusion103077013004017008011025  label="M3-cap-screw001"
  Placement = pos=(0,0,5) rot=(0,0,1;0.785398rad)
  Shapes = -> [Cylinder081010,Cylinder081009]
FEATURE [Part::Mirroring] Part__Mirroring001  label="M3-cap-screw001 (Mirror #2)"
  Base = (0,0,0)
  Normal = (1,0,0)
  Placement = pos=(0,0,0) rot=(0,0,-1;0.785398rad)
  Source = -> Fusion103077013004017008011025
FEATURE [Part::MultiFuse] Fusion103077013004017008011026
  Shapes = -> [Part__Mirroring,Cut173011007]
FEATURE [Part::MultiFuse] Fusion103077013004017008011027
  Shapes = -> [Part__Mirroring001,Fusion103077013004011,Box406008016]
FEATURE [Part::Cut] Cut173011035
  Base = -> Fusion103077013004017008011026
  Tool = -> Fusion103077013004017008011027
FEATURE [Part::Fillet] Fillet008
  Base = -> Cut173011035
  Edges = 2 edges r=3: [Edge4,Edge50]
FEATURE [Part::Feature] Shape
  Placement = pos=(-3.57,12.43,40) rot=(0,0.816497,-0.57735;4.18879rad)
  shape: bbox 5.276 x 5.276 x 4.461 mm, 8 faces (baked)
FEATURE [Drawing::FeatureViewAnnotation] Annotation010
  Font = Sans
  Rotation = 0
  Scale = 7
  ViewResult = <g transform="translate(10,10) rotate(0)">\n<text id="Annotation010"\n font-family="Sans"\n font-size="7"\n fill="#000000">\n<tspan x="0" dy="1em"></tspan>\n</text>\n</g>
  Visible = true
  X = 10
  Y = 10
FEATURE [Drawing::FeatureViewAnnotation] Annotation011
  Font = Sans
  Rotation = 0
  Scale = 5
  Text = Rotated Slots and amended screw clamp position and added nut recess. Cut in half. Made slots in the screw lands so the gear can freely rotate.
  ViewResult = <g transform="translate(10,60) rotate(0)">\n<text id="Annotation011"\n font-family="Sans"\n font-size="5"\n fill="#000000">\n<tspan x="0" dy="1em">Rotated Slots and amended screw clamp position and added nut recess. Cut in half. Made slots in the screw lands so the gear can freely rotate.</tspan>\n<tspan x="0" dy="1em"></tspan>\n</text>\n</g>
  Visible = true
  X = 10
  Y = 60
FEATURE [Part::Fillet] Fillet009
  Base = -> Fillet008
  Edges = 2 edges r=3: [Edge3,Edge42]
FEATURE [Part::MultiFuse] Fusion103077013004017008011028
  Shapes = -> [Fillet009,Fillet007]
FEATURE [Part::Cut] Cut173011036
  Base = -> Fusion103077013004017008011028
  Tool = -> Box406008022
FEATURE [Part::Cut] Cut173011037
  Base = -> Cut173011036
  Tool = -> Shape
FEATURE [Part::Cut] Cut173011038
  Base = -> Cut173011037
  Placement = pos=(0,0,0) rot=(0,0,1;0.785398rad)
  Tool = -> Cylinder059
FEATURE [Part::Fuse] Fusion103077013004017008011029
  Base = -> Chamfer035
  Tool = -> Cylinder081004
FEATURE [Part::Cut] Cut173011039  label="Big Gear 0.4 a"
  Base = -> Fusion103077013004017008011029
  Tool = -> Cut173011023
FEATURE [Drawing::FeatureViewAnnotation] Annotation012
  Font = Sans
  Rotation = 0
  Scale = 7
  ViewResult = <g transform="translate(10,10) rotate(0)">\n<text id="Annotation012"\n font-family="Sans"\n font-size="7"\n fill="#000000">\n<tspan x="0" dy="1em"></tspan>\n</text>\n</g>
  Visible = true
  X = 10
  Y = 10
FEATURE [Drawing::FeatureViewAnnotation] Annotation013
  Font = Sans
  Rotation = 0
  Scale = 7
  ViewResult = <g transform="translate(10,10) rotate(0)">\n<text id="Annotation013"\n font-family="Sans"\n font-size="7"\n fill="#000000">\n<tspan x="0" dy="1em"></tspan>\n</text>\n</g>
  Visible = true
  X = 10
  Y = 10
FEATURE [Drawing::FeatureViewAnnotation] Annotation014
  Font = Sans
  Rotation = 0
  Scale = 7
  ViewResult = <g transform="translate(10,10) rotate(0)">\n<text id="Annotation014"\n font-family="Sans"\n font-size="7"\n fill="#000000">\n<tspan x="0" dy="1em"></tspan>\n</text>\n</g>
  Visible = true
  X = 10
  Y = 10
FEATURE [Drawing::FeaturePage] Page
  EditableTexts = AUTHOR NAME | CREATION DATE | SUPERVISOR NAME | CHECK DATE | SCALE | WEIGHT | NUMBER | SHEET | TITLE | SUBTITLE
  Group = -> [Annotation,Annotation001,Annotation002,Annotation004,Annotation007,Annotation008,Annotation010,Annotation012,Annotation013,Annotation014]
  Template = <path>
FEATURE [Drawing::FeatureViewAnnotation] Annotation015
  Font = Sans
  Rotation = 0
  Scale = 5
  Text = 0.4 Switched back to thicker teeth on gears
  ViewResult = <g transform="translate(10,70) rotate(0)">\n<text id="Annotation015"\n font-family="Sans"\n font-size="5"\n fill="#000000">\n<tspan x="0" dy="1em">0.4 Switched back to thicker teeth on gears</tspan>\n<tspan x="0" dy="1em"></tspan>\n</text>\n</g>
  Visible = true
  X = 10
  Y = 70
FEATURE [Part::Chamfer] Chamfer040  label="big-gear 0.4 b"
  Base = -> Cut173011039
  Edges = 3 edges r=0.5: [Edge125,Edge126,Edge127]
FEATURE [Part::Chamfer] Chamfer041  label="big gear 0.4 a"
  Base = -> Chamfer040
  Edges = 3 edges r=1: [Edge142,Edge144,Edge145]
FEATURE [Part::Cone] Cone002
  Angle = 360
  AttacherType = Attacher::AttachEngine3D
  Height = 5
  Placement = pos=(0,0,3.6) rot=(0,0,1;0rad)
  Radius1 = 14
  Radius2 = 4
FEATURE [Part::Cylinder] Cylinder081011  label="Cylinder081008"
  Angle = 360
  AttacherType = Attacher::AttachEngine3D
  Height = 10
  Placement = pos=(0,0,4) rot=(0,0,1;0rad)
  Radius = 14
FEATURE [Part::Cut] Cut173011040
  Base = -> Cylinder081011
  Tool = -> Cone002
FEATURE [Part::Cylinder] Cylinder081012  label="Cylinder081009"
  Angle = 360
  AttacherType = Attacher::AttachEngine3D
  Height = 15
  Radius = 8
FEATURE [Part::Cut] Cut173011041
  Base = -> Cut173011040
  Tool = -> Cylinder081012
FEATURE [Part::Cut] Cut173011042  label="big gear 0.4"
  Base = -> Chamfer041
  Tool = -> Cut173011041
FEATURE [App::DocumentObjectGroup] Group004
FEATURE [App::DocumentObjectGroup] Group002  label="Old 0.1"
  Group = -> [Sphere027,Sphere028,Sphere029,Sphere031,Sphere032,Sphere033,Sphere034,Cylinder012,Cylinder016,Cylinder015,Cylinder014,Cylinder013,Cylinder017,Cylinder019,Box067,Box073,Box071,Box068,Box070,Box072,Box074,Group004]
FEATURE [App::DocumentObjectGroup] Group005  label="Old 0.5"
  Group = -> [Cut173011042,Fusion103077013004017008011020,Fusion103077013004017008010,Chamfer032,Shape002,Cut173011005]
FEATURE [Part::Cylinder] Cylinder081013  label="Cylinder081010"
  Angle = 360
  AttacherType = Attacher::AttachEngine3D
  Height = 10
  Placement = pos=(0,0,12) rot=(0,0,1;0rad)
  Radius = 1.5
FEATURE [Part::Cylinder] Cylinder081014  label="Cylinder081011"
  Angle = 360
  AttacherType = Attacher::AttachEngine3D
  Height = 4
  Placement = pos=(0,0,16) rot=(0,0,1;0rad)
  Radius = 4
FEATURE [Part::Cylinder] Cylinder081015  label="Cylinder081012"
  Angle = 360
  AttacherType = Attacher::AttachEngine3D
  Height = 2
  Placement = pos=(0,0,14) rot=(0,0,1;0rad)
  Radius = 5.355
FEATURE [Part::Cone] Cone003
  Angle = 360
  AttacherType = Attacher::AttachEngine3D
  Height = 1.71
  Placement = pos=(0,0,12.3) rot=(0,0,1;0rad)
  Radius1 = 3.6
  Radius2 = 5.31
FEATURE [Part::Cylinder] Cylinder081016  label="Cylinder081013"
  Angle = 360
  AttacherType = Attacher::AttachEngine3D
  Height = 10
  Placement = pos=(0,12,8) rot=(1,0,0;1.5708rad)
  Radius = 1.5
FEATURE [Part::Cylinder] Cylinder081017  label="Cylinder081014"
  Angle = 360
  AttacherType = Attacher::AttachEngine3D
  Height = 4
  Placement = pos=(0,11,8) rot=(1,0,0;1.5708rad)
  Radius = 4
FEATURE [Part::Cylinder] Cylinder081018  label="Cylinder081015"
  Angle = 360
  AttacherType = Attacher::AttachEngine3D
  Height = 2
  Placement = pos=(0,7,8) rot=(1,0,0;1.5708rad)
  Radius = 5.355
FEATURE [Part::Cone] Cone004
  Angle = 360
  AttacherType = Attacher::AttachEngine3D
  Height = 1.71
  Placement = pos=(0,5,8) rot=(1,0,0;1.5708rad)
  Radius1 = 5.31
  Radius2 = 3.6
FEATURE [Drawing::FeatureViewAnnotation] Annotation016
  Font = Sans
  Rotation = 0
  Scale = 5
  Text = 0.5 Modelled RS Gears 521-6036 and moved the M3 Screw drive down by 2.5mm
  ViewResult = <g transform="translate(10,80) rotate(0)">\n<text id="Annotation016"\n font-family="Sans"\n font-size="5"\n fill="#000000">\n<tspan x="0" dy="1em">0.5 Modelled RS Gears 521-6036 and moved the M3 Screw drive down by 2.5mm</tspan>\n<tspan x="0" dy="1em"></tspan>\n</text>\n</g>
  Visible = true
  X = 10
  Y = 80
FEATURE [Drawing::FeaturePage] Page001
  EditableTexts = AUTHOR NAME | CREATION DATE | SUPERVISOR NAME | CHECK DATE | SCALE | WEIGHT | NUMBER | SHEET | TITLE | SUBTITLE
  Group = -> [Annotation003,Annotation005,Annotation006,Annotation009,Annotation011,Annotation015,Annotation016]
  Template = <path>
note: 2 file-system paths scrubbed to <path> (originals preserved in the JSON sidecar)
